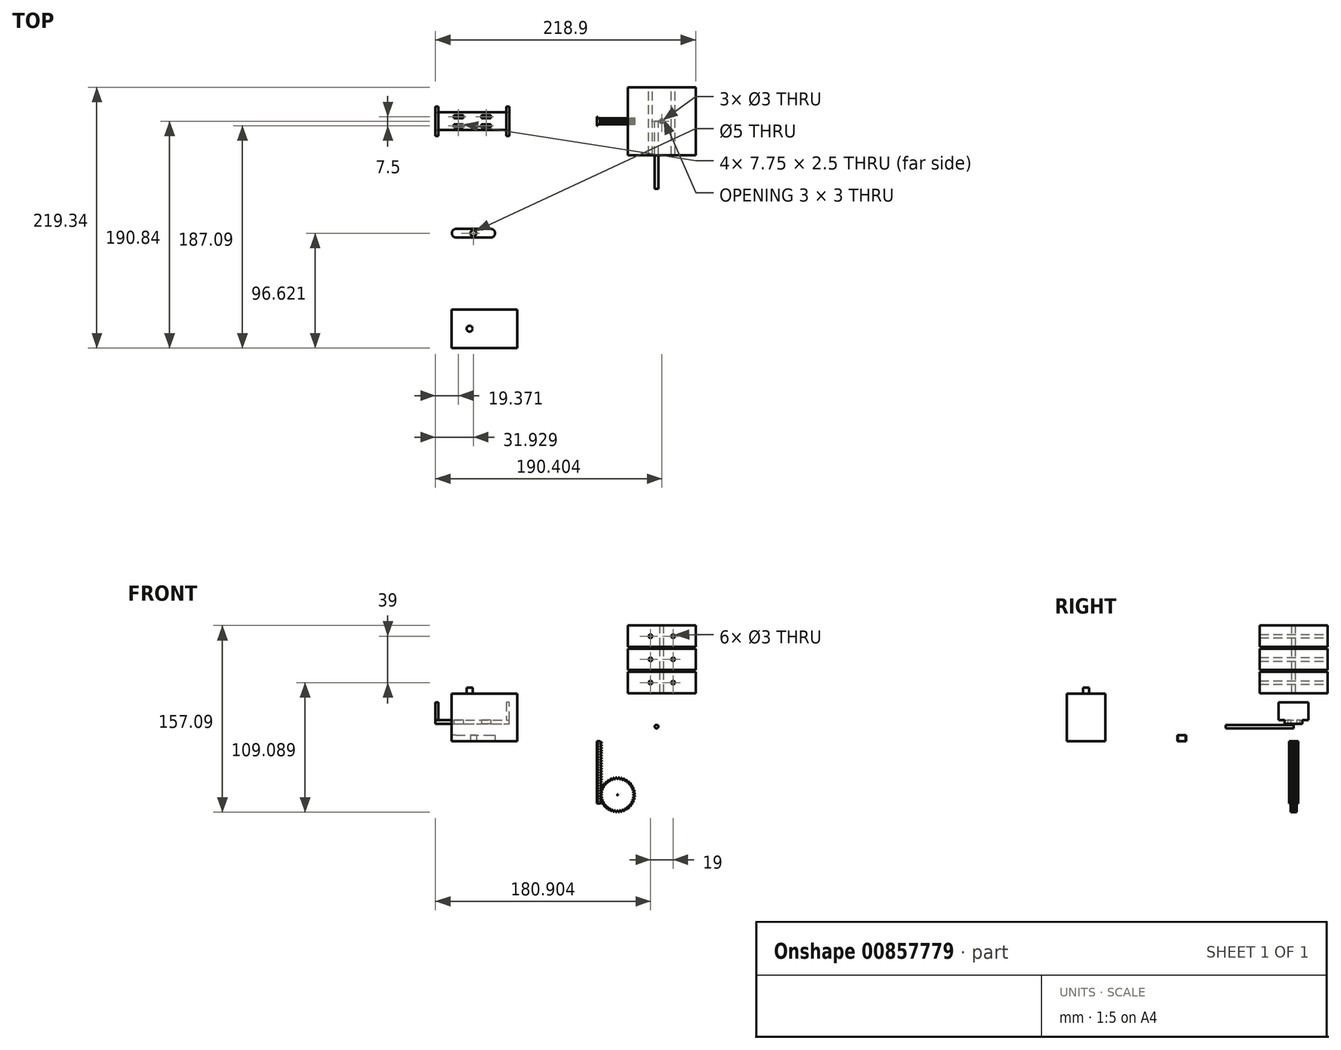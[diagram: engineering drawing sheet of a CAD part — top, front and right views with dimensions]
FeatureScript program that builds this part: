
annotation { "Feature Type Name" : "Feature", "Feature Type Description" : "" }
export const myFeature = defineFeature(function(context is Context, id is Id, definition is map)
    precondition{}
    {
        {
            var Q0;
            Q0=qCreatedBy(makeId("Front.planeOp"),FACE);
            var sketch = newSketch(context, id + "F0", { "sketchPlane" : qUnion([Q0])});
            skLineSegment(sketch, "E0", {"start": v(-13.26, -89.9) * mm, "end": v(-11.85, -89.4) * mm, "construction": true});
            skLineSegment(sketch, "E1", {"start": v(-11.85, -89.4) * mm, "end": v(-11.85, -88.8) * mm, "construction": true});
            skLineSegment(sketch, "E2", {"start": v(-11.85, -88.8) * mm, "end": v(-13.26, -88.31) * mm, "construction": true});
            skLineSegment(sketch, "E3", {"start": v(-13.26, -88.31) * mm, "end": v(-13.26, -87.7) * mm, "construction": true});
            skLineSegment(sketch, "E4", {"start": v(-13.26, -87.7) * mm, "end": v(-11.85, -87.21) * mm, "construction": true});
            skLineSegment(sketch, "E5", {"start": v(-11.85, -87.21) * mm, "end": v(-11.85, -86.6) * mm, "construction": true});
            skLineSegment(sketch, "E6", {"start": v(-11.85, -86.6) * mm, "end": v(-13.26, -86.12) * mm, "construction": true});
            skLineSegment(sketch, "E7", {"start": v(-13.26, -86.12) * mm, "end": v(-13.26, -85.5) * mm, "construction": true});
            skLineSegment(sketch, "E8", {"start": v(-13.26, -85.5) * mm, "end": v(-11.85, -85.02) * mm, "construction": true});
            skLineSegment(sketch, "E9", {"start": v(-11.85, -85.02) * mm, "end": v(-11.85, -84.4) * mm, "construction": true});
            skLineSegment(sketch, "E10", {"start": v(-11.85, -84.4) * mm, "end": v(-13.26, -83.92) * mm, "construction": true});
            skLineSegment(sketch, "E11", {"start": v(-13.26, -83.92) * mm, "end": v(-13.26, -83.3) * mm, "construction": true});
            skLineSegment(sketch, "E12", {"start": v(-13.26, -83.3) * mm, "end": v(-11.85, -82.82) * mm, "construction": true});
            skLineSegment(sketch, "E13", {"start": v(-11.85, -82.82) * mm, "end": v(-11.85, -82.2) * mm, "construction": true});
            skLineSegment(sketch, "E14", {"start": v(-11.85, -82.2) * mm, "end": v(-13.26, -81.73) * mm, "construction": true});
            skLineSegment(sketch, "E15", {"start": v(-13.26, -81.73) * mm, "end": v(-13.26, -81.11) * mm, "construction": true});
            skLineSegment(sketch, "E16", {"start": v(-13.26, -81.11) * mm, "end": v(-11.85, -80.63) * mm, "construction": true});
            skLineSegment(sketch, "E17", {"start": v(-11.85, -80.63) * mm, "end": v(-11.85, -80.01) * mm, "construction": true});
            skLineSegment(sketch, "E18", {"start": v(-11.85, -80.01) * mm, "end": v(-13.26, -79.53) * mm, "construction": true});
            skLineSegment(sketch, "E19", {"start": v(-13.26, -79.53) * mm, "end": v(-13.26, -78.92) * mm, "construction": true});
            skLineSegment(sketch, "E20", {"start": v(-13.26, -78.92) * mm, "end": v(-11.85, -78.43) * mm, "construction": true});
            skLineSegment(sketch, "E21", {"start": v(-11.85, -78.43) * mm, "end": v(-11.85, -77.82) * mm, "construction": true});
            skLineSegment(sketch, "E22", {"start": v(-11.85, -77.82) * mm, "end": v(-13.26, -77.34) * mm, "construction": true});
            skLineSegment(sketch, "E23", {"start": v(-13.26, -77.34) * mm, "end": v(-13.26, -76.72) * mm, "construction": true});
            skLineSegment(sketch, "E24", {"start": v(-13.26, -76.72) * mm, "end": v(-11.85, -76.24) * mm, "construction": true});
            skLineSegment(sketch, "E25", {"start": v(-11.85, -76.24) * mm, "end": v(-11.85, -75.62) * mm, "construction": true});
            skLineSegment(sketch, "E26", {"start": v(-11.85, -75.62) * mm, "end": v(-13.26, -75.14) * mm, "construction": true});
            skLineSegment(sketch, "E27", {"start": v(-13.26, -75.14) * mm, "end": v(-13.26, -74.53) * mm, "construction": true});
            skLineSegment(sketch, "E28", {"start": v(-13.26, -74.53) * mm, "end": v(-11.85, -74.04) * mm, "construction": true});
            skLineSegment(sketch, "E29", {"start": v(-11.85, -74.04) * mm, "end": v(-11.85, -73.43) * mm, "construction": true});
            skLineSegment(sketch, "E30", {"start": v(-11.85, -73.43) * mm, "end": v(-13.26, -72.95) * mm, "construction": true});
            skLineSegment(sketch, "E31", {"start": v(-13.26, -72.95) * mm, "end": v(-13.26, -72.33) * mm, "construction": true});
            skLineSegment(sketch, "E32", {"start": v(-13.26, -72.33) * mm, "end": v(-11.85, -71.85) * mm, "construction": true});
            skLineSegment(sketch, "E33", {"start": v(-11.85, -71.85) * mm, "end": v(-11.85, -71.23) * mm, "construction": true});
            skLineSegment(sketch, "E34", {"start": v(-11.85, -71.23) * mm, "end": v(-13.26, -70.75) * mm, "construction": true});
            skLineSegment(sketch, "E35", {"start": v(-13.26, -70.75) * mm, "end": v(-13.26, -70.13) * mm, "construction": true});
            skLineSegment(sketch, "E36", {"start": v(-13.26, -70.13) * mm, "end": v(-11.85, -69.65) * mm, "construction": true});
            skLineSegment(sketch, "E37", {"start": v(-11.85, -69.65) * mm, "end": v(-11.85, -69.04) * mm, "construction": true});
            skLineSegment(sketch, "E38", {"start": v(-11.85, -69.04) * mm, "end": v(-13.26, -68.56) * mm, "construction": true});
            skLineSegment(sketch, "E39", {"start": v(-13.26, -68.56) * mm, "end": v(-13.26, -67.94) * mm, "construction": true});
            skLineSegment(sketch, "E40", {"start": v(-13.26, -67.94) * mm, "end": v(-11.85, -67.46) * mm, "construction": true});
            skLineSegment(sketch, "E41", {"start": v(-11.85, -67.46) * mm, "end": v(-11.85, -66.84) * mm, "construction": true});
            skLineSegment(sketch, "E42", {"start": v(-11.85, -66.84) * mm, "end": v(-13.26, -66.36) * mm, "construction": true});
            skLineSegment(sketch, "E43", {"start": v(-13.26, -66.36) * mm, "end": v(-13.26, -65.74) * mm, "construction": true});
            skLineSegment(sketch, "E44", {"start": v(-13.26, -65.74) * mm, "end": v(-11.85, -65.26) * mm, "construction": true});
            skLineSegment(sketch, "E45", {"start": v(-11.85, -65.26) * mm, "end": v(-11.85, -64.65) * mm, "construction": true});
            skLineSegment(sketch, "E46", {"start": v(-11.85, -64.65) * mm, "end": v(-13.26, -64.17) * mm, "construction": true});
            skLineSegment(sketch, "E47", {"start": v(-13.26, -64.17) * mm, "end": v(-13.26, -63.55) * mm, "construction": true});
            skLineSegment(sketch, "E48", {"start": v(-13.26, -63.55) * mm, "end": v(-11.85, -63.07) * mm, "construction": true});
            skLineSegment(sketch, "E49", {"start": v(-11.85, -63.07) * mm, "end": v(-11.85, -62.45) * mm, "construction": true});
            skLineSegment(sketch, "E50", {"start": v(-11.85, -62.45) * mm, "end": v(-13.26, -61.97) * mm, "construction": true});
            skLineSegment(sketch, "E51", {"start": v(-13.26, -61.97) * mm, "end": v(-13.26, -61.35) * mm, "construction": true});
            skLineSegment(sketch, "E52", {"start": v(-13.26, -61.35) * mm, "end": v(-11.85, -60.87) * mm, "construction": true});
            skLineSegment(sketch, "E53", {"start": v(-11.85, -60.87) * mm, "end": v(-11.85, -60.26) * mm, "construction": true});
            skLineSegment(sketch, "E54", {"start": v(-11.85, -60.26) * mm, "end": v(-13.26, -59.78) * mm, "construction": true});
            skLineSegment(sketch, "E55", {"start": v(-13.26, -59.78) * mm, "end": v(-13.26, -59.16) * mm, "construction": true});
            skLineSegment(sketch, "E56", {"start": v(-13.26, -59.16) * mm, "end": v(-11.85, -58.68) * mm, "construction": true});
            skLineSegment(sketch, "E57", {"start": v(-11.85, -58.68) * mm, "end": v(-11.85, -58.06) * mm, "construction": true});
            skLineSegment(sketch, "E58", {"start": v(-11.85, -58.06) * mm, "end": v(-13.26, -57.58) * mm, "construction": true});
            skLineSegment(sketch, "E59", {"start": v(-13.26, -57.58) * mm, "end": v(-13.26, -56.96) * mm, "construction": true});
            skLineSegment(sketch, "E60", {"start": v(-13.26, -56.96) * mm, "end": v(-11.85, -56.48) * mm, "construction": true});
            skLineSegment(sketch, "E61", {"start": v(-11.85, -56.48) * mm, "end": v(-11.85, -55.87) * mm, "construction": true});
            skLineSegment(sketch, "E62", {"start": v(-11.85, -55.87) * mm, "end": v(-13.26, -55.39) * mm, "construction": true});
            skLineSegment(sketch, "E63", {"start": v(-13.26, -55.39) * mm, "end": v(-13.26, -54.77) * mm, "construction": true});
            skLineSegment(sketch, "E64", {"start": v(-13.26, -54.77) * mm, "end": v(-11.85, -54.29) * mm, "construction": true});
            skLineSegment(sketch, "E65", {"start": v(-11.85, -54.29) * mm, "end": v(-11.85, -53.67) * mm, "construction": true});
            skLineSegment(sketch, "E66", {"start": v(-11.85, -53.67) * mm, "end": v(-13.26, -53.2) * mm, "construction": true});
            skLineSegment(sketch, "E67", {"start": v(-13.26, -53.2) * mm, "end": v(-13.26, -52.57) * mm, "construction": true});
            skLineSegment(sketch, "E68", {"start": v(-13.26, -52.57) * mm, "end": v(-11.85, -52.1) * mm});
            skLineSegment(sketch, "E69", {"start": v(-11.85, -52.1) * mm, "end": v(-11.85, -51.48) * mm});
            skLineSegment(sketch, "E70", {"start": v(-11.85, -51.48) * mm, "end": v(-13.26, -51) * mm});
            skLineSegment(sketch, "E71", {"start": v(-13.26, -51) * mm, "end": v(-13.26, -50.38) * mm});
            skLineSegment(sketch, "E72", {"start": v(-13.26, -50.38) * mm, "end": v(-11.85, -49.9) * mm});
            skLineSegment(sketch, "E73", {"start": v(-11.85, -49.9) * mm, "end": v(-11.85, -49.28) * mm});
            skLineSegment(sketch, "E74", {"start": v(-11.85, -49.28) * mm, "end": v(-13.26, -48.8) * mm});
            skLineSegment(sketch, "E75", {"start": v(-13.26, -48.8) * mm, "end": v(-13.26, -48.18) * mm});
            skLineSegment(sketch, "E76", {"start": v(-13.26, -48.18) * mm, "end": v(-11.85, -47.7) * mm});
            skLineSegment(sketch, "E77", {"start": v(-11.85, -47.7) * mm, "end": v(-11.85, -47.09) * mm});
            skLineSegment(sketch, "E78", {"start": v(-11.85, -47.09) * mm, "end": v(-13.26, -46.6) * mm});
            skLineSegment(sketch, "E79", {"start": v(-13.26, -46.6) * mm, "end": v(-13.26, -45.99) * mm});
            skLineSegment(sketch, "E80", {"start": v(-13.26, -45.99) * mm, "end": v(-11.85, -45.5) * mm});
            skLineSegment(sketch, "E81", {"start": v(-11.85, -45.5) * mm, "end": v(-11.85, -44.9) * mm});
            skLineSegment(sketch, "E82", {"start": v(-11.85, -44.9) * mm, "end": v(-13.26, -44.41) * mm});
            skLineSegment(sketch, "E83", {"start": v(-13.26, -44.41) * mm, "end": v(-13.26, -43.8) * mm});
            skLineSegment(sketch, "E84", {"start": v(-13.26, -43.8) * mm, "end": v(-11.85, -43.31) * mm});
            skLineSegment(sketch, "E85", {"start": v(-11.85, -43.31) * mm, "end": v(-11.85, -42.7) * mm});
            skLineSegment(sketch, "E86", {"start": v(-11.85, -42.7) * mm, "end": v(-13.26, -42.22) * mm});
            skLineSegment(sketch, "E87", {"start": v(-13.26, -42.22) * mm, "end": v(-13.26, -41.6) * mm});
            skLineSegment(sketch, "E88", {"start": v(-13.26, -41.6) * mm, "end": v(-11.85, -41.12) * mm});
            skLineSegment(sketch, "E89", {"start": v(-11.85, -41.12) * mm, "end": v(-11.85, -40.5) * mm});
            skLineSegment(sketch, "E90", {"start": v(-11.85, -40.5) * mm, "end": v(-13.26, -40.02) * mm});
            skLineSegment(sketch, "E91", {"start": v(-13.26, -40.02) * mm, "end": v(-13.26, -39.4) * mm});
            skLineSegment(sketch, "E92", {"start": v(-13.26, -39.4) * mm, "end": v(-11.85, -38.92) * mm});
            skLineSegment(sketch, "E93", {"start": v(-11.85, -38.92) * mm, "end": v(-11.85, -38.3) * mm});
            skLineSegment(sketch, "E94", {"start": v(-11.85, -38.3) * mm, "end": v(-13.26, -37.83) * mm});
            skLineSegment(sketch, "E95", {"start": v(-13.26, -37.83) * mm, "end": v(-13.26, -37.2) * mm});
            skLineSegment(sketch, "E96", {"start": v(-13.26, -37.2) * mm, "end": v(-11.85, -36.73) * mm});
            skLineSegment(sketch, "E97", {"start": v(-11.85, -36.73) * mm, "end": v(-11.85, -36.11) * mm});
            skLineSegment(sketch, "E98", {"start": v(-11.85, -36.11) * mm, "end": v(-13.26, -35.63) * mm});
            skLineSegment(sketch, "E99", {"start": v(-13.26, -35.63) * mm, "end": v(-13.26, -35.01) * mm});
            skLineSegment(sketch, "E100", {"start": v(-13.26, -35.01) * mm, "end": v(-11.85, -34.53) * mm});
            skLineSegment(sketch, "E101", {"start": v(-11.85, -34.53) * mm, "end": v(-11.85, -33.92) * mm});
            skLineSegment(sketch, "E102", {"start": v(-11.85, -33.92) * mm, "end": v(-13.26, -33.44) * mm});
            skLineSegment(sketch, "E103", {"start": v(-13.26, -33.44) * mm, "end": v(-13.26, -32.82) * mm});
            skLineSegment(sketch, "E104", {"start": v(-13.26, -32.82) * mm, "end": v(-11.85, -32.34) * mm});
            skLineSegment(sketch, "E105", {"start": v(-11.85, -32.34) * mm, "end": v(-11.85, -31.72) * mm});
            skLineSegment(sketch, "E106", {"start": v(-11.85, -31.72) * mm, "end": v(-13.26, -31.24) * mm});
            skLineSegment(sketch, "E107", {"start": v(-13.26, -31.24) * mm, "end": v(-13.26, -30.62) * mm});
            skLineSegment(sketch, "E108", {"start": v(-13.26, -30.62) * mm, "end": v(-11.85, -30.14) * mm});
            skLineSegment(sketch, "E109", {"start": v(-11.85, -30.14) * mm, "end": v(-11.85, -29.53) * mm});
            skLineSegment(sketch, "E110", {"start": v(-11.85, -29.53) * mm, "end": v(-13.26, -29.05) * mm});
            skLineSegment(sketch, "E111", {"start": v(-13.26, -29.05) * mm, "end": v(-13.26, -28.43) * mm});
            skLineSegment(sketch, "E112", {"start": v(-13.26, -28.43) * mm, "end": v(-11.85, -27.95) * mm});
            skLineSegment(sketch, "E113", {"start": v(-11.85, -27.95) * mm, "end": v(-11.85, -27.33) * mm});
            skLineSegment(sketch, "E114", {"start": v(-11.85, -27.33) * mm, "end": v(-13.26, -26.85) * mm});
            skLineSegment(sketch, "E115", {"start": v(-13.26, -26.85) * mm, "end": v(-13.26, -26.23) * mm});
            skLineSegment(sketch, "E116", {"start": v(-13.26, -26.23) * mm, "end": v(-11.85, -25.75) * mm});
            skLineSegment(sketch, "E117", {"start": v(-11.85, -25.75) * mm, "end": v(-11.85, -25.14) * mm});
            skLineSegment(sketch, "E118", {"start": v(-11.85, -25.14) * mm, "end": v(-13.26, -24.66) * mm});
            skLineSegment(sketch, "E119", {"start": v(-13.26, -24.66) * mm, "end": v(-13.26, -24.04) * mm});
            skLineSegment(sketch, "E120", {"start": v(-13.26, -24.04) * mm, "end": v(-11.85, -23.56) * mm});
            skLineSegment(sketch, "E121", {"start": v(-11.85, -23.56) * mm, "end": v(-11.85, -22.94) * mm});
            skLineSegment(sketch, "E122", {"start": v(-11.85, -22.94) * mm, "end": v(-13.26, -22.46) * mm});
            skLineSegment(sketch, "E123", {"start": v(-13.26, -22.46) * mm, "end": v(-13.26, -21.84) * mm});
            skLineSegment(sketch, "E124", {"start": v(-13.26, -21.84) * mm, "end": v(-11.85, -21.36) * mm});
            skLineSegment(sketch, "E125", {"start": v(-11.85, -21.36) * mm, "end": v(-11.85, -20.75) * mm});
            skLineSegment(sketch, "E126", {"start": v(-11.85, -20.75) * mm, "end": v(-13.26, -20.27) * mm});
            skLineSegment(sketch, "E127", {"start": v(-13.26, -20.27) * mm, "end": v(-13.26, -19.65) * mm});
            skLineSegment(sketch, "E128", {"start": v(-13.26, -19.65) * mm, "end": v(-11.85, -19.17) * mm});
            skLineSegment(sketch, "E129", {"start": v(-11.85, -19.17) * mm, "end": v(-11.85, -18.55) * mm});
            skLineSegment(sketch, "E130", {"start": v(-11.85, -18.55) * mm, "end": v(-13.26, -18.07) * mm});
            skLineSegment(sketch, "E131", {"start": v(-13.26, -18.07) * mm, "end": v(-13.26, -17.45) * mm});
            skLineSegment(sketch, "E132", {"start": v(-13.26, -17.45) * mm, "end": v(-11.85, -16.97) * mm});
            skLineSegment(sketch, "E133", {"start": v(-11.85, -16.97) * mm, "end": v(-11.85, -16.36) * mm});
            skLineSegment(sketch, "E134", {"start": v(-11.85, -16.36) * mm, "end": v(-13.26, -15.87) * mm});
            skLineSegment(sketch, "E135", {"start": v(-13.26, -15.87) * mm, "end": v(-13.26, -15.26) * mm});
            skLineSegment(sketch, "E136", {"start": v(-13.26, -15.26) * mm, "end": v(-11.85, -14.78) * mm});
            skLineSegment(sketch, "E137", {"start": v(-11.85, -14.78) * mm, "end": v(-11.85, -14.16) * mm});
            skLineSegment(sketch, "E138", {"start": v(-11.85, -14.16) * mm, "end": v(-13.26, -13.68) * mm});
            skLineSegment(sketch, "E139", {"start": v(-13.26, -13.68) * mm, "end": v(-13.26, -13.06) * mm});
            skLineSegment(sketch, "E140", {"start": v(-13.26, -13.06) * mm, "end": v(-11.85, -12.58) * mm});
            skLineSegment(sketch, "E141", {"start": v(-11.85, -12.58) * mm, "end": v(-11.85, -11.97) * mm});
            skLineSegment(sketch, "E142", {"start": v(-11.85, -11.97) * mm, "end": v(-13.26, -11.48) * mm});
            skLineSegment(sketch, "E143", {"start": v(-13.26, -11.48) * mm, "end": v(-13.26, -10.87) * mm});
            skLineSegment(sketch, "E144", {"start": v(-13.26, -10.87) * mm, "end": v(-11.85, -10.39) * mm});
            skLineSegment(sketch, "E145", {"start": v(-11.85, -10.39) * mm, "end": v(-11.85, -9.77) * mm});
            skLineSegment(sketch, "E146", {"start": v(-11.85, -9.77) * mm, "end": v(-13.26, -9.29) * mm});
            skLineSegment(sketch, "E147", {"start": v(-13.26, -9.29) * mm, "end": v(-13.26, -8.67) * mm});
            skLineSegment(sketch, "E148", {"start": v(-13.26, -8.67) * mm, "end": v(-11.85, -8.2) * mm});
            skLineSegment(sketch, "E149", {"start": v(-11.85, -8.2) * mm, "end": v(-11.85, -7.58) * mm});
            skLineSegment(sketch, "E150", {"start": v(-11.85, -7.58) * mm, "end": v(-13.26, -7.1) * mm});
            skLineSegment(sketch, "E151", {"start": v(-13.26, -7.1) * mm, "end": v(-13.26, -6.48) * mm});
            skLineSegment(sketch, "E152", {"start": v(-13.26, -6.48) * mm, "end": v(-11.85, -6) * mm});
            skLineSegment(sketch, "E153", {"start": v(-11.85, -6) * mm, "end": v(-11.85, -5.38) * mm});
            skLineSegment(sketch, "E154", {"start": v(-11.85, -5.38) * mm, "end": v(-13.26, -4.9) * mm});
            skLineSegment(sketch, "E155", {"start": v(-13.26, -4.9) * mm, "end": v(-13.26, -4.28) * mm});
            skLineSegment(sketch, "E156", {"start": v(-13.26, -4.28) * mm, "end": v(-11.85, -3.8) * mm});
            skLineSegment(sketch, "E157", {"start": v(-11.85, -3.8) * mm, "end": v(-11.85, -3.19) * mm});
            skLineSegment(sketch, "E158", {"start": v(-11.85, -3.19) * mm, "end": v(-13.26, -2.7) * mm});
            skLineSegment(sketch, "E159", {"start": v(-13.26, -2.7) * mm, "end": v(-13.26, -2.09) * mm});
            skLineSegment(sketch, "E160", {"start": v(-13.26, -2.09) * mm, "end": v(-11.85, -1.6) * mm});
            skLineSegment(sketch, "E161", {"start": v(-11.85, -1.6) * mm, "end": v(-11.85, -1) * mm});
            skLineSegment(sketch, "E162", {"start": v(-11.85, -1) * mm, "end": v(-13.26, -0.5) * mm});
            skLineSegment(sketch, "E163", {"start": v(-13.26, -0.5) * mm, "end": v(-13.26, -0.2) * mm});
            skLineSegment(sketch, "E164", {"start": v(-13.26, -0.2) * mm, "end": v(-16.05, -0.2) * mm});
            skLineSegment(sketch, "E165", {"start": v(-16.05, -0.2) * mm, "end": v(-16.05, -90.2) * mm, "construction": true});
            skLineSegment(sketch, "E166", {"start": v(-16.05, -90.2) * mm, "end": v(-13.26, -90.2) * mm, "construction": true});
            skLineSegment(sketch, "E167", {"start": v(-13.26, -90.2) * mm, "end": v(-13.26, -89.9) * mm, "construction": true});
            skLineSegment(sketch, "E168", {"start": v(-13.16, -43.77) * mm, "end": v(-13.2, -44.05) * mm});
            skLineSegment(sketch, "E169", {"start": v(-13.2, -44.05) * mm, "end": v(-13.2, -44.33) * mm});
            skLineSegment(sketch, "E170", {"start": v(-13.2, -44.33) * mm, "end": v(-13.15, -44.36) * mm});
            skLineSegment(sketch, "E171", {"start": v(-13.15, -44.36) * mm, "end": v(-13.06, -44.4) * mm});
            skLineSegment(sketch, "E172", {"start": v(-13.06, -44.4) * mm, "end": v(-12.98, -44.45) * mm});
            skLineSegment(sketch, "E173", {"start": v(-12.98, -44.45) * mm, "end": v(-12.9, -44.49) * mm});
            skLineSegment(sketch, "E174", {"start": v(-12.9, -44.49) * mm, "end": v(-12.82, -44.53) * mm});
            skLineSegment(sketch, "E175", {"start": v(-12.82, -44.53) * mm, "end": v(-12.75, -44.56) * mm});
            skLineSegment(sketch, "E176", {"start": v(-12.75, -44.56) * mm, "end": v(-12.68, -44.6) * mm});
            skLineSegment(sketch, "E177", {"start": v(-12.68, -44.6) * mm, "end": v(-12.6, -44.62) * mm});
            skLineSegment(sketch, "E178", {"start": v(-12.6, -44.62) * mm, "end": v(-12.54, -44.65) * mm});
            skLineSegment(sketch, "E179", {"start": v(-12.54, -44.65) * mm, "end": v(-12.47, -44.67) * mm});
            skLineSegment(sketch, "E180", {"start": v(-12.47, -44.67) * mm, "end": v(-12.41, -44.7) * mm});
            skLineSegment(sketch, "E181", {"start": v(-12.41, -44.7) * mm, "end": v(-12.35, -44.71) * mm});
            skLineSegment(sketch, "E182", {"start": v(-12.35, -44.71) * mm, "end": v(-12.3, -44.73) * mm});
            skLineSegment(sketch, "E183", {"start": v(-12.3, -44.73) * mm, "end": v(-12.24, -44.75) * mm});
            skLineSegment(sketch, "E184", {"start": v(-12.24, -44.75) * mm, "end": v(-12.19, -44.76) * mm});
            skLineSegment(sketch, "E185", {"start": v(-12.19, -44.76) * mm, "end": v(-12.14, -44.78) * mm});
            skLineSegment(sketch, "E186", {"start": v(-12.14, -44.78) * mm, "end": v(-12.1, -44.79) * mm});
            skLineSegment(sketch, "E187", {"start": v(-12.1, -44.79) * mm, "end": v(-12.05, -44.8) * mm});
            skLineSegment(sketch, "E188", {"start": v(-12.05, -44.8) * mm, "end": v(-12.02, -44.8) * mm});
            skLineSegment(sketch, "E189", {"start": v(-12.02, -44.8) * mm, "end": v(-12, -44.81) * mm});
            skLineSegment(sketch, "E190", {"start": v(-12, -44.81) * mm, "end": v(-11.96, -44.82) * mm});
            skLineSegment(sketch, "E191", {"start": v(-11.96, -44.82) * mm, "end": v(-11.94, -44.83) * mm});
            skLineSegment(sketch, "E192", {"start": v(-11.94, -44.83) * mm, "end": v(-11.91, -44.84) * mm});
            skLineSegment(sketch, "E193", {"start": v(-11.91, -44.84) * mm, "end": v(-11.9, -44.85) * mm});
            skLineSegment(sketch, "E194", {"start": v(-11.9, -44.85) * mm, "end": v(-11.87, -44.86) * mm});
            skLineSegment(sketch, "E195", {"start": v(-11.87, -44.86) * mm, "end": v(-11.86, -44.87) * mm});
            skLineSegment(sketch, "E196", {"start": v(-11.86, -44.87) * mm, "end": v(-11.85, -44.88) * mm});
            skLineSegment(sketch, "E197", {"start": v(-11.85, -44.88) * mm, "end": v(-11.84, -44.89) * mm});
            skLineSegment(sketch, "E198", {"start": v(-11.84, -44.89) * mm, "end": v(-11.84, -44.9) * mm});
            skLineSegment(sketch, "E199", {"start": v(-11.84, -44.9) * mm, "end": v(-11.84, -45.1) * mm});
            skLineSegment(sketch, "E200", {"start": v(-11.84, -45.1) * mm, "end": v(-11.84, -45.3) * mm});
            skLineSegment(sketch, "E201", {"start": v(-11.84, -45.3) * mm, "end": v(-11.84, -45.5) * mm});
            skLineSegment(sketch, "E202", {"start": v(-11.84, -45.5) * mm, "end": v(-11.84, -45.51) * mm});
            skLineSegment(sketch, "E203", {"start": v(-11.84, -45.51) * mm, "end": v(-11.85, -45.52) * mm});
            skLineSegment(sketch, "E204", {"start": v(-11.85, -45.52) * mm, "end": v(-11.86, -45.53) * mm});
            skLineSegment(sketch, "E205", {"start": v(-11.86, -45.53) * mm, "end": v(-11.87, -45.54) * mm});
            skLineSegment(sketch, "E206", {"start": v(-11.87, -45.54) * mm, "end": v(-11.9, -45.55) * mm});
            skLineSegment(sketch, "E207", {"start": v(-11.9, -45.55) * mm, "end": v(-11.91, -45.56) * mm});
            skLineSegment(sketch, "E208", {"start": v(-11.91, -45.56) * mm, "end": v(-11.94, -45.57) * mm});
            skLineSegment(sketch, "E209", {"start": v(-11.94, -45.57) * mm, "end": v(-11.96, -45.58) * mm});
            skLineSegment(sketch, "E210", {"start": v(-11.96, -45.58) * mm, "end": v(-12, -45.59) * mm});
            skLineSegment(sketch, "E211", {"start": v(-12, -45.59) * mm, "end": v(-12.02, -45.6) * mm});
            skLineSegment(sketch, "E212", {"start": v(-12.02, -45.6) * mm, "end": v(-12.05, -45.6) * mm});
            skLineSegment(sketch, "E213", {"start": v(-12.05, -45.6) * mm, "end": v(-12.1, -45.61) * mm});
            skLineSegment(sketch, "E214", {"start": v(-12.1, -45.61) * mm, "end": v(-12.14, -45.62) * mm});
            skLineSegment(sketch, "E215", {"start": v(-12.14, -45.62) * mm, "end": v(-12.19, -45.64) * mm});
            skLineSegment(sketch, "E216", {"start": v(-12.19, -45.64) * mm, "end": v(-12.24, -45.65) * mm});
            skLineSegment(sketch, "E217", {"start": v(-12.24, -45.65) * mm, "end": v(-12.3, -45.67) * mm});
            skLineSegment(sketch, "E218", {"start": v(-12.3, -45.67) * mm, "end": v(-12.35, -45.69) * mm});
            skLineSegment(sketch, "E219", {"start": v(-12.35, -45.69) * mm, "end": v(-12.41, -45.7) * mm});
            skLineSegment(sketch, "E220", {"start": v(-12.41, -45.7) * mm, "end": v(-12.47, -45.73) * mm});
            skLineSegment(sketch, "E221", {"start": v(-12.47, -45.73) * mm, "end": v(-12.54, -45.75) * mm});
            skLineSegment(sketch, "E222", {"start": v(-12.54, -45.75) * mm, "end": v(-12.6, -45.78) * mm});
            skLineSegment(sketch, "E223", {"start": v(-12.6, -45.78) * mm, "end": v(-12.68, -45.8) * mm});
            skLineSegment(sketch, "E224", {"start": v(-12.68, -45.8) * mm, "end": v(-12.75, -45.84) * mm});
            skLineSegment(sketch, "E225", {"start": v(-12.75, -45.84) * mm, "end": v(-12.82, -45.87) * mm});
            skLineSegment(sketch, "E226", {"start": v(-12.82, -45.87) * mm, "end": v(-12.9, -45.91) * mm});
            skLineSegment(sketch, "E227", {"start": v(-12.9, -45.91) * mm, "end": v(-12.98, -45.95) * mm});
            skLineSegment(sketch, "E228", {"start": v(-12.98, -45.95) * mm, "end": v(-13.06, -46) * mm});
            skLineSegment(sketch, "E229", {"start": v(-13.06, -46) * mm, "end": v(-13.15, -46.04) * mm});
            skLineSegment(sketch, "E230", {"start": v(-13.15, -46.04) * mm, "end": v(-13.2, -46.07) * mm});
            skLineSegment(sketch, "E231", {"start": v(-13.2, -46.07) * mm, "end": v(-13.2, -46.35) * mm});
            skLineSegment(sketch, "E232", {"start": v(-13.2, -46.35) * mm, "end": v(-13.16, -46.63) * mm});
            skLineSegment(sketch, "E233", {"start": v(-13.16, -46.63) * mm, "end": v(-13.1, -46.65) * mm});
            skLineSegment(sketch, "E234", {"start": v(-13.1, -46.65) * mm, "end": v(-13, -46.68) * mm});
            skLineSegment(sketch, "E235", {"start": v(-13, -46.68) * mm, "end": v(-12.92, -46.71) * mm});
            skLineSegment(sketch, "E236", {"start": v(-12.92, -46.71) * mm, "end": v(-12.84, -46.74) * mm});
            skLineSegment(sketch, "E237", {"start": v(-12.84, -46.74) * mm, "end": v(-12.75, -46.76) * mm});
            skLineSegment(sketch, "E238", {"start": v(-12.75, -46.76) * mm, "end": v(-12.67, -46.79) * mm});
            skLineSegment(sketch, "E239", {"start": v(-12.67, -46.79) * mm, "end": v(-12.6, -46.8) * mm});
            skLineSegment(sketch, "E240", {"start": v(-12.6, -46.8) * mm, "end": v(-12.52, -46.82) * mm});
            skLineSegment(sketch, "E241", {"start": v(-12.52, -46.82) * mm, "end": v(-12.45, -46.84) * mm});
            skLineSegment(sketch, "E242", {"start": v(-12.45, -46.84) * mm, "end": v(-12.38, -46.85) * mm});
            skLineSegment(sketch, "E243", {"start": v(-12.38, -46.85) * mm, "end": v(-12.32, -46.86) * mm});
            skLineSegment(sketch, "E244", {"start": v(-12.32, -46.86) * mm, "end": v(-12.26, -46.88) * mm});
            skLineSegment(sketch, "E245", {"start": v(-12.26, -46.88) * mm, "end": v(-12.2, -46.88) * mm});
            skLineSegment(sketch, "E246", {"start": v(-12.2, -46.88) * mm, "end": v(-12.14, -46.9) * mm});
            skLineSegment(sketch, "E247", {"start": v(-12.14, -46.9) * mm, "end": v(-12.1, -46.9) * mm});
            skLineSegment(sketch, "E248", {"start": v(-12.1, -46.9) * mm, "end": v(-12.04, -46.9) * mm});
            skLineSegment(sketch, "E249", {"start": v(-12.04, -46.9) * mm, "end": v(-12, -46.9) * mm});
            skLineSegment(sketch, "E250", {"start": v(-12, -46.9) * mm, "end": v(-11.95, -46.91) * mm});
            skLineSegment(sketch, "E251", {"start": v(-11.95, -46.91) * mm, "end": v(-11.91, -46.91) * mm});
            skLineSegment(sketch, "E252", {"start": v(-11.91, -46.91) * mm, "end": v(-11.9, -46.92) * mm});
            skLineSegment(sketch, "E253", {"start": v(-11.9, -46.92) * mm, "end": v(-11.86, -46.92) * mm});
            skLineSegment(sketch, "E254", {"start": v(-11.86, -46.92) * mm, "end": v(-11.83, -46.92) * mm});
            skLineSegment(sketch, "E255", {"start": v(-11.83, -46.92) * mm, "end": v(-11.8, -46.93) * mm});
            skLineSegment(sketch, "E256", {"start": v(-11.8, -46.93) * mm, "end": v(-11.78, -46.93) * mm});
            skLineSegment(sketch, "E257", {"start": v(-11.78, -46.93) * mm, "end": v(-11.76, -46.94) * mm});
            skLineSegment(sketch, "E258", {"start": v(-11.76, -46.94) * mm, "end": v(-11.75, -46.95) * mm});
            skLineSegment(sketch, "E259", {"start": v(-11.75, -46.95) * mm, "end": v(-11.74, -46.96) * mm});
            skLineSegment(sketch, "E260", {"start": v(-11.74, -46.96) * mm, "end": v(-11.73, -46.97) * mm});
            skLineSegment(sketch, "E261", {"start": v(-11.73, -46.97) * mm, "end": v(-11.72, -46.98) * mm});
            skLineSegment(sketch, "E262", {"start": v(-11.72, -46.98) * mm, "end": v(-11.7, -47.17) * mm});
            skLineSegment(sketch, "E263", {"start": v(-11.7, -47.17) * mm, "end": v(-11.66, -47.38) * mm});
            skLineSegment(sketch, "E264", {"start": v(-11.66, -47.38) * mm, "end": v(-11.63, -47.57) * mm});
            skLineSegment(sketch, "E265", {"start": v(-11.63, -47.57) * mm, "end": v(-11.63, -47.58) * mm});
            skLineSegment(sketch, "E266", {"start": v(-11.63, -47.58) * mm, "end": v(-11.63, -47.6) * mm});
            skLineSegment(sketch, "E267", {"start": v(-11.63, -47.6) * mm, "end": v(-11.64, -47.6) * mm});
            skLineSegment(sketch, "E268", {"start": v(-11.64, -47.6) * mm, "end": v(-11.66, -47.62) * mm});
            skLineSegment(sketch, "E269", {"start": v(-11.66, -47.62) * mm, "end": v(-11.67, -47.63) * mm});
            skLineSegment(sketch, "E270", {"start": v(-11.67, -47.63) * mm, "end": v(-11.7, -47.65) * mm});
            skLineSegment(sketch, "E271", {"start": v(-11.7, -47.65) * mm, "end": v(-11.71, -47.66) * mm});
            skLineSegment(sketch, "E272", {"start": v(-11.71, -47.66) * mm, "end": v(-11.74, -47.67) * mm});
            skLineSegment(sketch, "E273", {"start": v(-11.74, -47.67) * mm, "end": v(-11.77, -47.68) * mm});
            skLineSegment(sketch, "E274", {"start": v(-11.77, -47.68) * mm, "end": v(-11.79, -47.7) * mm});
            skLineSegment(sketch, "E275", {"start": v(-11.79, -47.7) * mm, "end": v(-11.83, -47.7) * mm});
            skLineSegment(sketch, "E276", {"start": v(-11.83, -47.7) * mm, "end": v(-11.87, -47.72) * mm});
            skLineSegment(sketch, "E277", {"start": v(-11.87, -47.72) * mm, "end": v(-11.9, -47.74) * mm});
            skLineSegment(sketch, "E278", {"start": v(-11.9, -47.74) * mm, "end": v(-11.95, -47.76) * mm});
            skLineSegment(sketch, "E279", {"start": v(-11.95, -47.76) * mm, "end": v(-12, -47.78) * mm});
            skLineSegment(sketch, "E280", {"start": v(-12, -47.78) * mm, "end": v(-12.05, -47.8) * mm});
            skLineSegment(sketch, "E281", {"start": v(-12.05, -47.8) * mm, "end": v(-12.1, -47.83) * mm});
            skLineSegment(sketch, "E282", {"start": v(-12.1, -47.83) * mm, "end": v(-12.16, -47.86) * mm});
            skLineSegment(sketch, "E283", {"start": v(-12.16, -47.86) * mm, "end": v(-12.22, -47.9) * mm});
            skLineSegment(sketch, "E284", {"start": v(-12.22, -47.9) * mm, "end": v(-12.28, -47.93) * mm});
            skLineSegment(sketch, "E285", {"start": v(-12.28, -47.93) * mm, "end": v(-12.34, -47.97) * mm});
            skLineSegment(sketch, "E286", {"start": v(-12.34, -47.97) * mm, "end": v(-12.4, -48) * mm});
            skLineSegment(sketch, "E287", {"start": v(-12.4, -48) * mm, "end": v(-12.47, -48.05) * mm});
            skLineSegment(sketch, "E288", {"start": v(-12.47, -48.05) * mm, "end": v(-12.54, -48.1) * mm});
            skLineSegment(sketch, "E289", {"start": v(-12.54, -48.1) * mm, "end": v(-12.61, -48.14) * mm});
            skLineSegment(sketch, "E290", {"start": v(-12.61, -48.14) * mm, "end": v(-12.69, -48.2) * mm});
            skLineSegment(sketch, "E291", {"start": v(-12.69, -48.2) * mm, "end": v(-12.76, -48.25) * mm});
            skLineSegment(sketch, "E292", {"start": v(-12.76, -48.25) * mm, "end": v(-12.84, -48.3) * mm});
            skLineSegment(sketch, "E293", {"start": v(-12.84, -48.3) * mm, "end": v(-12.89, -48.34) * mm});
            skLineSegment(sketch, "E294", {"start": v(-12.89, -48.34) * mm, "end": v(-12.84, -48.63) * mm});
            skLineSegment(sketch, "E295", {"start": v(-12.84, -48.63) * mm, "end": v(-12.76, -48.9) * mm});
            skLineSegment(sketch, "E296", {"start": v(-12.76, -48.9) * mm, "end": v(-12.7, -48.9) * mm});
            skLineSegment(sketch, "E297", {"start": v(-12.7, -48.9) * mm, "end": v(-12.6, -48.92) * mm});
            skLineSegment(sketch, "E298", {"start": v(-12.6, -48.92) * mm, "end": v(-12.5, -48.94) * mm});
            skLineSegment(sketch, "E299", {"start": v(-12.5, -48.94) * mm, "end": v(-12.42, -48.95) * mm});
            skLineSegment(sketch, "E300", {"start": v(-12.42, -48.95) * mm, "end": v(-12.33, -48.96) * mm});
            skLineSegment(sketch, "E301", {"start": v(-12.33, -48.96) * mm, "end": v(-12.25, -48.97) * mm});
            skLineSegment(sketch, "E302", {"start": v(-12.25, -48.97) * mm, "end": v(-12.17, -48.98) * mm});
            skLineSegment(sketch, "E303", {"start": v(-12.17, -48.98) * mm, "end": v(-12.1, -48.98) * mm});
            skLineSegment(sketch, "E304", {"start": v(-12.1, -48.98) * mm, "end": v(-12.03, -48.99) * mm});
            skLineSegment(sketch, "E305", {"start": v(-12.03, -48.99) * mm, "end": v(-11.96, -49) * mm});
            skLineSegment(sketch, "E306", {"start": v(-11.96, -49) * mm, "end": v(-11.89, -49) * mm});
            skLineSegment(sketch, "E307", {"start": v(-11.89, -49) * mm, "end": v(-11.83, -49) * mm});
            skLineSegment(sketch, "E308", {"start": v(-11.83, -49) * mm, "end": v(-11.77, -49) * mm});
            skLineSegment(sketch, "E309", {"start": v(-11.77, -49) * mm, "end": v(-11.71, -49) * mm});
            skLineSegment(sketch, "E310", {"start": v(-11.71, -49) * mm, "end": v(-11.66, -49) * mm});
            skLineSegment(sketch, "E311", {"start": v(-11.66, -49) * mm, "end": v(-11.6, -49) * mm});
            skLineSegment(sketch, "E312", {"start": v(-11.6, -49) * mm, "end": v(-11.56, -48.99) * mm});
            skLineSegment(sketch, "E313", {"start": v(-11.56, -48.99) * mm, "end": v(-11.52, -48.98) * mm});
            skLineSegment(sketch, "E314", {"start": v(-11.52, -48.98) * mm, "end": v(-11.48, -48.98) * mm});
            skLineSegment(sketch, "E315", {"start": v(-11.48, -48.98) * mm, "end": v(-11.46, -48.98) * mm});
            skLineSegment(sketch, "E316", {"start": v(-11.46, -48.98) * mm, "end": v(-11.43, -48.98) * mm});
            skLineSegment(sketch, "E317", {"start": v(-11.43, -48.98) * mm, "end": v(-11.4, -48.97) * mm});
            skLineSegment(sketch, "E318", {"start": v(-11.4, -48.97) * mm, "end": v(-11.37, -48.98) * mm});
            skLineSegment(sketch, "E319", {"start": v(-11.37, -48.98) * mm, "end": v(-11.35, -48.98) * mm});
            skLineSegment(sketch, "E320", {"start": v(-11.35, -48.98) * mm, "end": v(-11.33, -48.98) * mm});
            skLineSegment(sketch, "E321", {"start": v(-11.33, -48.98) * mm, "end": v(-11.31, -48.99) * mm});
            skLineSegment(sketch, "E322", {"start": v(-11.31, -48.99) * mm, "end": v(-11.3, -49) * mm});
            skLineSegment(sketch, "E323", {"start": v(-11.3, -49) * mm, "end": v(-11.29, -49) * mm});
            skLineSegment(sketch, "E324", {"start": v(-11.29, -49) * mm, "end": v(-11.28, -49.01) * mm});
            skLineSegment(sketch, "E325", {"start": v(-11.28, -49.01) * mm, "end": v(-11.22, -49.2) * mm});
            skLineSegment(sketch, "E326", {"start": v(-11.22, -49.2) * mm, "end": v(-11.16, -49.4) * mm});
            skLineSegment(sketch, "E327", {"start": v(-11.16, -49.4) * mm, "end": v(-11.1, -49.58) * mm});
            skLineSegment(sketch, "E328", {"start": v(-11.1, -49.58) * mm, "end": v(-11.1, -49.6) * mm});
            skLineSegment(sketch, "E329", {"start": v(-11.1, -49.6) * mm, "end": v(-11.1, -49.6) * mm});
            skLineSegment(sketch, "E330", {"start": v(-11.1, -49.6) * mm, "end": v(-11.1, -49.62) * mm});
            skLineSegment(sketch, "E331", {"start": v(-11.1, -49.62) * mm, "end": v(-11.12, -49.64) * mm});
            skLineSegment(sketch, "E332", {"start": v(-11.12, -49.64) * mm, "end": v(-11.13, -49.65) * mm});
            skLineSegment(sketch, "E333", {"start": v(-11.13, -49.65) * mm, "end": v(-11.15, -49.67) * mm});
            skLineSegment(sketch, "E334", {"start": v(-11.15, -49.67) * mm, "end": v(-11.17, -49.68) * mm});
            skLineSegment(sketch, "E335", {"start": v(-11.17, -49.68) * mm, "end": v(-11.2, -49.7) * mm});
            skLineSegment(sketch, "E336", {"start": v(-11.2, -49.7) * mm, "end": v(-11.22, -49.72) * mm});
            skLineSegment(sketch, "E337", {"start": v(-11.22, -49.72) * mm, "end": v(-11.24, -49.73) * mm});
            skLineSegment(sketch, "E338", {"start": v(-11.24, -49.73) * mm, "end": v(-11.27, -49.75) * mm});
            skLineSegment(sketch, "E339", {"start": v(-11.27, -49.75) * mm, "end": v(-11.3, -49.77) * mm});
            skLineSegment(sketch, "E340", {"start": v(-11.3, -49.77) * mm, "end": v(-11.35, -49.8) * mm});
            skLineSegment(sketch, "E341", {"start": v(-11.35, -49.8) * mm, "end": v(-11.39, -49.82) * mm});
            skLineSegment(sketch, "E342", {"start": v(-11.39, -49.82) * mm, "end": v(-11.43, -49.85) * mm});
            skLineSegment(sketch, "E343", {"start": v(-11.43, -49.85) * mm, "end": v(-11.48, -49.88) * mm});
            skLineSegment(sketch, "E344", {"start": v(-11.48, -49.88) * mm, "end": v(-11.53, -49.92) * mm});
            skLineSegment(sketch, "E345", {"start": v(-11.53, -49.92) * mm, "end": v(-11.58, -49.96) * mm});
            skLineSegment(sketch, "E346", {"start": v(-11.58, -49.96) * mm, "end": v(-11.63, -50) * mm});
            skLineSegment(sketch, "E347", {"start": v(-11.63, -50) * mm, "end": v(-11.68, -50.04) * mm});
            skLineSegment(sketch, "E348", {"start": v(-11.68, -50.04) * mm, "end": v(-11.74, -50.09) * mm});
            skLineSegment(sketch, "E349", {"start": v(-11.74, -50.09) * mm, "end": v(-11.8, -50.14) * mm});
            skLineSegment(sketch, "E350", {"start": v(-11.8, -50.14) * mm, "end": v(-11.86, -50.19) * mm});
            skLineSegment(sketch, "E351", {"start": v(-11.86, -50.19) * mm, "end": v(-11.92, -50.24) * mm});
            skLineSegment(sketch, "E352", {"start": v(-11.92, -50.24) * mm, "end": v(-11.98, -50.3) * mm});
            skLineSegment(sketch, "E353", {"start": v(-11.98, -50.3) * mm, "end": v(-12.04, -50.36) * mm});
            skLineSegment(sketch, "E354", {"start": v(-12.04, -50.36) * mm, "end": v(-12.1, -50.43) * mm});
            skLineSegment(sketch, "E355", {"start": v(-12.1, -50.43) * mm, "end": v(-12.18, -50.5) * mm});
            skLineSegment(sketch, "E356", {"start": v(-12.18, -50.5) * mm, "end": v(-12.22, -50.54) * mm});
            skLineSegment(sketch, "E357", {"start": v(-12.22, -50.54) * mm, "end": v(-12.13, -50.82) * mm});
            skLineSegment(sketch, "E358", {"start": v(-12.13, -50.82) * mm, "end": v(-12, -51.07) * mm});
            skLineSegment(sketch, "E359", {"start": v(-12, -51.07) * mm, "end": v(-11.94, -51.07) * mm});
            skLineSegment(sketch, "E360", {"start": v(-11.94, -51.07) * mm, "end": v(-11.84, -51.07) * mm});
            skLineSegment(sketch, "E361", {"start": v(-11.84, -51.07) * mm, "end": v(-11.75, -51.07) * mm});
            skLineSegment(sketch, "E362", {"start": v(-11.75, -51.07) * mm, "end": v(-11.66, -51.07) * mm});
            skLineSegment(sketch, "E363", {"start": v(-11.66, -51.07) * mm, "end": v(-11.58, -51.07) * mm});
            skLineSegment(sketch, "E364", {"start": v(-11.58, -51.07) * mm, "end": v(-11.5, -51.06) * mm});
            skLineSegment(sketch, "E365", {"start": v(-11.5, -51.06) * mm, "end": v(-11.41, -51.06) * mm});
            skLineSegment(sketch, "E366", {"start": v(-11.41, -51.06) * mm, "end": v(-11.34, -51.05) * mm});
            skLineSegment(sketch, "E367", {"start": v(-11.34, -51.05) * mm, "end": v(-11.27, -51.05) * mm});
            skLineSegment(sketch, "E368", {"start": v(-11.27, -51.05) * mm, "end": v(-11.2, -51.04) * mm});
            skLineSegment(sketch, "E369", {"start": v(-11.2, -51.04) * mm, "end": v(-11.13, -51.03) * mm});
            skLineSegment(sketch, "E370", {"start": v(-11.13, -51.03) * mm, "end": v(-11.07, -51.02) * mm});
            skLineSegment(sketch, "E371", {"start": v(-11.07, -51.02) * mm, "end": v(-11.01, -51.01) * mm});
            skLineSegment(sketch, "E372", {"start": v(-11.01, -51.01) * mm, "end": v(-10.96, -51) * mm});
            skLineSegment(sketch, "E373", {"start": v(-10.96, -51) * mm, "end": v(-10.9, -51) * mm});
            skLineSegment(sketch, "E374", {"start": v(-10.9, -51) * mm, "end": v(-10.86, -50.98) * mm});
            skLineSegment(sketch, "E375", {"start": v(-10.86, -50.98) * mm, "end": v(-10.8, -50.97) * mm});
            skLineSegment(sketch, "E376", {"start": v(-10.8, -50.97) * mm, "end": v(-10.77, -50.96) * mm});
            skLineSegment(sketch, "E377", {"start": v(-10.77, -50.96) * mm, "end": v(-10.73, -50.95) * mm});
            skLineSegment(sketch, "E378", {"start": v(-10.73, -50.95) * mm, "end": v(-10.71, -50.95) * mm});
            skLineSegment(sketch, "E379", {"start": v(-10.71, -50.95) * mm, "end": v(-10.68, -50.94) * mm});
            skLineSegment(sketch, "E380", {"start": v(-10.68, -50.94) * mm, "end": v(-10.65, -50.93) * mm});
            skLineSegment(sketch, "E381", {"start": v(-10.65, -50.93) * mm, "end": v(-10.62, -50.93) * mm});
            skLineSegment(sketch, "E382", {"start": v(-10.62, -50.93) * mm, "end": v(-10.6, -50.93) * mm});
            skLineSegment(sketch, "E383", {"start": v(-10.6, -50.93) * mm, "end": v(-10.58, -50.93) * mm});
            skLineSegment(sketch, "E384", {"start": v(-10.58, -50.93) * mm, "end": v(-10.56, -50.93) * mm});
            skLineSegment(sketch, "E385", {"start": v(-10.56, -50.93) * mm, "end": v(-10.55, -50.94) * mm});
            skLineSegment(sketch, "E386", {"start": v(-10.55, -50.94) * mm, "end": v(-10.54, -50.95) * mm});
            skLineSegment(sketch, "E387", {"start": v(-10.54, -50.95) * mm, "end": v(-10.53, -50.95) * mm});
            skLineSegment(sketch, "E388", {"start": v(-10.53, -50.95) * mm, "end": v(-10.44, -51.13) * mm});
            skLineSegment(sketch, "E389", {"start": v(-10.44, -51.13) * mm, "end": v(-10.35, -51.32) * mm});
            skLineSegment(sketch, "E390", {"start": v(-10.35, -51.32) * mm, "end": v(-10.26, -51.49) * mm});
            skLineSegment(sketch, "E391", {"start": v(-10.26, -51.49) * mm, "end": v(-10.25, -51.5) * mm});
            skLineSegment(sketch, "E392", {"start": v(-10.25, -51.5) * mm, "end": v(-10.26, -51.51) * mm});
            skLineSegment(sketch, "E393", {"start": v(-10.26, -51.51) * mm, "end": v(-10.26, -51.53) * mm});
            skLineSegment(sketch, "E394", {"start": v(-10.26, -51.53) * mm, "end": v(-10.27, -51.54) * mm});
            skLineSegment(sketch, "E395", {"start": v(-10.27, -51.54) * mm, "end": v(-10.28, -51.56) * mm});
            skLineSegment(sketch, "E396", {"start": v(-10.28, -51.56) * mm, "end": v(-10.3, -51.58) * mm});
            skLineSegment(sketch, "E397", {"start": v(-10.3, -51.58) * mm, "end": v(-10.31, -51.6) * mm});
            skLineSegment(sketch, "E398", {"start": v(-10.31, -51.6) * mm, "end": v(-10.33, -51.62) * mm});
            skLineSegment(sketch, "E399", {"start": v(-10.33, -51.62) * mm, "end": v(-10.36, -51.64) * mm});
            skLineSegment(sketch, "E400", {"start": v(-10.36, -51.64) * mm, "end": v(-10.37, -51.65) * mm});
            skLineSegment(sketch, "E401", {"start": v(-10.37, -51.65) * mm, "end": v(-10.4, -51.68) * mm});
            skLineSegment(sketch, "E402", {"start": v(-10.4, -51.68) * mm, "end": v(-10.44, -51.7) * mm});
            skLineSegment(sketch, "E403", {"start": v(-10.44, -51.7) * mm, "end": v(-10.47, -51.74) * mm});
            skLineSegment(sketch, "E404", {"start": v(-10.47, -51.74) * mm, "end": v(-10.5, -51.77) * mm});
            skLineSegment(sketch, "E405", {"start": v(-10.5, -51.77) * mm, "end": v(-10.55, -51.8) * mm});
            skLineSegment(sketch, "E406", {"start": v(-10.55, -51.8) * mm, "end": v(-10.59, -51.84) * mm});
            skLineSegment(sketch, "E407", {"start": v(-10.59, -51.84) * mm, "end": v(-10.63, -51.89) * mm});
            skLineSegment(sketch, "E408", {"start": v(-10.63, -51.89) * mm, "end": v(-10.67, -51.93) * mm});
            skLineSegment(sketch, "E409", {"start": v(-10.67, -51.93) * mm, "end": v(-10.72, -51.98) * mm});
            skLineSegment(sketch, "E410", {"start": v(-10.72, -51.98) * mm, "end": v(-10.76, -52.03) * mm});
            skLineSegment(sketch, "E411", {"start": v(-10.76, -52.03) * mm, "end": v(-10.81, -52.09) * mm});
            skLineSegment(sketch, "E412", {"start": v(-10.81, -52.09) * mm, "end": v(-10.86, -52.14) * mm});
            skLineSegment(sketch, "E413", {"start": v(-10.86, -52.14) * mm, "end": v(-10.91, -52.2) * mm});
            skLineSegment(sketch, "E414", {"start": v(-10.91, -52.2) * mm, "end": v(-10.96, -52.27) * mm});
            skLineSegment(sketch, "E415", {"start": v(-10.96, -52.27) * mm, "end": v(-11.02, -52.34) * mm});
            skLineSegment(sketch, "E416", {"start": v(-11.02, -52.34) * mm, "end": v(-11.07, -52.4) * mm});
            skLineSegment(sketch, "E417", {"start": v(-11.07, -52.4) * mm, "end": v(-11.12, -52.48) * mm});
            skLineSegment(sketch, "E418", {"start": v(-11.12, -52.48) * mm, "end": v(-11.18, -52.56) * mm});
            skLineSegment(sketch, "E419", {"start": v(-11.18, -52.56) * mm, "end": v(-11.22, -52.61) * mm});
            skLineSegment(sketch, "E420", {"start": v(-11.22, -52.61) * mm, "end": v(-11.09, -52.87) * mm});
            skLineSegment(sketch, "E421", {"start": v(-11.09, -52.87) * mm, "end": v(-10.92, -53.1) * mm});
            skLineSegment(sketch, "E422", {"start": v(-10.92, -53.1) * mm, "end": v(-10.86, -53.09) * mm});
            skLineSegment(sketch, "E423", {"start": v(-10.86, -53.09) * mm, "end": v(-10.76, -53.08) * mm});
            skLineSegment(sketch, "E424", {"start": v(-10.76, -53.08) * mm, "end": v(-10.67, -53.06) * mm});
            skLineSegment(sketch, "E425", {"start": v(-10.67, -53.06) * mm, "end": v(-10.58, -53.05) * mm});
            skLineSegment(sketch, "E426", {"start": v(-10.58, -53.05) * mm, "end": v(-10.5, -53.03) * mm});
            skLineSegment(sketch, "E427", {"start": v(-10.5, -53.03) * mm, "end": v(-10.42, -53.01) * mm});
            skLineSegment(sketch, "E428", {"start": v(-10.42, -53.01) * mm, "end": v(-10.34, -53) * mm});
            skLineSegment(sketch, "E429", {"start": v(-10.34, -53) * mm, "end": v(-10.27, -52.98) * mm});
            skLineSegment(sketch, "E430", {"start": v(-10.27, -52.98) * mm, "end": v(-10.2, -52.96) * mm});
            skLineSegment(sketch, "E431", {"start": v(-10.2, -52.96) * mm, "end": v(-10.13, -52.94) * mm});
            skLineSegment(sketch, "E432", {"start": v(-10.13, -52.94) * mm, "end": v(-10.07, -52.92) * mm});
            skLineSegment(sketch, "E433", {"start": v(-10.07, -52.92) * mm, "end": v(-10, -52.9) * mm});
            skLineSegment(sketch, "E434", {"start": v(-10, -52.9) * mm, "end": v(-9.95, -52.89) * mm});
            skLineSegment(sketch, "E435", {"start": v(-9.95, -52.89) * mm, "end": v(-9.9, -52.87) * mm});
            skLineSegment(sketch, "E436", {"start": v(-9.9, -52.87) * mm, "end": v(-9.85, -52.85) * mm});
            skLineSegment(sketch, "E437", {"start": v(-9.85, -52.85) * mm, "end": v(-9.8, -52.83) * mm});
            skLineSegment(sketch, "E438", {"start": v(-9.8, -52.83) * mm, "end": v(-9.76, -52.81) * mm});
            skLineSegment(sketch, "E439", {"start": v(-9.76, -52.81) * mm, "end": v(-9.72, -52.8) * mm});
            skLineSegment(sketch, "E440", {"start": v(-9.72, -52.8) * mm, "end": v(-9.68, -52.78) * mm});
            skLineSegment(sketch, "E441", {"start": v(-9.68, -52.78) * mm, "end": v(-9.66, -52.77) * mm});
            skLineSegment(sketch, "E442", {"start": v(-9.66, -52.77) * mm, "end": v(-9.63, -52.76) * mm});
            skLineSegment(sketch, "E443", {"start": v(-9.63, -52.76) * mm, "end": v(-9.6, -52.75) * mm});
            skLineSegment(sketch, "E444", {"start": v(-9.6, -52.75) * mm, "end": v(-9.58, -52.74) * mm});
            skLineSegment(sketch, "E445", {"start": v(-9.58, -52.74) * mm, "end": v(-9.56, -52.74) * mm});
            skLineSegment(sketch, "E446", {"start": v(-9.56, -52.74) * mm, "end": v(-9.54, -52.74) * mm});
            skLineSegment(sketch, "E447", {"start": v(-9.54, -52.74) * mm, "end": v(-9.52, -52.74) * mm});
            skLineSegment(sketch, "E448", {"start": v(-9.52, -52.74) * mm, "end": v(-9.5, -52.74) * mm});
            skLineSegment(sketch, "E449", {"start": v(-9.5, -52.74) * mm, "end": v(-9.5, -52.75) * mm});
            skLineSegment(sketch, "E450", {"start": v(-9.5, -52.75) * mm, "end": v(-9.48, -52.75) * mm});
            skLineSegment(sketch, "E451", {"start": v(-9.48, -52.75) * mm, "end": v(-9.37, -52.91) * mm});
            skLineSegment(sketch, "E452", {"start": v(-9.37, -52.91) * mm, "end": v(-9.25, -53.08) * mm});
            skLineSegment(sketch, "E453", {"start": v(-9.25, -53.08) * mm, "end": v(-9.13, -53.24) * mm});
            skLineSegment(sketch, "E454", {"start": v(-9.13, -53.24) * mm, "end": v(-9.13, -53.25) * mm});
            skLineSegment(sketch, "E455", {"start": v(-9.13, -53.25) * mm, "end": v(-9.12, -53.26) * mm});
            skLineSegment(sketch, "E456", {"start": v(-9.12, -53.26) * mm, "end": v(-9.13, -53.28) * mm});
            skLineSegment(sketch, "E457", {"start": v(-9.13, -53.28) * mm, "end": v(-9.13, -53.3) * mm});
            skLineSegment(sketch, "E458", {"start": v(-9.13, -53.3) * mm, "end": v(-9.14, -53.31) * mm});
            skLineSegment(sketch, "E459", {"start": v(-9.14, -53.31) * mm, "end": v(-9.15, -53.33) * mm});
            skLineSegment(sketch, "E460", {"start": v(-9.15, -53.33) * mm, "end": v(-9.17, -53.36) * mm});
            skLineSegment(sketch, "E461", {"start": v(-9.17, -53.36) * mm, "end": v(-9.18, -53.38) * mm});
            skLineSegment(sketch, "E462", {"start": v(-9.18, -53.38) * mm, "end": v(-9.2, -53.4) * mm});
            skLineSegment(sketch, "E463", {"start": v(-9.2, -53.4) * mm, "end": v(-9.22, -53.42) * mm});
            skLineSegment(sketch, "E464", {"start": v(-9.22, -53.42) * mm, "end": v(-9.24, -53.45) * mm});
            skLineSegment(sketch, "E465", {"start": v(-9.24, -53.45) * mm, "end": v(-9.27, -53.48) * mm});
            skLineSegment(sketch, "E466", {"start": v(-9.27, -53.48) * mm, "end": v(-9.3, -53.52) * mm});
            skLineSegment(sketch, "E467", {"start": v(-9.3, -53.52) * mm, "end": v(-9.33, -53.56) * mm});
            skLineSegment(sketch, "E468", {"start": v(-9.33, -53.56) * mm, "end": v(-9.37, -53.6) * mm});
            skLineSegment(sketch, "E469", {"start": v(-9.37, -53.6) * mm, "end": v(-9.4, -53.64) * mm});
            skLineSegment(sketch, "E470", {"start": v(-9.4, -53.64) * mm, "end": v(-9.43, -53.7) * mm});
            skLineSegment(sketch, "E471", {"start": v(-9.43, -53.7) * mm, "end": v(-9.47, -53.74) * mm});
            skLineSegment(sketch, "E472", {"start": v(-9.47, -53.74) * mm, "end": v(-9.5, -53.8) * mm});
            skLineSegment(sketch, "E473", {"start": v(-9.5, -53.8) * mm, "end": v(-9.55, -53.85) * mm});
            skLineSegment(sketch, "E474", {"start": v(-9.55, -53.85) * mm, "end": v(-9.59, -53.92) * mm});
            skLineSegment(sketch, "E475", {"start": v(-9.59, -53.92) * mm, "end": v(-9.62, -53.98) * mm});
            skLineSegment(sketch, "E476", {"start": v(-9.62, -53.98) * mm, "end": v(-9.67, -54.05) * mm});
            skLineSegment(sketch, "E477", {"start": v(-9.67, -54.05) * mm, "end": v(-9.7, -54.12) * mm});
            skLineSegment(sketch, "E478", {"start": v(-9.7, -54.12) * mm, "end": v(-9.75, -54.2) * mm});
            skLineSegment(sketch, "E479", {"start": v(-9.75, -54.2) * mm, "end": v(-9.79, -54.27) * mm});
            skLineSegment(sketch, "E480", {"start": v(-9.79, -54.27) * mm, "end": v(-9.83, -54.36) * mm});
            skLineSegment(sketch, "E481", {"start": v(-9.83, -54.36) * mm, "end": v(-9.87, -54.44) * mm});
            skLineSegment(sketch, "E482", {"start": v(-9.87, -54.44) * mm, "end": v(-9.9, -54.5) * mm});
            skLineSegment(sketch, "E483", {"start": v(-9.9, -54.5) * mm, "end": v(-9.73, -54.73) * mm});
            skLineSegment(sketch, "E484", {"start": v(-9.73, -54.73) * mm, "end": v(-9.53, -54.93) * mm});
            skLineSegment(sketch, "E485", {"start": v(-9.53, -54.93) * mm, "end": v(-9.47, -54.91) * mm});
            skLineSegment(sketch, "E486", {"start": v(-9.47, -54.91) * mm, "end": v(-9.38, -54.88) * mm});
            skLineSegment(sketch, "E487", {"start": v(-9.38, -54.88) * mm, "end": v(-9.3, -54.86) * mm});
            skLineSegment(sketch, "E488", {"start": v(-9.3, -54.86) * mm, "end": v(-9.2, -54.83) * mm});
            skLineSegment(sketch, "E489", {"start": v(-9.2, -54.83) * mm, "end": v(-9.13, -54.8) * mm});
            skLineSegment(sketch, "E490", {"start": v(-9.13, -54.8) * mm, "end": v(-9.05, -54.77) * mm});
            skLineSegment(sketch, "E491", {"start": v(-9.05, -54.77) * mm, "end": v(-8.98, -54.74) * mm});
            skLineSegment(sketch, "E492", {"start": v(-8.98, -54.74) * mm, "end": v(-8.9, -54.71) * mm});
            skLineSegment(sketch, "E493", {"start": v(-8.9, -54.71) * mm, "end": v(-8.84, -54.68) * mm});
            skLineSegment(sketch, "E494", {"start": v(-8.84, -54.68) * mm, "end": v(-8.78, -54.65) * mm});
            skLineSegment(sketch, "E495", {"start": v(-8.78, -54.65) * mm, "end": v(-8.72, -54.63) * mm});
            skLineSegment(sketch, "E496", {"start": v(-8.72, -54.63) * mm, "end": v(-8.66, -54.6) * mm});
            skLineSegment(sketch, "E497", {"start": v(-8.66, -54.6) * mm, "end": v(-8.6, -54.57) * mm});
            skLineSegment(sketch, "E498", {"start": v(-8.6, -54.57) * mm, "end": v(-8.56, -54.54) * mm});
            skLineSegment(sketch, "E499", {"start": v(-8.56, -54.54) * mm, "end": v(-8.51, -54.52) * mm});
            skLineSegment(sketch, "E500", {"start": v(-8.51, -54.52) * mm, "end": v(-8.47, -54.5) * mm});
            skLineSegment(sketch, "E501", {"start": v(-8.47, -54.5) * mm, "end": v(-8.43, -54.47) * mm});
            skLineSegment(sketch, "E502", {"start": v(-8.43, -54.47) * mm, "end": v(-8.4, -54.45) * mm});
            skLineSegment(sketch, "E503", {"start": v(-8.4, -54.45) * mm, "end": v(-8.36, -54.43) * mm});
            skLineSegment(sketch, "E504", {"start": v(-8.36, -54.43) * mm, "end": v(-8.34, -54.42) * mm});
            skLineSegment(sketch, "E505", {"start": v(-8.34, -54.42) * mm, "end": v(-8.31, -54.4) * mm});
            skLineSegment(sketch, "E506", {"start": v(-8.31, -54.4) * mm, "end": v(-8.29, -54.38) * mm});
            skLineSegment(sketch, "E507", {"start": v(-8.29, -54.38) * mm, "end": v(-8.26, -54.37) * mm});
            skLineSegment(sketch, "E508", {"start": v(-8.26, -54.37) * mm, "end": v(-8.24, -54.36) * mm});
            skLineSegment(sketch, "E509", {"start": v(-8.24, -54.36) * mm, "end": v(-8.22, -54.36) * mm});
            skLineSegment(sketch, "E510", {"start": v(-8.22, -54.36) * mm, "end": v(-8.2, -54.36) * mm});
            skLineSegment(sketch, "E511", {"start": v(-8.2, -54.36) * mm, "end": v(-8.19, -54.36) * mm});
            skLineSegment(sketch, "E512", {"start": v(-8.19, -54.36) * mm, "end": v(-8.18, -54.36) * mm});
            skLineSegment(sketch, "E513", {"start": v(-8.18, -54.36) * mm, "end": v(-8.17, -54.37) * mm});
            skLineSegment(sketch, "E514", {"start": v(-8.17, -54.37) * mm, "end": v(-8.03, -54.5) * mm});
            skLineSegment(sketch, "E515", {"start": v(-8.03, -54.5) * mm, "end": v(-7.88, -54.65) * mm});
            skLineSegment(sketch, "E516", {"start": v(-7.88, -54.65) * mm, "end": v(-7.74, -54.8) * mm});
            skLineSegment(sketch, "E517", {"start": v(-7.74, -54.8) * mm, "end": v(-7.74, -54.8) * mm});
            skLineSegment(sketch, "E518", {"start": v(-7.74, -54.8) * mm, "end": v(-7.73, -54.81) * mm});
            skLineSegment(sketch, "E519", {"start": v(-7.73, -54.81) * mm, "end": v(-7.73, -54.83) * mm});
            skLineSegment(sketch, "E520", {"start": v(-7.73, -54.83) * mm, "end": v(-7.73, -54.85) * mm});
            skLineSegment(sketch, "E521", {"start": v(-7.73, -54.85) * mm, "end": v(-7.74, -54.87) * mm});
            skLineSegment(sketch, "E522", {"start": v(-7.74, -54.87) * mm, "end": v(-7.75, -54.89) * mm});
            skLineSegment(sketch, "E523", {"start": v(-7.75, -54.89) * mm, "end": v(-7.76, -54.91) * mm});
            skLineSegment(sketch, "E524", {"start": v(-7.76, -54.91) * mm, "end": v(-7.77, -54.94) * mm});
            skLineSegment(sketch, "E525", {"start": v(-7.77, -54.94) * mm, "end": v(-7.8, -54.97) * mm});
            skLineSegment(sketch, "E526", {"start": v(-7.8, -54.97) * mm, "end": v(-7.8, -54.98) * mm});
            skLineSegment(sketch, "E527", {"start": v(-7.8, -54.98) * mm, "end": v(-7.82, -55.02) * mm});
            skLineSegment(sketch, "E528", {"start": v(-7.82, -55.02) * mm, "end": v(-7.85, -55.05) * mm});
            skLineSegment(sketch, "E529", {"start": v(-7.85, -55.05) * mm, "end": v(-7.87, -55.1) * mm});
            skLineSegment(sketch, "E530", {"start": v(-7.87, -55.1) * mm, "end": v(-7.9, -55.14) * mm});
            skLineSegment(sketch, "E531", {"start": v(-7.9, -55.14) * mm, "end": v(-7.92, -55.18) * mm});
            skLineSegment(sketch, "E532", {"start": v(-7.92, -55.18) * mm, "end": v(-7.95, -55.23) * mm});
            skLineSegment(sketch, "E533", {"start": v(-7.95, -55.23) * mm, "end": v(-7.97, -55.28) * mm});
            skLineSegment(sketch, "E534", {"start": v(-7.97, -55.28) * mm, "end": v(-8, -55.34) * mm});
            skLineSegment(sketch, "E535", {"start": v(-8, -55.34) * mm, "end": v(-8.03, -55.4) * mm});
            skLineSegment(sketch, "E536", {"start": v(-8.03, -55.4) * mm, "end": v(-8.06, -55.46) * mm});
            skLineSegment(sketch, "E537", {"start": v(-8.06, -55.46) * mm, "end": v(-8.09, -55.53) * mm});
            skLineSegment(sketch, "E538", {"start": v(-8.09, -55.53) * mm, "end": v(-8.12, -55.6) * mm});
            skLineSegment(sketch, "E539", {"start": v(-8.12, -55.6) * mm, "end": v(-8.14, -55.67) * mm});
            skLineSegment(sketch, "E540", {"start": v(-8.14, -55.67) * mm, "end": v(-8.17, -55.75) * mm});
            skLineSegment(sketch, "E541", {"start": v(-8.17, -55.75) * mm, "end": v(-8.2, -55.83) * mm});
            skLineSegment(sketch, "E542", {"start": v(-8.2, -55.83) * mm, "end": v(-8.23, -55.92) * mm});
            skLineSegment(sketch, "E543", {"start": v(-8.23, -55.92) * mm, "end": v(-8.26, -56) * mm});
            skLineSegment(sketch, "E544", {"start": v(-8.26, -56) * mm, "end": v(-8.29, -56.1) * mm});
            skLineSegment(sketch, "E545", {"start": v(-8.29, -56.1) * mm, "end": v(-8.3, -56.16) * mm});
            skLineSegment(sketch, "E546", {"start": v(-8.3, -56.16) * mm, "end": v(-8.1, -56.36) * mm});
            skLineSegment(sketch, "E547", {"start": v(-8.1, -56.36) * mm, "end": v(-7.87, -56.52) * mm});
            skLineSegment(sketch, "E548", {"start": v(-7.87, -56.52) * mm, "end": v(-7.82, -56.5) * mm});
            skLineSegment(sketch, "E549", {"start": v(-7.82, -56.5) * mm, "end": v(-7.73, -56.46) * mm});
            skLineSegment(sketch, "E550", {"start": v(-7.73, -56.46) * mm, "end": v(-7.65, -56.41) * mm});
            skLineSegment(sketch, "E551", {"start": v(-7.65, -56.41) * mm, "end": v(-7.57, -56.37) * mm});
            skLineSegment(sketch, "E552", {"start": v(-7.57, -56.37) * mm, "end": v(-7.5, -56.33) * mm});
            skLineSegment(sketch, "E553", {"start": v(-7.5, -56.33) * mm, "end": v(-7.42, -56.29) * mm});
            skLineSegment(sketch, "E554", {"start": v(-7.42, -56.29) * mm, "end": v(-7.36, -56.25) * mm});
            skLineSegment(sketch, "E555", {"start": v(-7.36, -56.25) * mm, "end": v(-7.3, -56.2) * mm});
            skLineSegment(sketch, "E556", {"start": v(-7.3, -56.2) * mm, "end": v(-7.23, -56.17) * mm});
            skLineSegment(sketch, "E557", {"start": v(-7.23, -56.17) * mm, "end": v(-7.17, -56.13) * mm});
            skLineSegment(sketch, "E558", {"start": v(-7.17, -56.13) * mm, "end": v(-7.12, -56.1) * mm});
            skLineSegment(sketch, "E559", {"start": v(-7.12, -56.1) * mm, "end": v(-7.07, -56.06) * mm});
            skLineSegment(sketch, "E560", {"start": v(-7.07, -56.06) * mm, "end": v(-7.02, -56.02) * mm});
            skLineSegment(sketch, "E561", {"start": v(-7.02, -56.02) * mm, "end": v(-6.97, -56) * mm});
            skLineSegment(sketch, "E562", {"start": v(-6.97, -56) * mm, "end": v(-6.93, -55.96) * mm});
            skLineSegment(sketch, "E563", {"start": v(-6.93, -55.96) * mm, "end": v(-6.9, -55.93) * mm});
            skLineSegment(sketch, "E564", {"start": v(-6.9, -55.93) * mm, "end": v(-6.86, -55.9) * mm});
            skLineSegment(sketch, "E565", {"start": v(-6.86, -55.9) * mm, "end": v(-6.82, -55.87) * mm});
            skLineSegment(sketch, "E566", {"start": v(-6.82, -55.87) * mm, "end": v(-6.8, -55.84) * mm});
            skLineSegment(sketch, "E567", {"start": v(-6.8, -55.84) * mm, "end": v(-6.78, -55.83) * mm});
            skLineSegment(sketch, "E568", {"start": v(-6.78, -55.83) * mm, "end": v(-6.75, -55.8) * mm});
            skLineSegment(sketch, "E569", {"start": v(-6.75, -55.8) * mm, "end": v(-6.73, -55.8) * mm});
            skLineSegment(sketch, "E570", {"start": v(-6.73, -55.8) * mm, "end": v(-6.7, -55.78) * mm});
            skLineSegment(sketch, "E571", {"start": v(-6.7, -55.78) * mm, "end": v(-6.69, -55.76) * mm});
            skLineSegment(sketch, "E572", {"start": v(-6.69, -55.76) * mm, "end": v(-6.67, -55.76) * mm});
            skLineSegment(sketch, "E573", {"start": v(-6.67, -55.76) * mm, "end": v(-6.65, -55.75) * mm});
            skLineSegment(sketch, "E574", {"start": v(-6.65, -55.75) * mm, "end": v(-6.64, -55.75) * mm});
            skLineSegment(sketch, "E575", {"start": v(-6.64, -55.75) * mm, "end": v(-6.63, -55.75) * mm});
            skLineSegment(sketch, "E576", {"start": v(-6.63, -55.75) * mm, "end": v(-6.61, -55.75) * mm});
            skLineSegment(sketch, "E577", {"start": v(-6.61, -55.75) * mm, "end": v(-6.46, -55.87) * mm});
            skLineSegment(sketch, "E578", {"start": v(-6.46, -55.87) * mm, "end": v(-6.29, -56) * mm});
            skLineSegment(sketch, "E579", {"start": v(-6.29, -56) * mm, "end": v(-6.13, -56.1) * mm});
            skLineSegment(sketch, "E580", {"start": v(-6.13, -56.1) * mm, "end": v(-6.12, -56.12) * mm});
            skLineSegment(sketch, "E581", {"start": v(-6.12, -56.12) * mm, "end": v(-6.12, -56.13) * mm});
            skLineSegment(sketch, "E582", {"start": v(-6.12, -56.13) * mm, "end": v(-6.11, -56.14) * mm});
            skLineSegment(sketch, "E583", {"start": v(-6.11, -56.14) * mm, "end": v(-6.11, -56.16) * mm});
            skLineSegment(sketch, "E584", {"start": v(-6.11, -56.16) * mm, "end": v(-6.12, -56.18) * mm});
            skLineSegment(sketch, "E585", {"start": v(-6.12, -56.18) * mm, "end": v(-6.12, -56.2) * mm});
            skLineSegment(sketch, "E586", {"start": v(-6.12, -56.2) * mm, "end": v(-6.13, -56.23) * mm});
            skLineSegment(sketch, "E587", {"start": v(-6.13, -56.23) * mm, "end": v(-6.14, -56.26) * mm});
            skLineSegment(sketch, "E588", {"start": v(-6.14, -56.26) * mm, "end": v(-6.15, -56.29) * mm});
            skLineSegment(sketch, "E589", {"start": v(-6.15, -56.29) * mm, "end": v(-6.16, -56.3) * mm});
            skLineSegment(sketch, "E590", {"start": v(-6.16, -56.3) * mm, "end": v(-6.17, -56.34) * mm});
            skLineSegment(sketch, "E591", {"start": v(-6.17, -56.34) * mm, "end": v(-6.2, -56.38) * mm});
            skLineSegment(sketch, "E592", {"start": v(-6.2, -56.38) * mm, "end": v(-6.2, -56.42) * mm});
            skLineSegment(sketch, "E593", {"start": v(-6.2, -56.42) * mm, "end": v(-6.23, -56.47) * mm});
            skLineSegment(sketch, "E594", {"start": v(-6.23, -56.47) * mm, "end": v(-6.24, -56.52) * mm});
            skLineSegment(sketch, "E595", {"start": v(-6.24, -56.52) * mm, "end": v(-6.26, -56.57) * mm});
            skLineSegment(sketch, "E596", {"start": v(-6.26, -56.57) * mm, "end": v(-6.28, -56.63) * mm});
            skLineSegment(sketch, "E597", {"start": v(-6.28, -56.63) * mm, "end": v(-6.3, -56.7) * mm});
            skLineSegment(sketch, "E598", {"start": v(-6.3, -56.7) * mm, "end": v(-6.32, -56.75) * mm});
            skLineSegment(sketch, "E599", {"start": v(-6.32, -56.75) * mm, "end": v(-6.33, -56.82) * mm});
            skLineSegment(sketch, "E600", {"start": v(-6.33, -56.82) * mm, "end": v(-6.35, -56.9) * mm});
            skLineSegment(sketch, "E601", {"start": v(-6.35, -56.9) * mm, "end": v(-6.37, -56.96) * mm});
            skLineSegment(sketch, "E602", {"start": v(-6.37, -56.96) * mm, "end": v(-6.39, -57.04) * mm});
            skLineSegment(sketch, "E603", {"start": v(-6.39, -57.04) * mm, "end": v(-6.4, -57.12) * mm});
            skLineSegment(sketch, "E604", {"start": v(-6.4, -57.12) * mm, "end": v(-6.42, -57.2) * mm});
            skLineSegment(sketch, "E605", {"start": v(-6.42, -57.2) * mm, "end": v(-6.44, -57.3) * mm});
            skLineSegment(sketch, "E606", {"start": v(-6.44, -57.3) * mm, "end": v(-6.45, -57.39) * mm});
            skLineSegment(sketch, "E607", {"start": v(-6.45, -57.39) * mm, "end": v(-6.46, -57.48) * mm});
            skLineSegment(sketch, "E608", {"start": v(-6.46, -57.48) * mm, "end": v(-6.47, -57.54) * mm});
            skLineSegment(sketch, "E609", {"start": v(-6.47, -57.54) * mm, "end": v(-6.24, -57.71) * mm});
            skLineSegment(sketch, "E610", {"start": v(-6.24, -57.71) * mm, "end": v(-5.99, -57.84) * mm});
            skLineSegment(sketch, "E611", {"start": v(-5.99, -57.84) * mm, "end": v(-5.94, -57.8) * mm});
            skLineSegment(sketch, "E612", {"start": v(-5.94, -57.8) * mm, "end": v(-5.86, -57.75) * mm});
            skLineSegment(sketch, "E613", {"start": v(-5.86, -57.75) * mm, "end": v(-5.78, -57.7) * mm});
            skLineSegment(sketch, "E614", {"start": v(-5.78, -57.7) * mm, "end": v(-5.71, -57.64) * mm});
            skLineSegment(sketch, "E615", {"start": v(-5.71, -57.64) * mm, "end": v(-5.64, -57.59) * mm});
            skLineSegment(sketch, "E616", {"start": v(-5.64, -57.59) * mm, "end": v(-5.58, -57.54) * mm});
            skLineSegment(sketch, "E617", {"start": v(-5.58, -57.54) * mm, "end": v(-5.52, -57.49) * mm});
            skLineSegment(sketch, "E618", {"start": v(-5.52, -57.49) * mm, "end": v(-5.46, -57.44) * mm});
            skLineSegment(sketch, "E619", {"start": v(-5.46, -57.44) * mm, "end": v(-5.4, -57.39) * mm});
            skLineSegment(sketch, "E620", {"start": v(-5.4, -57.39) * mm, "end": v(-5.36, -57.34) * mm});
            skLineSegment(sketch, "E621", {"start": v(-5.36, -57.34) * mm, "end": v(-5.3, -57.3) * mm});
            skLineSegment(sketch, "E622", {"start": v(-5.3, -57.3) * mm, "end": v(-5.26, -57.25) * mm});
            skLineSegment(sketch, "E623", {"start": v(-5.26, -57.25) * mm, "end": v(-5.22, -57.21) * mm});
            skLineSegment(sketch, "E624", {"start": v(-5.22, -57.21) * mm, "end": v(-5.18, -57.17) * mm});
            skLineSegment(sketch, "E625", {"start": v(-5.18, -57.17) * mm, "end": v(-5.14, -57.13) * mm});
            skLineSegment(sketch, "E626", {"start": v(-5.14, -57.13) * mm, "end": v(-5.11, -57.1) * mm});
            skLineSegment(sketch, "E627", {"start": v(-5.11, -57.1) * mm, "end": v(-5.08, -57.06) * mm});
            skLineSegment(sketch, "E628", {"start": v(-5.08, -57.06) * mm, "end": v(-5.05, -57.03) * mm});
            skLineSegment(sketch, "E629", {"start": v(-5.05, -57.03) * mm, "end": v(-5.03, -57) * mm});
            skLineSegment(sketch, "E630", {"start": v(-5.03, -57) * mm, "end": v(-5.01, -56.98) * mm});
            skLineSegment(sketch, "E631", {"start": v(-5.01, -56.98) * mm, "end": v(-5, -56.96) * mm});
            skLineSegment(sketch, "E632", {"start": v(-5, -56.96) * mm, "end": v(-4.97, -56.94) * mm});
            skLineSegment(sketch, "E633", {"start": v(-4.97, -56.94) * mm, "end": v(-4.95, -56.92) * mm});
            skLineSegment(sketch, "E634", {"start": v(-4.95, -56.92) * mm, "end": v(-4.94, -56.9) * mm});
            skLineSegment(sketch, "E635", {"start": v(-4.94, -56.9) * mm, "end": v(-4.92, -56.9) * mm});
            skLineSegment(sketch, "E636", {"start": v(-4.92, -56.9) * mm, "end": v(-4.9, -56.88) * mm});
            skLineSegment(sketch, "E637", {"start": v(-4.9, -56.88) * mm, "end": v(-4.89, -56.88) * mm});
            skLineSegment(sketch, "E638", {"start": v(-4.89, -56.88) * mm, "end": v(-4.88, -56.88) * mm});
            skLineSegment(sketch, "E639", {"start": v(-4.88, -56.88) * mm, "end": v(-4.86, -56.88) * mm});
            skLineSegment(sketch, "E640", {"start": v(-4.86, -56.88) * mm, "end": v(-4.7, -56.97) * mm});
            skLineSegment(sketch, "E641", {"start": v(-4.7, -56.97) * mm, "end": v(-4.5, -57.07) * mm});
            skLineSegment(sketch, "E642", {"start": v(-4.5, -57.07) * mm, "end": v(-4.33, -57.15) * mm});
            skLineSegment(sketch, "E643", {"start": v(-4.33, -57.15) * mm, "end": v(-4.32, -57.16) * mm});
            skLineSegment(sketch, "E644", {"start": v(-4.32, -57.16) * mm, "end": v(-4.31, -57.17) * mm});
            skLineSegment(sketch, "E645", {"start": v(-4.31, -57.17) * mm, "end": v(-4.3, -57.19) * mm});
            skLineSegment(sketch, "E646", {"start": v(-4.3, -57.19) * mm, "end": v(-4.3, -57.2) * mm});
            skLineSegment(sketch, "E647", {"start": v(-4.3, -57.2) * mm, "end": v(-4.3, -57.22) * mm});
            skLineSegment(sketch, "E648", {"start": v(-4.3, -57.22) * mm, "end": v(-4.3, -57.25) * mm});
            skLineSegment(sketch, "E649", {"start": v(-4.3, -57.25) * mm, "end": v(-4.3, -57.27) * mm});
            skLineSegment(sketch, "E650", {"start": v(-4.3, -57.27) * mm, "end": v(-4.31, -57.3) * mm});
            skLineSegment(sketch, "E651", {"start": v(-4.31, -57.3) * mm, "end": v(-4.32, -57.33) * mm});
            skLineSegment(sketch, "E652", {"start": v(-4.32, -57.33) * mm, "end": v(-4.33, -57.35) * mm});
            skLineSegment(sketch, "E653", {"start": v(-4.33, -57.35) * mm, "end": v(-4.34, -57.4) * mm});
            skLineSegment(sketch, "E654", {"start": v(-4.34, -57.4) * mm, "end": v(-4.35, -57.43) * mm});
            skLineSegment(sketch, "E655", {"start": v(-4.35, -57.43) * mm, "end": v(-4.36, -57.48) * mm});
            skLineSegment(sketch, "E656", {"start": v(-4.36, -57.48) * mm, "end": v(-4.37, -57.53) * mm});
            skLineSegment(sketch, "E657", {"start": v(-4.37, -57.53) * mm, "end": v(-4.38, -57.58) * mm});
            skLineSegment(sketch, "E658", {"start": v(-4.38, -57.58) * mm, "end": v(-4.39, -57.64) * mm});
            skLineSegment(sketch, "E659", {"start": v(-4.39, -57.64) * mm, "end": v(-4.4, -57.7) * mm});
            skLineSegment(sketch, "E660", {"start": v(-4.4, -57.7) * mm, "end": v(-4.4, -57.76) * mm});
            skLineSegment(sketch, "E661", {"start": v(-4.4, -57.76) * mm, "end": v(-4.41, -57.82) * mm});
            skLineSegment(sketch, "E662", {"start": v(-4.41, -57.82) * mm, "end": v(-4.42, -57.9) * mm});
            skLineSegment(sketch, "E663", {"start": v(-4.42, -57.9) * mm, "end": v(-4.43, -57.96) * mm});
            skLineSegment(sketch, "E664", {"start": v(-4.43, -57.96) * mm, "end": v(-4.43, -58.04) * mm});
            skLineSegment(sketch, "E665", {"start": v(-4.43, -58.04) * mm, "end": v(-4.44, -58.12) * mm});
            skLineSegment(sketch, "E666", {"start": v(-4.44, -58.12) * mm, "end": v(-4.44, -58.2) * mm});
            skLineSegment(sketch, "E667", {"start": v(-4.44, -58.2) * mm, "end": v(-4.45, -58.29) * mm});
            skLineSegment(sketch, "E668", {"start": v(-4.45, -58.29) * mm, "end": v(-4.45, -58.38) * mm});
            skLineSegment(sketch, "E669", {"start": v(-4.45, -58.38) * mm, "end": v(-4.45, -58.47) * mm});
            skLineSegment(sketch, "E670", {"start": v(-4.45, -58.47) * mm, "end": v(-4.45, -58.56) * mm});
            skLineSegment(sketch, "E671", {"start": v(-4.45, -58.56) * mm, "end": v(-4.44, -58.63) * mm});
            skLineSegment(sketch, "E672", {"start": v(-4.44, -58.63) * mm, "end": v(-4.2, -58.76) * mm});
            skLineSegment(sketch, "E673", {"start": v(-4.2, -58.76) * mm, "end": v(-3.92, -58.84) * mm});
            skLineSegment(sketch, "E674", {"start": v(-3.92, -58.84) * mm, "end": v(-3.87, -58.8) * mm});
            skLineSegment(sketch, "E675", {"start": v(-3.87, -58.8) * mm, "end": v(-3.8, -58.73) * mm});
            skLineSegment(sketch, "E676", {"start": v(-3.8, -58.73) * mm, "end": v(-3.74, -58.67) * mm});
            skLineSegment(sketch, "E677", {"start": v(-3.74, -58.67) * mm, "end": v(-3.68, -58.6) * mm});
            skLineSegment(sketch, "E678", {"start": v(-3.68, -58.6) * mm, "end": v(-3.62, -58.54) * mm});
            skLineSegment(sketch, "E679", {"start": v(-3.62, -58.54) * mm, "end": v(-3.56, -58.48) * mm});
            skLineSegment(sketch, "E680", {"start": v(-3.56, -58.48) * mm, "end": v(-3.51, -58.42) * mm});
            skLineSegment(sketch, "E681", {"start": v(-3.51, -58.42) * mm, "end": v(-3.46, -58.36) * mm});
            skLineSegment(sketch, "E682", {"start": v(-3.46, -58.36) * mm, "end": v(-3.42, -58.3) * mm});
            skLineSegment(sketch, "E683", {"start": v(-3.42, -58.3) * mm, "end": v(-3.37, -58.25) * mm});
            skLineSegment(sketch, "E684", {"start": v(-3.37, -58.25) * mm, "end": v(-3.33, -58.2) * mm});
            skLineSegment(sketch, "E685", {"start": v(-3.33, -58.2) * mm, "end": v(-3.3, -58.15) * mm});
            skLineSegment(sketch, "E686", {"start": v(-3.3, -58.15) * mm, "end": v(-3.26, -58.1) * mm});
            skLineSegment(sketch, "E687", {"start": v(-3.26, -58.1) * mm, "end": v(-3.23, -58.06) * mm});
            skLineSegment(sketch, "E688", {"start": v(-3.23, -58.06) * mm, "end": v(-3.2, -58.01) * mm});
            skLineSegment(sketch, "E689", {"start": v(-3.2, -58.01) * mm, "end": v(-3.17, -57.97) * mm});
            skLineSegment(sketch, "E690", {"start": v(-3.17, -57.97) * mm, "end": v(-3.14, -57.93) * mm});
            skLineSegment(sketch, "E691", {"start": v(-3.14, -57.93) * mm, "end": v(-3.12, -57.9) * mm});
            skLineSegment(sketch, "E692", {"start": v(-3.12, -57.9) * mm, "end": v(-3.1, -57.86) * mm});
            skLineSegment(sketch, "E693", {"start": v(-3.1, -57.86) * mm, "end": v(-3.1, -57.84) * mm});
            skLineSegment(sketch, "E694", {"start": v(-3.1, -57.84) * mm, "end": v(-3.08, -57.82) * mm});
            skLineSegment(sketch, "E695", {"start": v(-3.08, -57.82) * mm, "end": v(-3.06, -57.8) * mm});
            skLineSegment(sketch, "E696", {"start": v(-3.06, -57.8) * mm, "end": v(-3.04, -57.77) * mm});
            skLineSegment(sketch, "E697", {"start": v(-3.04, -57.77) * mm, "end": v(-3.03, -57.75) * mm});
            skLineSegment(sketch, "E698", {"start": v(-3.03, -57.75) * mm, "end": v(-3.01, -57.74) * mm});
            skLineSegment(sketch, "E699", {"start": v(-3.01, -57.74) * mm, "end": v(-3, -57.73) * mm});
            skLineSegment(sketch, "E700", {"start": v(-3, -57.73) * mm, "end": v(-2.98, -57.72) * mm});
            skLineSegment(sketch, "E701", {"start": v(-2.98, -57.72) * mm, "end": v(-2.97, -57.72) * mm});
            skLineSegment(sketch, "E702", {"start": v(-2.97, -57.72) * mm, "end": v(-2.96, -57.72) * mm});
            skLineSegment(sketch, "E703", {"start": v(-2.96, -57.72) * mm, "end": v(-2.77, -57.79) * mm});
            skLineSegment(sketch, "E704", {"start": v(-2.77, -57.79) * mm, "end": v(-2.58, -57.85) * mm});
            skLineSegment(sketch, "E705", {"start": v(-2.58, -57.85) * mm, "end": v(-2.39, -57.9) * mm});
            skLineSegment(sketch, "E706", {"start": v(-2.39, -57.9) * mm, "end": v(-2.38, -57.91) * mm});
            skLineSegment(sketch, "E707", {"start": v(-2.38, -57.91) * mm, "end": v(-2.37, -57.92) * mm});
            skLineSegment(sketch, "E708", {"start": v(-2.37, -57.92) * mm, "end": v(-2.36, -57.94) * mm});
            skLineSegment(sketch, "E709", {"start": v(-2.36, -57.94) * mm, "end": v(-2.36, -57.95) * mm});
            skLineSegment(sketch, "E710", {"start": v(-2.36, -57.95) * mm, "end": v(-2.35, -57.97) * mm});
            skLineSegment(sketch, "E711", {"start": v(-2.35, -57.97) * mm, "end": v(-2.35, -58) * mm});
            skLineSegment(sketch, "E712", {"start": v(-2.35, -58) * mm, "end": v(-2.35, -58.02) * mm});
            skLineSegment(sketch, "E713", {"start": v(-2.35, -58.02) * mm, "end": v(-2.35, -58.05) * mm});
            skLineSegment(sketch, "E714", {"start": v(-2.35, -58.05) * mm, "end": v(-2.35, -58.08) * mm});
            skLineSegment(sketch, "E715", {"start": v(-2.35, -58.08) * mm, "end": v(-2.36, -58.1) * mm});
            skLineSegment(sketch, "E716", {"start": v(-2.36, -58.1) * mm, "end": v(-2.36, -58.14) * mm});
            skLineSegment(sketch, "E717", {"start": v(-2.36, -58.14) * mm, "end": v(-2.36, -58.19) * mm});
            skLineSegment(sketch, "E718", {"start": v(-2.36, -58.19) * mm, "end": v(-2.37, -58.23) * mm});
            skLineSegment(sketch, "E719", {"start": v(-2.37, -58.23) * mm, "end": v(-2.37, -58.28) * mm});
            skLineSegment(sketch, "E720", {"start": v(-2.37, -58.28) * mm, "end": v(-2.37, -58.34) * mm});
            skLineSegment(sketch, "E721", {"start": v(-2.37, -58.34) * mm, "end": v(-2.37, -58.4) * mm});
            skLineSegment(sketch, "E722", {"start": v(-2.37, -58.4) * mm, "end": v(-2.37, -58.45) * mm});
            skLineSegment(sketch, "E723", {"start": v(-2.37, -58.45) * mm, "end": v(-2.37, -58.51) * mm});
            skLineSegment(sketch, "E724", {"start": v(-2.37, -58.51) * mm, "end": v(-2.37, -58.58) * mm});
            skLineSegment(sketch, "E725", {"start": v(-2.37, -58.58) * mm, "end": v(-2.36, -58.65) * mm});
            skLineSegment(sketch, "E726", {"start": v(-2.36, -58.65) * mm, "end": v(-2.36, -58.72) * mm});
            skLineSegment(sketch, "E727", {"start": v(-2.36, -58.72) * mm, "end": v(-2.35, -58.8) * mm});
            skLineSegment(sketch, "E728", {"start": v(-2.35, -58.8) * mm, "end": v(-2.35, -58.88) * mm});
            skLineSegment(sketch, "E729", {"start": v(-2.35, -58.88) * mm, "end": v(-2.34, -58.96) * mm});
            skLineSegment(sketch, "E730", {"start": v(-2.34, -58.96) * mm, "end": v(-2.33, -59.04) * mm});
            skLineSegment(sketch, "E731", {"start": v(-2.33, -59.04) * mm, "end": v(-2.31, -59.13) * mm});
            skLineSegment(sketch, "E732", {"start": v(-2.31, -59.13) * mm, "end": v(-2.3, -59.22) * mm});
            skLineSegment(sketch, "E733", {"start": v(-2.3, -59.22) * mm, "end": v(-2.28, -59.32) * mm});
            skLineSegment(sketch, "E734", {"start": v(-2.28, -59.32) * mm, "end": v(-2.27, -59.38) * mm});
            skLineSegment(sketch, "E735", {"start": v(-2.27, -59.38) * mm, "end": v(-2, -59.47) * mm});
            skLineSegment(sketch, "E736", {"start": v(-2, -59.47) * mm, "end": v(-1.72, -59.51) * mm});
            skLineSegment(sketch, "E737", {"start": v(-1.72, -59.51) * mm, "end": v(-1.68, -59.46) * mm});
            skLineSegment(sketch, "E738", {"start": v(-1.68, -59.46) * mm, "end": v(-1.62, -59.39) * mm});
            skLineSegment(sketch, "E739", {"start": v(-1.62, -59.39) * mm, "end": v(-1.57, -59.31) * mm});
            skLineSegment(sketch, "E740", {"start": v(-1.57, -59.31) * mm, "end": v(-1.52, -59.24) * mm});
            skLineSegment(sketch, "E741", {"start": v(-1.52, -59.24) * mm, "end": v(-1.47, -59.17) * mm});
            skLineSegment(sketch, "E742", {"start": v(-1.47, -59.17) * mm, "end": v(-1.42, -59.1) * mm});
            skLineSegment(sketch, "E743", {"start": v(-1.42, -59.1) * mm, "end": v(-1.38, -59.03) * mm});
            skLineSegment(sketch, "E744", {"start": v(-1.38, -59.03) * mm, "end": v(-1.34, -58.97) * mm});
            skLineSegment(sketch, "E745", {"start": v(-1.34, -58.97) * mm, "end": v(-1.3, -58.9) * mm});
            skLineSegment(sketch, "E746", {"start": v(-1.3, -58.9) * mm, "end": v(-1.27, -58.84) * mm});
            skLineSegment(sketch, "E747", {"start": v(-1.27, -58.84) * mm, "end": v(-1.24, -58.79) * mm});
            skLineSegment(sketch, "E748", {"start": v(-1.24, -58.79) * mm, "end": v(-1.21, -58.73) * mm});
            skLineSegment(sketch, "E749", {"start": v(-1.21, -58.73) * mm, "end": v(-1.18, -58.68) * mm});
            skLineSegment(sketch, "E750", {"start": v(-1.18, -58.68) * mm, "end": v(-1.16, -58.63) * mm});
            skLineSegment(sketch, "E751", {"start": v(-1.16, -58.63) * mm, "end": v(-1.14, -58.58) * mm});
            skLineSegment(sketch, "E752", {"start": v(-1.14, -58.58) * mm, "end": v(-1.12, -58.53) * mm});
            skLineSegment(sketch, "E753", {"start": v(-1.12, -58.53) * mm, "end": v(-1.1, -58.5) * mm});
            skLineSegment(sketch, "E754", {"start": v(-1.1, -58.5) * mm, "end": v(-1.08, -58.45) * mm});
            skLineSegment(sketch, "E755", {"start": v(-1.08, -58.45) * mm, "end": v(-1.07, -58.41) * mm});
            skLineSegment(sketch, "E756", {"start": v(-1.07, -58.41) * mm, "end": v(-1.06, -58.4) * mm});
            skLineSegment(sketch, "E757", {"start": v(-1.06, -58.4) * mm, "end": v(-1.05, -58.36) * mm});
            skLineSegment(sketch, "E758", {"start": v(-1.05, -58.36) * mm, "end": v(-1.03, -58.34) * mm});
            skLineSegment(sketch, "E759", {"start": v(-1.03, -58.34) * mm, "end": v(-1.02, -58.32) * mm});
            skLineSegment(sketch, "E760", {"start": v(-1.02, -58.32) * mm, "end": v(-1, -58.3) * mm});
            skLineSegment(sketch, "E761", {"start": v(-1, -58.3) * mm, "end": v(-1, -58.28) * mm});
            skLineSegment(sketch, "E762", {"start": v(-1, -58.28) * mm, "end": v(-0.98, -58.27) * mm});
            skLineSegment(sketch, "E763", {"start": v(-0.98, -58.27) * mm, "end": v(-0.97, -58.26) * mm});
            skLineSegment(sketch, "E764", {"start": v(-0.97, -58.26) * mm, "end": v(-0.96, -58.25) * mm});
            skLineSegment(sketch, "E765", {"start": v(-0.96, -58.25) * mm, "end": v(-0.95, -58.25) * mm});
            skLineSegment(sketch, "E766", {"start": v(-0.95, -58.25) * mm, "end": v(-0.75, -58.29) * mm});
            skLineSegment(sketch, "E767", {"start": v(-0.75, -58.29) * mm, "end": v(-0.55, -58.32) * mm});
            skLineSegment(sketch, "E768", {"start": v(-0.55, -58.32) * mm, "end": v(-0.35, -58.35) * mm});
            skLineSegment(sketch, "E769", {"start": v(-0.35, -58.35) * mm, "end": v(-0.34, -58.35) * mm});
            skLineSegment(sketch, "E770", {"start": v(-0.34, -58.35) * mm, "end": v(-0.33, -58.36) * mm});
            skLineSegment(sketch, "E771", {"start": v(-0.33, -58.36) * mm, "end": v(-0.32, -58.37) * mm});
            skLineSegment(sketch, "E772", {"start": v(-0.32, -58.37) * mm, "end": v(-0.32, -58.39) * mm});
            skLineSegment(sketch, "E773", {"start": v(-0.32, -58.39) * mm, "end": v(-0.3, -58.4) * mm});
            skLineSegment(sketch, "E774", {"start": v(-0.3, -58.4) * mm, "end": v(-0.3, -58.43) * mm});
            skLineSegment(sketch, "E775", {"start": v(-0.3, -58.43) * mm, "end": v(-0.3, -58.45) * mm});
            skLineSegment(sketch, "E776", {"start": v(-0.3, -58.45) * mm, "end": v(-0.3, -58.48) * mm});
            skLineSegment(sketch, "E777", {"start": v(-0.3, -58.48) * mm, "end": v(-0.3, -58.52) * mm});
            skLineSegment(sketch, "E778", {"start": v(-0.3, -58.52) * mm, "end": v(-0.3, -58.54) * mm});
            skLineSegment(sketch, "E779", {"start": v(-0.3, -58.54) * mm, "end": v(-0.29, -58.58) * mm});
            skLineSegment(sketch, "E780", {"start": v(-0.29, -58.58) * mm, "end": v(-0.28, -58.62) * mm});
            skLineSegment(sketch, "E781", {"start": v(-0.28, -58.62) * mm, "end": v(-0.28, -58.67) * mm});
            skLineSegment(sketch, "E782", {"start": v(-0.28, -58.67) * mm, "end": v(-0.27, -58.72) * mm});
            skLineSegment(sketch, "E783", {"start": v(-0.27, -58.72) * mm, "end": v(-0.27, -58.77) * mm});
            skLineSegment(sketch, "E784", {"start": v(-0.27, -58.77) * mm, "end": v(-0.26, -58.82) * mm});
            skLineSegment(sketch, "E785", {"start": v(-0.26, -58.82) * mm, "end": v(-0.25, -58.88) * mm});
            skLineSegment(sketch, "E786", {"start": v(-0.25, -58.88) * mm, "end": v(-0.24, -58.94) * mm});
            skLineSegment(sketch, "E787", {"start": v(-0.24, -58.94) * mm, "end": v(-0.23, -59) * mm});
            skLineSegment(sketch, "E788", {"start": v(-0.23, -59) * mm, "end": v(-0.21, -59.08) * mm});
            skLineSegment(sketch, "E789", {"start": v(-0.21, -59.08) * mm, "end": v(-0.2, -59.15) * mm});
            skLineSegment(sketch, "E790", {"start": v(-0.2, -59.15) * mm, "end": v(-0.18, -59.22) * mm});
            skLineSegment(sketch, "E791", {"start": v(-0.18, -59.22) * mm, "end": v(-0.16, -59.3) * mm});
            skLineSegment(sketch, "E792", {"start": v(-0.16, -59.3) * mm, "end": v(-0.14, -59.38) * mm});
            skLineSegment(sketch, "E793", {"start": v(-0.14, -59.38) * mm, "end": v(-0.11, -59.46) * mm});
            skLineSegment(sketch, "E794", {"start": v(-0.11, -59.46) * mm, "end": v(-0.09, -59.54) * mm});
            skLineSegment(sketch, "E795", {"start": v(-0.09, -59.54) * mm, "end": v(-0.06, -59.63) * mm});
            skLineSegment(sketch, "E796", {"start": v(-0.06, -59.63) * mm, "end": v(-0.03, -59.72) * mm});
            skLineSegment(sketch, "E797", {"start": v(-0.03, -59.72) * mm, "end": v(0, -59.78) * mm});
            skLineSegment(sketch, "E798", {"start": v(0, -59.78) * mm, "end": v(0.27, -59.83) * mm});
            skLineSegment(sketch, "E799", {"start": v(0.27, -59.83) * mm, "end": v(0.56, -59.83) * mm});
            skLineSegment(sketch, "E800", {"start": v(0.56, -59.83) * mm, "end": v(0.59, -59.77) * mm});
            skLineSegment(sketch, "E801", {"start": v(0.59, -59.77) * mm, "end": v(0.63, -59.69) * mm});
            skLineSegment(sketch, "E802", {"start": v(0.63, -59.69) * mm, "end": v(0.68, -59.6) * mm});
            skLineSegment(sketch, "E803", {"start": v(0.68, -59.6) * mm, "end": v(0.71, -59.53) * mm});
            skLineSegment(sketch, "E804", {"start": v(0.71, -59.53) * mm, "end": v(0.75, -59.45) * mm});
            skLineSegment(sketch, "E805", {"start": v(0.75, -59.45) * mm, "end": v(0.78, -59.37) * mm});
            skLineSegment(sketch, "E806", {"start": v(0.78, -59.37) * mm, "end": v(0.82, -59.3) * mm});
            skLineSegment(sketch, "E807", {"start": v(0.82, -59.3) * mm, "end": v(0.85, -59.23) * mm});
            skLineSegment(sketch, "E808", {"start": v(0.85, -59.23) * mm, "end": v(0.87, -59.16) * mm});
            skLineSegment(sketch, "E809", {"start": v(0.87, -59.16) * mm, "end": v(0.9, -59.1) * mm});
            skLineSegment(sketch, "E810", {"start": v(0.9, -59.1) * mm, "end": v(0.92, -59.04) * mm});
            skLineSegment(sketch, "E811", {"start": v(0.92, -59.04) * mm, "end": v(0.94, -58.98) * mm});
            skLineSegment(sketch, "E812", {"start": v(0.94, -58.98) * mm, "end": v(0.96, -58.92) * mm});
            skLineSegment(sketch, "E813", {"start": v(0.96, -58.92) * mm, "end": v(0.97, -58.87) * mm});
            skLineSegment(sketch, "E814", {"start": v(0.97, -58.87) * mm, "end": v(0.99, -58.81) * mm});
            skLineSegment(sketch, "E815", {"start": v(0.99, -58.81) * mm, "end": v(1, -58.77) * mm});
            skLineSegment(sketch, "E816", {"start": v(1, -58.77) * mm, "end": v(1.01, -58.72) * mm});
            skLineSegment(sketch, "E817", {"start": v(1.01, -58.72) * mm, "end": v(1.02, -58.68) * mm});
            skLineSegment(sketch, "E818", {"start": v(1.02, -58.68) * mm, "end": v(1.03, -58.64) * mm});
            skLineSegment(sketch, "E819", {"start": v(1.03, -58.64) * mm, "end": v(1.04, -58.62) * mm});
            skLineSegment(sketch, "E820", {"start": v(1.04, -58.62) * mm, "end": v(1.04, -58.59) * mm});
            skLineSegment(sketch, "E821", {"start": v(1.04, -58.59) * mm, "end": v(1.05, -58.56) * mm});
            skLineSegment(sketch, "E822", {"start": v(1.05, -58.56) * mm, "end": v(1.06, -58.54) * mm});
            skLineSegment(sketch, "E823", {"start": v(1.06, -58.54) * mm, "end": v(1.07, -58.52) * mm});
            skLineSegment(sketch, "E824", {"start": v(1.07, -58.52) * mm, "end": v(1.08, -58.5) * mm});
            skLineSegment(sketch, "E825", {"start": v(1.08, -58.5) * mm, "end": v(1.1, -58.48) * mm});
            skLineSegment(sketch, "E826", {"start": v(1.1, -58.48) * mm, "end": v(1.1, -58.47) * mm});
            skLineSegment(sketch, "E827", {"start": v(1.1, -58.47) * mm, "end": v(1.11, -58.47) * mm});
            skLineSegment(sketch, "E828", {"start": v(1.11, -58.47) * mm, "end": v(1.12, -58.46) * mm});
            skLineSegment(sketch, "E829", {"start": v(1.12, -58.46) * mm, "end": v(1.32, -58.47) * mm});
            skLineSegment(sketch, "E830", {"start": v(1.32, -58.47) * mm, "end": v(1.53, -58.47) * mm});
            skLineSegment(sketch, "E831", {"start": v(1.53, -58.47) * mm, "end": v(1.73, -58.46) * mm});
            skLineSegment(sketch, "E832", {"start": v(1.73, -58.46) * mm, "end": v(1.74, -58.47) * mm});
            skLineSegment(sketch, "E833", {"start": v(1.74, -58.47) * mm, "end": v(1.75, -58.47) * mm});
            skLineSegment(sketch, "E834", {"start": v(1.75, -58.47) * mm, "end": v(1.76, -58.48) * mm});
            skLineSegment(sketch, "E835", {"start": v(1.76, -58.48) * mm, "end": v(1.77, -58.5) * mm});
            skLineSegment(sketch, "E836", {"start": v(1.77, -58.5) * mm, "end": v(1.78, -58.52) * mm});
            skLineSegment(sketch, "E837", {"start": v(1.78, -58.52) * mm, "end": v(1.79, -58.54) * mm});
            skLineSegment(sketch, "E838", {"start": v(1.79, -58.54) * mm, "end": v(1.8, -58.56) * mm});
            skLineSegment(sketch, "E839", {"start": v(1.8, -58.56) * mm, "end": v(1.8, -58.59) * mm});
            skLineSegment(sketch, "E840", {"start": v(1.8, -58.59) * mm, "end": v(1.81, -58.62) * mm});
            skLineSegment(sketch, "E841", {"start": v(1.81, -58.62) * mm, "end": v(1.82, -58.64) * mm});
            skLineSegment(sketch, "E842", {"start": v(1.82, -58.64) * mm, "end": v(1.83, -58.68) * mm});
            skLineSegment(sketch, "E843", {"start": v(1.83, -58.68) * mm, "end": v(1.84, -58.72) * mm});
            skLineSegment(sketch, "E844", {"start": v(1.84, -58.72) * mm, "end": v(1.85, -58.77) * mm});
            skLineSegment(sketch, "E845", {"start": v(1.85, -58.77) * mm, "end": v(1.86, -58.81) * mm});
            skLineSegment(sketch, "E846", {"start": v(1.86, -58.81) * mm, "end": v(1.88, -58.87) * mm});
            skLineSegment(sketch, "E847", {"start": v(1.88, -58.87) * mm, "end": v(1.9, -58.92) * mm});
            skLineSegment(sketch, "E848", {"start": v(1.9, -58.92) * mm, "end": v(1.91, -58.98) * mm});
            skLineSegment(sketch, "E849", {"start": v(1.91, -58.98) * mm, "end": v(1.93, -59.04) * mm});
            skLineSegment(sketch, "E850", {"start": v(1.93, -59.04) * mm, "end": v(1.95, -59.1) * mm});
            skLineSegment(sketch, "E851", {"start": v(1.95, -59.1) * mm, "end": v(1.98, -59.16) * mm});
            skLineSegment(sketch, "E852", {"start": v(1.98, -59.16) * mm, "end": v(2, -59.23) * mm});
            skLineSegment(sketch, "E853", {"start": v(2, -59.23) * mm, "end": v(2.03, -59.3) * mm});
            skLineSegment(sketch, "E854", {"start": v(2.03, -59.3) * mm, "end": v(2.06, -59.37) * mm});
            skLineSegment(sketch, "E855", {"start": v(2.06, -59.37) * mm, "end": v(2.1, -59.45) * mm});
            skLineSegment(sketch, "E856", {"start": v(2.1, -59.45) * mm, "end": v(2.13, -59.53) * mm});
            skLineSegment(sketch, "E857", {"start": v(2.13, -59.53) * mm, "end": v(2.17, -59.6) * mm});
            skLineSegment(sketch, "E858", {"start": v(2.17, -59.6) * mm, "end": v(2.22, -59.69) * mm});
            skLineSegment(sketch, "E859", {"start": v(2.22, -59.69) * mm, "end": v(2.26, -59.77) * mm});
            skLineSegment(sketch, "E860", {"start": v(2.26, -59.77) * mm, "end": v(2.3, -59.83) * mm});
            skLineSegment(sketch, "E861", {"start": v(2.3, -59.83) * mm, "end": v(2.58, -59.83) * mm});
            skLineSegment(sketch, "E862", {"start": v(2.58, -59.83) * mm, "end": v(2.86, -59.78) * mm});
            skLineSegment(sketch, "E863", {"start": v(2.86, -59.78) * mm, "end": v(2.88, -59.72) * mm});
            skLineSegment(sketch, "E864", {"start": v(2.88, -59.72) * mm, "end": v(2.9, -59.63) * mm});
            skLineSegment(sketch, "E865", {"start": v(2.9, -59.63) * mm, "end": v(2.94, -59.54) * mm});
            skLineSegment(sketch, "E866", {"start": v(2.94, -59.54) * mm, "end": v(2.96, -59.46) * mm});
            skLineSegment(sketch, "E867", {"start": v(2.96, -59.46) * mm, "end": v(2.99, -59.38) * mm});
            skLineSegment(sketch, "E868", {"start": v(2.99, -59.38) * mm, "end": v(3, -59.3) * mm});
            skLineSegment(sketch, "E869", {"start": v(3, -59.3) * mm, "end": v(3.03, -59.22) * mm});
            skLineSegment(sketch, "E870", {"start": v(3.03, -59.22) * mm, "end": v(3.05, -59.15) * mm});
            skLineSegment(sketch, "E871", {"start": v(3.05, -59.15) * mm, "end": v(3.06, -59.08) * mm});
            skLineSegment(sketch, "E872", {"start": v(3.06, -59.08) * mm, "end": v(3.08, -59) * mm});
            skLineSegment(sketch, "E873", {"start": v(3.08, -59) * mm, "end": v(3.09, -58.94) * mm});
            skLineSegment(sketch, "E874", {"start": v(3.09, -58.94) * mm, "end": v(3.1, -58.88) * mm});
            skLineSegment(sketch, "E875", {"start": v(3.1, -58.88) * mm, "end": v(3.1, -58.82) * mm});
            skLineSegment(sketch, "E876", {"start": v(3.1, -58.82) * mm, "end": v(3.12, -58.77) * mm});
            skLineSegment(sketch, "E877", {"start": v(3.12, -58.77) * mm, "end": v(3.12, -58.72) * mm});
            skLineSegment(sketch, "E878", {"start": v(3.12, -58.72) * mm, "end": v(3.13, -58.67) * mm});
            skLineSegment(sketch, "E879", {"start": v(3.13, -58.67) * mm, "end": v(3.13, -58.62) * mm});
            skLineSegment(sketch, "E880", {"start": v(3.13, -58.62) * mm, "end": v(3.14, -58.58) * mm});
            skLineSegment(sketch, "E881", {"start": v(3.14, -58.58) * mm, "end": v(3.14, -58.54) * mm});
            skLineSegment(sketch, "E882", {"start": v(3.14, -58.54) * mm, "end": v(3.14, -58.52) * mm});
            skLineSegment(sketch, "E883", {"start": v(3.14, -58.52) * mm, "end": v(3.14, -58.48) * mm});
            skLineSegment(sketch, "E884", {"start": v(3.14, -58.48) * mm, "end": v(3.15, -58.45) * mm});
            skLineSegment(sketch, "E885", {"start": v(3.15, -58.45) * mm, "end": v(3.15, -58.43) * mm});
            skLineSegment(sketch, "E886", {"start": v(3.15, -58.43) * mm, "end": v(3.16, -58.4) * mm});
            skLineSegment(sketch, "E887", {"start": v(3.16, -58.4) * mm, "end": v(3.17, -58.39) * mm});
            skLineSegment(sketch, "E888", {"start": v(3.17, -58.39) * mm, "end": v(3.17, -58.37) * mm});
            skLineSegment(sketch, "E889", {"start": v(3.17, -58.37) * mm, "end": v(3.18, -58.36) * mm});
            skLineSegment(sketch, "E890", {"start": v(3.18, -58.36) * mm, "end": v(3.2, -58.35) * mm});
            skLineSegment(sketch, "E891", {"start": v(3.2, -58.35) * mm, "end": v(3.2, -58.35) * mm});
            skLineSegment(sketch, "E892", {"start": v(3.2, -58.35) * mm, "end": v(3.4, -58.32) * mm});
            skLineSegment(sketch, "E893", {"start": v(3.4, -58.32) * mm, "end": v(3.6, -58.29) * mm});
            skLineSegment(sketch, "E894", {"start": v(3.6, -58.29) * mm, "end": v(3.8, -58.25) * mm});
            skLineSegment(sketch, "E895", {"start": v(3.8, -58.25) * mm, "end": v(3.8, -58.25) * mm});
            skLineSegment(sketch, "E896", {"start": v(3.8, -58.25) * mm, "end": v(3.82, -58.26) * mm});
            skLineSegment(sketch, "E897", {"start": v(3.82, -58.26) * mm, "end": v(3.83, -58.27) * mm});
            skLineSegment(sketch, "E898", {"start": v(3.83, -58.27) * mm, "end": v(3.84, -58.28) * mm});
            skLineSegment(sketch, "E899", {"start": v(3.84, -58.28) * mm, "end": v(3.86, -58.3) * mm});
            skLineSegment(sketch, "E900", {"start": v(3.86, -58.3) * mm, "end": v(3.87, -58.32) * mm});
            skLineSegment(sketch, "E901", {"start": v(3.87, -58.32) * mm, "end": v(3.88, -58.34) * mm});
            skLineSegment(sketch, "E902", {"start": v(3.88, -58.34) * mm, "end": v(3.9, -58.36) * mm});
            skLineSegment(sketch, "E903", {"start": v(3.9, -58.36) * mm, "end": v(3.9, -58.4) * mm});
            skLineSegment(sketch, "E904", {"start": v(3.9, -58.4) * mm, "end": v(3.91, -58.41) * mm});
            skLineSegment(sketch, "E905", {"start": v(3.91, -58.41) * mm, "end": v(3.93, -58.45) * mm});
            skLineSegment(sketch, "E906", {"start": v(3.93, -58.45) * mm, "end": v(3.95, -58.5) * mm});
            skLineSegment(sketch, "E907", {"start": v(3.95, -58.5) * mm, "end": v(3.96, -58.53) * mm});
            skLineSegment(sketch, "E908", {"start": v(3.96, -58.53) * mm, "end": v(3.99, -58.58) * mm});
            skLineSegment(sketch, "E909", {"start": v(3.99, -58.58) * mm, "end": v(4, -58.63) * mm});
            skLineSegment(sketch, "E910", {"start": v(4, -58.63) * mm, "end": v(4.03, -58.68) * mm});
            skLineSegment(sketch, "E911", {"start": v(4.03, -58.68) * mm, "end": v(4.06, -58.73) * mm});
            skLineSegment(sketch, "E912", {"start": v(4.06, -58.73) * mm, "end": v(4.09, -58.79) * mm});
            skLineSegment(sketch, "E913", {"start": v(4.09, -58.79) * mm, "end": v(4.12, -58.84) * mm});
            skLineSegment(sketch, "E914", {"start": v(4.12, -58.84) * mm, "end": v(4.15, -58.9) * mm});
            skLineSegment(sketch, "E915", {"start": v(4.15, -58.9) * mm, "end": v(4.2, -58.97) * mm});
            skLineSegment(sketch, "E916", {"start": v(4.2, -58.97) * mm, "end": v(4.23, -59.03) * mm});
            skLineSegment(sketch, "E917", {"start": v(4.23, -59.03) * mm, "end": v(4.27, -59.1) * mm});
            skLineSegment(sketch, "E918", {"start": v(4.27, -59.1) * mm, "end": v(4.32, -59.17) * mm});
            skLineSegment(sketch, "E919", {"start": v(4.32, -59.17) * mm, "end": v(4.37, -59.24) * mm});
            skLineSegment(sketch, "E920", {"start": v(4.37, -59.24) * mm, "end": v(4.42, -59.31) * mm});
            skLineSegment(sketch, "E921", {"start": v(4.42, -59.31) * mm, "end": v(4.47, -59.39) * mm});
            skLineSegment(sketch, "E922", {"start": v(4.47, -59.39) * mm, "end": v(4.53, -59.46) * mm});
            skLineSegment(sketch, "E923", {"start": v(4.53, -59.46) * mm, "end": v(4.57, -59.51) * mm});
            skLineSegment(sketch, "E924", {"start": v(4.57, -59.51) * mm, "end": v(4.85, -59.47) * mm});
            skLineSegment(sketch, "E925", {"start": v(4.85, -59.47) * mm, "end": v(5.12, -59.38) * mm});
            skLineSegment(sketch, "E926", {"start": v(5.12, -59.38) * mm, "end": v(5.13, -59.32) * mm});
            skLineSegment(sketch, "E927", {"start": v(5.13, -59.32) * mm, "end": v(5.15, -59.22) * mm});
            skLineSegment(sketch, "E928", {"start": v(5.15, -59.22) * mm, "end": v(5.16, -59.13) * mm});
            skLineSegment(sketch, "E929", {"start": v(5.16, -59.13) * mm, "end": v(5.18, -59.04) * mm});
            skLineSegment(sketch, "E930", {"start": v(5.18, -59.04) * mm, "end": v(5.19, -58.96) * mm});
            skLineSegment(sketch, "E931", {"start": v(5.19, -58.96) * mm, "end": v(5.2, -58.88) * mm});
            skLineSegment(sketch, "E932", {"start": v(5.2, -58.88) * mm, "end": v(5.2, -58.8) * mm});
            skLineSegment(sketch, "E933", {"start": v(5.2, -58.8) * mm, "end": v(5.2, -58.72) * mm});
            skLineSegment(sketch, "E934", {"start": v(5.2, -58.72) * mm, "end": v(5.21, -58.65) * mm});
            skLineSegment(sketch, "E935", {"start": v(5.21, -58.65) * mm, "end": v(5.22, -58.58) * mm});
            skLineSegment(sketch, "E936", {"start": v(5.22, -58.58) * mm, "end": v(5.22, -58.51) * mm});
            skLineSegment(sketch, "E937", {"start": v(5.22, -58.51) * mm, "end": v(5.22, -58.45) * mm});
            skLineSegment(sketch, "E938", {"start": v(5.22, -58.45) * mm, "end": v(5.22, -58.4) * mm});
            skLineSegment(sketch, "E939", {"start": v(5.22, -58.4) * mm, "end": v(5.22, -58.34) * mm});
            skLineSegment(sketch, "E940", {"start": v(5.22, -58.34) * mm, "end": v(5.22, -58.28) * mm});
            skLineSegment(sketch, "E941", {"start": v(5.22, -58.28) * mm, "end": v(5.21, -58.23) * mm});
            skLineSegment(sketch, "E942", {"start": v(5.21, -58.23) * mm, "end": v(5.21, -58.19) * mm});
            skLineSegment(sketch, "E943", {"start": v(5.21, -58.19) * mm, "end": v(5.2, -58.14) * mm});
            skLineSegment(sketch, "E944", {"start": v(5.2, -58.14) * mm, "end": v(5.2, -58.1) * mm});
            skLineSegment(sketch, "E945", {"start": v(5.2, -58.1) * mm, "end": v(5.2, -58.08) * mm});
            skLineSegment(sketch, "E946", {"start": v(5.2, -58.08) * mm, "end": v(5.2, -58.05) * mm});
            skLineSegment(sketch, "E947", {"start": v(5.2, -58.05) * mm, "end": v(5.2, -58.02) * mm});
            skLineSegment(sketch, "E948", {"start": v(5.2, -58.02) * mm, "end": v(5.2, -58) * mm});
            skLineSegment(sketch, "E949", {"start": v(5.2, -58) * mm, "end": v(5.2, -57.97) * mm});
            skLineSegment(sketch, "E950", {"start": v(5.2, -57.97) * mm, "end": v(5.2, -57.95) * mm});
            skLineSegment(sketch, "E951", {"start": v(5.2, -57.95) * mm, "end": v(5.21, -57.94) * mm});
            skLineSegment(sketch, "E952", {"start": v(5.21, -57.94) * mm, "end": v(5.22, -57.92) * mm});
            skLineSegment(sketch, "E953", {"start": v(5.22, -57.92) * mm, "end": v(5.23, -57.91) * mm});
            skLineSegment(sketch, "E954", {"start": v(5.23, -57.91) * mm, "end": v(5.24, -57.9) * mm});
            skLineSegment(sketch, "E955", {"start": v(5.24, -57.9) * mm, "end": v(5.43, -57.85) * mm});
            skLineSegment(sketch, "E956", {"start": v(5.43, -57.85) * mm, "end": v(5.62, -57.79) * mm});
            skLineSegment(sketch, "E957", {"start": v(5.62, -57.79) * mm, "end": v(5.8, -57.72) * mm});
            skLineSegment(sketch, "E958", {"start": v(5.8, -57.72) * mm, "end": v(5.82, -57.72) * mm});
            skLineSegment(sketch, "E959", {"start": v(5.82, -57.72) * mm, "end": v(5.83, -57.72) * mm});
            skLineSegment(sketch, "E960", {"start": v(5.83, -57.72) * mm, "end": v(5.85, -57.73) * mm});
            skLineSegment(sketch, "E961", {"start": v(5.85, -57.73) * mm, "end": v(5.86, -57.74) * mm});
            skLineSegment(sketch, "E962", {"start": v(5.86, -57.74) * mm, "end": v(5.88, -57.75) * mm});
            skLineSegment(sketch, "E963", {"start": v(5.88, -57.75) * mm, "end": v(5.9, -57.77) * mm});
            skLineSegment(sketch, "E964", {"start": v(5.9, -57.77) * mm, "end": v(5.9, -57.8) * mm});
            skLineSegment(sketch, "E965", {"start": v(5.9, -57.8) * mm, "end": v(5.92, -57.82) * mm});
            skLineSegment(sketch, "E966", {"start": v(5.92, -57.82) * mm, "end": v(5.94, -57.84) * mm});
            skLineSegment(sketch, "E967", {"start": v(5.94, -57.84) * mm, "end": v(5.95, -57.86) * mm});
            skLineSegment(sketch, "E968", {"start": v(5.95, -57.86) * mm, "end": v(5.97, -57.9) * mm});
            skLineSegment(sketch, "E969", {"start": v(5.97, -57.9) * mm, "end": v(6, -57.93) * mm});
            skLineSegment(sketch, "E970", {"start": v(6, -57.93) * mm, "end": v(6.02, -57.97) * mm});
            skLineSegment(sketch, "E971", {"start": v(6.02, -57.97) * mm, "end": v(6.05, -58.01) * mm});
            skLineSegment(sketch, "E972", {"start": v(6.05, -58.01) * mm, "end": v(6.08, -58.06) * mm});
            skLineSegment(sketch, "E973", {"start": v(6.08, -58.06) * mm, "end": v(6.1, -58.1) * mm});
            skLineSegment(sketch, "E974", {"start": v(6.1, -58.1) * mm, "end": v(6.14, -58.15) * mm});
            skLineSegment(sketch, "E975", {"start": v(6.14, -58.15) * mm, "end": v(6.18, -58.2) * mm});
            skLineSegment(sketch, "E976", {"start": v(6.18, -58.2) * mm, "end": v(6.22, -58.25) * mm});
            skLineSegment(sketch, "E977", {"start": v(6.22, -58.25) * mm, "end": v(6.27, -58.3) * mm});
            skLineSegment(sketch, "E978", {"start": v(6.27, -58.3) * mm, "end": v(6.31, -58.36) * mm});
            skLineSegment(sketch, "E979", {"start": v(6.31, -58.36) * mm, "end": v(6.36, -58.42) * mm});
            skLineSegment(sketch, "E980", {"start": v(6.36, -58.42) * mm, "end": v(6.41, -58.48) * mm});
            skLineSegment(sketch, "E981", {"start": v(6.41, -58.48) * mm, "end": v(6.47, -58.54) * mm});
            skLineSegment(sketch, "E982", {"start": v(6.47, -58.54) * mm, "end": v(6.53, -58.6) * mm});
            skLineSegment(sketch, "E983", {"start": v(6.53, -58.6) * mm, "end": v(6.59, -58.67) * mm});
            skLineSegment(sketch, "E984", {"start": v(6.59, -58.67) * mm, "end": v(6.65, -58.73) * mm});
            skLineSegment(sketch, "E985", {"start": v(6.65, -58.73) * mm, "end": v(6.72, -58.8) * mm});
            skLineSegment(sketch, "E986", {"start": v(6.72, -58.8) * mm, "end": v(6.77, -58.84) * mm});
            skLineSegment(sketch, "E987", {"start": v(6.77, -58.84) * mm, "end": v(7.04, -58.76) * mm});
            skLineSegment(sketch, "E988", {"start": v(7.04, -58.76) * mm, "end": v(7.3, -58.63) * mm});
            skLineSegment(sketch, "E989", {"start": v(7.3, -58.63) * mm, "end": v(7.3, -58.56) * mm});
            skLineSegment(sketch, "E990", {"start": v(7.3, -58.56) * mm, "end": v(7.3, -58.47) * mm});
            skLineSegment(sketch, "E991", {"start": v(7.3, -58.47) * mm, "end": v(7.3, -58.38) * mm});
            skLineSegment(sketch, "E992", {"start": v(7.3, -58.38) * mm, "end": v(7.3, -58.29) * mm});
            skLineSegment(sketch, "E993", {"start": v(7.3, -58.29) * mm, "end": v(7.3, -58.2) * mm});
            skLineSegment(sketch, "E994", {"start": v(7.3, -58.2) * mm, "end": v(7.29, -58.12) * mm});
            skLineSegment(sketch, "E995", {"start": v(7.29, -58.12) * mm, "end": v(7.28, -58.04) * mm});
            skLineSegment(sketch, "E996", {"start": v(7.28, -58.04) * mm, "end": v(7.28, -57.96) * mm});
            skLineSegment(sketch, "E997", {"start": v(7.28, -57.96) * mm, "end": v(7.27, -57.9) * mm});
            skLineSegment(sketch, "E998", {"start": v(7.27, -57.9) * mm, "end": v(7.26, -57.82) * mm});
            skLineSegment(sketch, "E999", {"start": v(7.26, -57.82) * mm, "end": v(7.25, -57.76) * mm});
            skLineSegment(sketch, "E1000", {"start": v(7.25, -57.76) * mm, "end": v(7.25, -57.7) * mm});
            skLineSegment(sketch, "E1001", {"start": v(7.25, -57.7) * mm, "end": v(7.24, -57.64) * mm});
            skLineSegment(sketch, "E1002", {"start": v(7.24, -57.64) * mm, "end": v(7.23, -57.58) * mm});
            skLineSegment(sketch, "E1003", {"start": v(7.23, -57.58) * mm, "end": v(7.22, -57.53) * mm});
            skLineSegment(sketch, "E1004", {"start": v(7.22, -57.53) * mm, "end": v(7.2, -57.48) * mm});
            skLineSegment(sketch, "E1005", {"start": v(7.2, -57.48) * mm, "end": v(7.2, -57.43) * mm});
            skLineSegment(sketch, "E1006", {"start": v(7.2, -57.43) * mm, "end": v(7.19, -57.4) * mm});
            skLineSegment(sketch, "E1007", {"start": v(7.19, -57.4) * mm, "end": v(7.18, -57.35) * mm});
            skLineSegment(sketch, "E1008", {"start": v(7.18, -57.35) * mm, "end": v(7.17, -57.33) * mm});
            skLineSegment(sketch, "E1009", {"start": v(7.17, -57.33) * mm, "end": v(7.16, -57.3) * mm});
            skLineSegment(sketch, "E1010", {"start": v(7.16, -57.3) * mm, "end": v(7.16, -57.27) * mm});
            skLineSegment(sketch, "E1011", {"start": v(7.16, -57.27) * mm, "end": v(7.16, -57.25) * mm});
            skLineSegment(sketch, "E1012", {"start": v(7.16, -57.25) * mm, "end": v(7.15, -57.22) * mm});
            skLineSegment(sketch, "E1013", {"start": v(7.15, -57.22) * mm, "end": v(7.16, -57.2) * mm});
            skLineSegment(sketch, "E1014", {"start": v(7.16, -57.2) * mm, "end": v(7.16, -57.19) * mm});
            skLineSegment(sketch, "E1015", {"start": v(7.16, -57.19) * mm, "end": v(7.16, -57.17) * mm});
            skLineSegment(sketch, "E1016", {"start": v(7.16, -57.17) * mm, "end": v(7.17, -57.16) * mm});
            skLineSegment(sketch, "E1017", {"start": v(7.17, -57.16) * mm, "end": v(7.18, -57.15) * mm});
            skLineSegment(sketch, "E1018", {"start": v(7.18, -57.15) * mm, "end": v(7.35, -57.07) * mm});
            skLineSegment(sketch, "E1019", {"start": v(7.35, -57.07) * mm, "end": v(7.54, -56.97) * mm});
            skLineSegment(sketch, "E1020", {"start": v(7.54, -56.97) * mm, "end": v(7.71, -56.88) * mm});
            skLineSegment(sketch, "E1021", {"start": v(7.71, -56.88) * mm, "end": v(7.73, -56.88) * mm});
            skLineSegment(sketch, "E1022", {"start": v(7.73, -56.88) * mm, "end": v(7.74, -56.88) * mm});
            skLineSegment(sketch, "E1023", {"start": v(7.74, -56.88) * mm, "end": v(7.75, -56.88) * mm});
            skLineSegment(sketch, "E1024", {"start": v(7.75, -56.88) * mm, "end": v(7.77, -56.9) * mm});
            skLineSegment(sketch, "E1025", {"start": v(7.77, -56.9) * mm, "end": v(7.79, -56.9) * mm});
            skLineSegment(sketch, "E1026", {"start": v(7.79, -56.9) * mm, "end": v(7.8, -56.92) * mm});
            skLineSegment(sketch, "E1027", {"start": v(7.8, -56.92) * mm, "end": v(7.82, -56.94) * mm});
            skLineSegment(sketch, "E1028", {"start": v(7.82, -56.94) * mm, "end": v(7.84, -56.96) * mm});
            skLineSegment(sketch, "E1029", {"start": v(7.84, -56.96) * mm, "end": v(7.86, -56.98) * mm});
            skLineSegment(sketch, "E1030", {"start": v(7.86, -56.98) * mm, "end": v(7.88, -57) * mm});
            skLineSegment(sketch, "E1031", {"start": v(7.88, -57) * mm, "end": v(7.9, -57.03) * mm});
            skLineSegment(sketch, "E1032", {"start": v(7.9, -57.03) * mm, "end": v(7.93, -57.06) * mm});
            skLineSegment(sketch, "E1033", {"start": v(7.93, -57.06) * mm, "end": v(7.96, -57.1) * mm});
            skLineSegment(sketch, "E1034", {"start": v(7.96, -57.1) * mm, "end": v(8, -57.13) * mm});
            skLineSegment(sketch, "E1035", {"start": v(8, -57.13) * mm, "end": v(8.03, -57.17) * mm});
            skLineSegment(sketch, "E1036", {"start": v(8.03, -57.17) * mm, "end": v(8.07, -57.21) * mm});
            skLineSegment(sketch, "E1037", {"start": v(8.07, -57.21) * mm, "end": v(8.11, -57.25) * mm});
            skLineSegment(sketch, "E1038", {"start": v(8.11, -57.25) * mm, "end": v(8.16, -57.3) * mm});
            skLineSegment(sketch, "E1039", {"start": v(8.16, -57.3) * mm, "end": v(8.2, -57.34) * mm});
            skLineSegment(sketch, "E1040", {"start": v(8.2, -57.34) * mm, "end": v(8.26, -57.39) * mm});
            skLineSegment(sketch, "E1041", {"start": v(8.26, -57.39) * mm, "end": v(8.31, -57.44) * mm});
            skLineSegment(sketch, "E1042", {"start": v(8.31, -57.44) * mm, "end": v(8.37, -57.49) * mm});
            skLineSegment(sketch, "E1043", {"start": v(8.37, -57.49) * mm, "end": v(8.43, -57.54) * mm});
            skLineSegment(sketch, "E1044", {"start": v(8.43, -57.54) * mm, "end": v(8.5, -57.59) * mm});
            skLineSegment(sketch, "E1045", {"start": v(8.5, -57.59) * mm, "end": v(8.56, -57.64) * mm});
            skLineSegment(sketch, "E1046", {"start": v(8.56, -57.64) * mm, "end": v(8.63, -57.7) * mm});
            skLineSegment(sketch, "E1047", {"start": v(8.63, -57.7) * mm, "end": v(8.7, -57.75) * mm});
            skLineSegment(sketch, "E1048", {"start": v(8.7, -57.75) * mm, "end": v(8.78, -57.8) * mm});
            skLineSegment(sketch, "E1049", {"start": v(8.78, -57.8) * mm, "end": v(8.84, -57.84) * mm});
            skLineSegment(sketch, "E1050", {"start": v(8.84, -57.84) * mm, "end": v(9.1, -57.71) * mm});
            skLineSegment(sketch, "E1051", {"start": v(9.1, -57.71) * mm, "end": v(9.32, -57.54) * mm});
            skLineSegment(sketch, "E1052", {"start": v(9.32, -57.54) * mm, "end": v(9.31, -57.48) * mm});
            skLineSegment(sketch, "E1053", {"start": v(9.31, -57.48) * mm, "end": v(9.3, -57.39) * mm});
            skLineSegment(sketch, "E1054", {"start": v(9.3, -57.39) * mm, "end": v(9.29, -57.3) * mm});
            skLineSegment(sketch, "E1055", {"start": v(9.29, -57.3) * mm, "end": v(9.27, -57.2) * mm});
            skLineSegment(sketch, "E1056", {"start": v(9.27, -57.2) * mm, "end": v(9.25, -57.12) * mm});
            skLineSegment(sketch, "E1057", {"start": v(9.25, -57.12) * mm, "end": v(9.24, -57.04) * mm});
            skLineSegment(sketch, "E1058", {"start": v(9.24, -57.04) * mm, "end": v(9.22, -56.96) * mm});
            skLineSegment(sketch, "E1059", {"start": v(9.22, -56.96) * mm, "end": v(9.2, -56.9) * mm});
            skLineSegment(sketch, "E1060", {"start": v(9.2, -56.9) * mm, "end": v(9.18, -56.82) * mm});
            skLineSegment(sketch, "E1061", {"start": v(9.18, -56.82) * mm, "end": v(9.17, -56.75) * mm});
            skLineSegment(sketch, "E1062", {"start": v(9.17, -56.75) * mm, "end": v(9.15, -56.7) * mm});
            skLineSegment(sketch, "E1063", {"start": v(9.15, -56.7) * mm, "end": v(9.13, -56.63) * mm});
            skLineSegment(sketch, "E1064", {"start": v(9.13, -56.63) * mm, "end": v(9.11, -56.57) * mm});
            skLineSegment(sketch, "E1065", {"start": v(9.11, -56.57) * mm, "end": v(9.1, -56.52) * mm});
            skLineSegment(sketch, "E1066", {"start": v(9.1, -56.52) * mm, "end": v(9.07, -56.47) * mm});
            skLineSegment(sketch, "E1067", {"start": v(9.07, -56.47) * mm, "end": v(9.06, -56.42) * mm});
            skLineSegment(sketch, "E1068", {"start": v(9.06, -56.42) * mm, "end": v(9.04, -56.38) * mm});
            skLineSegment(sketch, "E1069", {"start": v(9.04, -56.38) * mm, "end": v(9.02, -56.34) * mm});
            skLineSegment(sketch, "E1070", {"start": v(9.02, -56.34) * mm, "end": v(9, -56.3) * mm});
            skLineSegment(sketch, "E1071", {"start": v(9, -56.3) * mm, "end": v(9, -56.29) * mm});
            skLineSegment(sketch, "E1072", {"start": v(9, -56.29) * mm, "end": v(8.99, -56.26) * mm});
            skLineSegment(sketch, "E1073", {"start": v(8.99, -56.26) * mm, "end": v(8.98, -56.23) * mm});
            skLineSegment(sketch, "E1074", {"start": v(8.98, -56.23) * mm, "end": v(8.97, -56.2) * mm});
            skLineSegment(sketch, "E1075", {"start": v(8.97, -56.2) * mm, "end": v(8.96, -56.18) * mm});
            skLineSegment(sketch, "E1076", {"start": v(8.96, -56.18) * mm, "end": v(8.96, -56.16) * mm});
            skLineSegment(sketch, "E1077", {"start": v(8.96, -56.16) * mm, "end": v(8.96, -56.14) * mm});
            skLineSegment(sketch, "E1078", {"start": v(8.96, -56.14) * mm, "end": v(8.97, -56.13) * mm});
            skLineSegment(sketch, "E1079", {"start": v(8.97, -56.13) * mm, "end": v(8.97, -56.12) * mm});
            skLineSegment(sketch, "E1080", {"start": v(8.97, -56.12) * mm, "end": v(8.98, -56.1) * mm});
            skLineSegment(sketch, "E1081", {"start": v(8.98, -56.1) * mm, "end": v(9.14, -56) * mm});
            skLineSegment(sketch, "E1082", {"start": v(9.14, -56) * mm, "end": v(9.3, -55.87) * mm});
            skLineSegment(sketch, "E1083", {"start": v(9.3, -55.87) * mm, "end": v(9.46, -55.75) * mm});
            skLineSegment(sketch, "E1084", {"start": v(9.46, -55.75) * mm, "end": v(9.47, -55.75) * mm});
            skLineSegment(sketch, "E1085", {"start": v(9.47, -55.75) * mm, "end": v(9.49, -55.75) * mm});
            skLineSegment(sketch, "E1086", {"start": v(9.49, -55.75) * mm, "end": v(9.5, -55.75) * mm});
            skLineSegment(sketch, "E1087", {"start": v(9.5, -55.75) * mm, "end": v(9.52, -55.76) * mm});
            skLineSegment(sketch, "E1088", {"start": v(9.52, -55.76) * mm, "end": v(9.54, -55.76) * mm});
            skLineSegment(sketch, "E1089", {"start": v(9.54, -55.76) * mm, "end": v(9.56, -55.78) * mm});
            skLineSegment(sketch, "E1090", {"start": v(9.56, -55.78) * mm, "end": v(9.58, -55.8) * mm});
            skLineSegment(sketch, "E1091", {"start": v(9.58, -55.8) * mm, "end": v(9.6, -55.8) * mm});
            skLineSegment(sketch, "E1092", {"start": v(9.6, -55.8) * mm, "end": v(9.63, -55.83) * mm});
            skLineSegment(sketch, "E1093", {"start": v(9.63, -55.83) * mm, "end": v(9.64, -55.84) * mm});
            skLineSegment(sketch, "E1094", {"start": v(9.64, -55.84) * mm, "end": v(9.67, -55.87) * mm});
            skLineSegment(sketch, "E1095", {"start": v(9.67, -55.87) * mm, "end": v(9.7, -55.9) * mm});
            skLineSegment(sketch, "E1096", {"start": v(9.7, -55.9) * mm, "end": v(9.74, -55.93) * mm});
            skLineSegment(sketch, "E1097", {"start": v(9.74, -55.93) * mm, "end": v(9.78, -55.96) * mm});
            skLineSegment(sketch, "E1098", {"start": v(9.78, -55.96) * mm, "end": v(9.82, -56) * mm});
            skLineSegment(sketch, "E1099", {"start": v(9.82, -56) * mm, "end": v(9.87, -56.02) * mm});
            skLineSegment(sketch, "E1100", {"start": v(9.87, -56.02) * mm, "end": v(9.91, -56.06) * mm});
            skLineSegment(sketch, "E1101", {"start": v(9.91, -56.06) * mm, "end": v(9.97, -56.1) * mm});
            skLineSegment(sketch, "E1102", {"start": v(9.97, -56.1) * mm, "end": v(10.02, -56.13) * mm});
            skLineSegment(sketch, "E1103", {"start": v(10.02, -56.13) * mm, "end": v(10.08, -56.17) * mm});
            skLineSegment(sketch, "E1104", {"start": v(10.08, -56.17) * mm, "end": v(10.14, -56.2) * mm});
            skLineSegment(sketch, "E1105", {"start": v(10.14, -56.2) * mm, "end": v(10.2, -56.25) * mm});
            skLineSegment(sketch, "E1106", {"start": v(10.2, -56.25) * mm, "end": v(10.27, -56.29) * mm});
            skLineSegment(sketch, "E1107", {"start": v(10.27, -56.29) * mm, "end": v(10.34, -56.33) * mm});
            skLineSegment(sketch, "E1108", {"start": v(10.34, -56.33) * mm, "end": v(10.42, -56.37) * mm});
            skLineSegment(sketch, "E1109", {"start": v(10.42, -56.37) * mm, "end": v(10.5, -56.41) * mm});
            skLineSegment(sketch, "E1110", {"start": v(10.5, -56.41) * mm, "end": v(10.58, -56.46) * mm});
            skLineSegment(sketch, "E1111", {"start": v(10.58, -56.46) * mm, "end": v(10.67, -56.5) * mm});
            skLineSegment(sketch, "E1112", {"start": v(10.67, -56.5) * mm, "end": v(10.72, -56.52) * mm});
            skLineSegment(sketch, "E1113", {"start": v(10.72, -56.52) * mm, "end": v(10.95, -56.36) * mm});
            skLineSegment(sketch, "E1114", {"start": v(10.95, -56.36) * mm, "end": v(11.16, -56.16) * mm});
            skLineSegment(sketch, "E1115", {"start": v(11.16, -56.16) * mm, "end": v(11.14, -56.1) * mm});
            skLineSegment(sketch, "E1116", {"start": v(11.14, -56.1) * mm, "end": v(11.1, -56) * mm});
            skLineSegment(sketch, "E1117", {"start": v(11.1, -56) * mm, "end": v(11.08, -55.92) * mm});
            skLineSegment(sketch, "E1118", {"start": v(11.08, -55.92) * mm, "end": v(11.05, -55.83) * mm});
            skLineSegment(sketch, "E1119", {"start": v(11.05, -55.83) * mm, "end": v(11.02, -55.75) * mm});
            skLineSegment(sketch, "E1120", {"start": v(11.02, -55.75) * mm, "end": v(11, -55.67) * mm});
            skLineSegment(sketch, "E1121", {"start": v(11, -55.67) * mm, "end": v(10.96, -55.6) * mm});
            skLineSegment(sketch, "E1122", {"start": v(10.96, -55.6) * mm, "end": v(10.94, -55.53) * mm});
            skLineSegment(sketch, "E1123", {"start": v(10.94, -55.53) * mm, "end": v(10.9, -55.46) * mm});
            skLineSegment(sketch, "E1124", {"start": v(10.9, -55.46) * mm, "end": v(10.88, -55.4) * mm});
            skLineSegment(sketch, "E1125", {"start": v(10.88, -55.4) * mm, "end": v(10.85, -55.34) * mm});
            skLineSegment(sketch, "E1126", {"start": v(10.85, -55.34) * mm, "end": v(10.82, -55.28) * mm});
            skLineSegment(sketch, "E1127", {"start": v(10.82, -55.28) * mm, "end": v(10.8, -55.23) * mm});
            skLineSegment(sketch, "E1128", {"start": v(10.8, -55.23) * mm, "end": v(10.77, -55.18) * mm});
            skLineSegment(sketch, "E1129", {"start": v(10.77, -55.18) * mm, "end": v(10.74, -55.14) * mm});
            skLineSegment(sketch, "E1130", {"start": v(10.74, -55.14) * mm, "end": v(10.72, -55.1) * mm});
            skLineSegment(sketch, "E1131", {"start": v(10.72, -55.1) * mm, "end": v(10.7, -55.05) * mm});
            skLineSegment(sketch, "E1132", {"start": v(10.7, -55.05) * mm, "end": v(10.67, -55.02) * mm});
            skLineSegment(sketch, "E1133", {"start": v(10.67, -55.02) * mm, "end": v(10.65, -54.98) * mm});
            skLineSegment(sketch, "E1134", {"start": v(10.65, -54.98) * mm, "end": v(10.64, -54.97) * mm});
            skLineSegment(sketch, "E1135", {"start": v(10.64, -54.97) * mm, "end": v(10.62, -54.94) * mm});
            skLineSegment(sketch, "E1136", {"start": v(10.62, -54.94) * mm, "end": v(10.6, -54.91) * mm});
            skLineSegment(sketch, "E1137", {"start": v(10.6, -54.91) * mm, "end": v(10.6, -54.89) * mm});
            skLineSegment(sketch, "E1138", {"start": v(10.6, -54.89) * mm, "end": v(10.59, -54.87) * mm});
            skLineSegment(sketch, "E1139", {"start": v(10.59, -54.87) * mm, "end": v(10.58, -54.85) * mm});
            skLineSegment(sketch, "E1140", {"start": v(10.58, -54.85) * mm, "end": v(10.58, -54.83) * mm});
            skLineSegment(sketch, "E1141", {"start": v(10.58, -54.83) * mm, "end": v(10.58, -54.81) * mm});
            skLineSegment(sketch, "E1142", {"start": v(10.58, -54.81) * mm, "end": v(10.59, -54.8) * mm});
            skLineSegment(sketch, "E1143", {"start": v(10.59, -54.8) * mm, "end": v(10.6, -54.8) * mm});
            skLineSegment(sketch, "E1144", {"start": v(10.6, -54.8) * mm, "end": v(10.73, -54.65) * mm});
            skLineSegment(sketch, "E1145", {"start": v(10.73, -54.65) * mm, "end": v(10.88, -54.5) * mm});
            skLineSegment(sketch, "E1146", {"start": v(10.88, -54.5) * mm, "end": v(11.02, -54.37) * mm});
            skLineSegment(sketch, "E1147", {"start": v(11.02, -54.37) * mm, "end": v(11.03, -54.36) * mm});
            skLineSegment(sketch, "E1148", {"start": v(11.03, -54.36) * mm, "end": v(11.04, -54.36) * mm});
            skLineSegment(sketch, "E1149", {"start": v(11.04, -54.36) * mm, "end": v(11.05, -54.36) * mm});
            skLineSegment(sketch, "E1150", {"start": v(11.05, -54.36) * mm, "end": v(11.07, -54.36) * mm});
            skLineSegment(sketch, "E1151", {"start": v(11.07, -54.36) * mm, "end": v(11.1, -54.36) * mm});
            skLineSegment(sketch, "E1152", {"start": v(11.1, -54.36) * mm, "end": v(11.11, -54.37) * mm});
            skLineSegment(sketch, "E1153", {"start": v(11.11, -54.37) * mm, "end": v(11.14, -54.38) * mm});
            skLineSegment(sketch, "E1154", {"start": v(11.14, -54.38) * mm, "end": v(11.16, -54.4) * mm});
            skLineSegment(sketch, "E1155", {"start": v(11.16, -54.4) * mm, "end": v(11.19, -54.42) * mm});
            skLineSegment(sketch, "E1156", {"start": v(11.19, -54.42) * mm, "end": v(11.2, -54.43) * mm});
            skLineSegment(sketch, "E1157", {"start": v(11.2, -54.43) * mm, "end": v(11.24, -54.45) * mm});
            skLineSegment(sketch, "E1158", {"start": v(11.24, -54.45) * mm, "end": v(11.28, -54.47) * mm});
            skLineSegment(sketch, "E1159", {"start": v(11.28, -54.47) * mm, "end": v(11.32, -54.5) * mm});
            skLineSegment(sketch, "E1160", {"start": v(11.32, -54.5) * mm, "end": v(11.36, -54.52) * mm});
            skLineSegment(sketch, "E1161", {"start": v(11.36, -54.52) * mm, "end": v(11.4, -54.54) * mm});
            skLineSegment(sketch, "E1162", {"start": v(11.4, -54.54) * mm, "end": v(11.46, -54.57) * mm});
            skLineSegment(sketch, "E1163", {"start": v(11.46, -54.57) * mm, "end": v(11.5, -54.6) * mm});
            skLineSegment(sketch, "E1164", {"start": v(11.5, -54.6) * mm, "end": v(11.57, -54.63) * mm});
            skLineSegment(sketch, "E1165", {"start": v(11.57, -54.63) * mm, "end": v(11.63, -54.65) * mm});
            skLineSegment(sketch, "E1166", {"start": v(11.63, -54.65) * mm, "end": v(11.69, -54.68) * mm});
            skLineSegment(sketch, "E1167", {"start": v(11.69, -54.68) * mm, "end": v(11.76, -54.71) * mm});
            skLineSegment(sketch, "E1168", {"start": v(11.76, -54.71) * mm, "end": v(11.83, -54.74) * mm});
            skLineSegment(sketch, "E1169", {"start": v(11.83, -54.74) * mm, "end": v(11.9, -54.77) * mm});
            skLineSegment(sketch, "E1170", {"start": v(11.9, -54.77) * mm, "end": v(11.98, -54.8) * mm});
            skLineSegment(sketch, "E1171", {"start": v(11.98, -54.8) * mm, "end": v(12.06, -54.83) * mm});
            skLineSegment(sketch, "E1172", {"start": v(12.06, -54.83) * mm, "end": v(12.14, -54.86) * mm});
            skLineSegment(sketch, "E1173", {"start": v(12.14, -54.86) * mm, "end": v(12.23, -54.88) * mm});
            skLineSegment(sketch, "E1174", {"start": v(12.23, -54.88) * mm, "end": v(12.32, -54.91) * mm});
            skLineSegment(sketch, "E1175", {"start": v(12.32, -54.91) * mm, "end": v(12.38, -54.93) * mm});
            skLineSegment(sketch, "E1176", {"start": v(12.38, -54.93) * mm, "end": v(12.58, -54.73) * mm});
            skLineSegment(sketch, "E1177", {"start": v(12.58, -54.73) * mm, "end": v(12.75, -54.5) * mm});
            skLineSegment(sketch, "E1178", {"start": v(12.75, -54.5) * mm, "end": v(12.72, -54.44) * mm});
            skLineSegment(sketch, "E1179", {"start": v(12.72, -54.44) * mm, "end": v(12.68, -54.36) * mm});
            skLineSegment(sketch, "E1180", {"start": v(12.68, -54.36) * mm, "end": v(12.64, -54.27) * mm});
            skLineSegment(sketch, "E1181", {"start": v(12.64, -54.27) * mm, "end": v(12.6, -54.2) * mm});
            skLineSegment(sketch, "E1182", {"start": v(12.6, -54.2) * mm, "end": v(12.56, -54.12) * mm});
            skLineSegment(sketch, "E1183", {"start": v(12.56, -54.12) * mm, "end": v(12.51, -54.05) * mm});
            skLineSegment(sketch, "E1184", {"start": v(12.51, -54.05) * mm, "end": v(12.47, -53.98) * mm});
            skLineSegment(sketch, "E1185", {"start": v(12.47, -53.98) * mm, "end": v(12.43, -53.92) * mm});
            skLineSegment(sketch, "E1186", {"start": v(12.43, -53.92) * mm, "end": v(12.4, -53.85) * mm});
            skLineSegment(sketch, "E1187", {"start": v(12.4, -53.85) * mm, "end": v(12.36, -53.8) * mm});
            skLineSegment(sketch, "E1188", {"start": v(12.36, -53.8) * mm, "end": v(12.32, -53.74) * mm});
            skLineSegment(sketch, "E1189", {"start": v(12.32, -53.74) * mm, "end": v(12.28, -53.7) * mm});
            skLineSegment(sketch, "E1190", {"start": v(12.28, -53.7) * mm, "end": v(12.25, -53.64) * mm});
            skLineSegment(sketch, "E1191", {"start": v(12.25, -53.64) * mm, "end": v(12.22, -53.6) * mm});
            skLineSegment(sketch, "E1192", {"start": v(12.22, -53.6) * mm, "end": v(12.18, -53.56) * mm});
            skLineSegment(sketch, "E1193", {"start": v(12.18, -53.56) * mm, "end": v(12.15, -53.52) * mm});
            skLineSegment(sketch, "E1194", {"start": v(12.15, -53.52) * mm, "end": v(12.12, -53.48) * mm});
            skLineSegment(sketch, "E1195", {"start": v(12.12, -53.48) * mm, "end": v(12.1, -53.45) * mm});
            skLineSegment(sketch, "E1196", {"start": v(12.1, -53.45) * mm, "end": v(12.07, -53.42) * mm});
            skLineSegment(sketch, "E1197", {"start": v(12.07, -53.42) * mm, "end": v(12.05, -53.4) * mm});
            skLineSegment(sketch, "E1198", {"start": v(12.05, -53.4) * mm, "end": v(12.03, -53.38) * mm});
            skLineSegment(sketch, "E1199", {"start": v(12.03, -53.38) * mm, "end": v(12.01, -53.36) * mm});
            skLineSegment(sketch, "E1200", {"start": v(12.01, -53.36) * mm, "end": v(12, -53.33) * mm});
            skLineSegment(sketch, "E1201", {"start": v(12, -53.33) * mm, "end": v(11.99, -53.31) * mm});
            skLineSegment(sketch, "E1202", {"start": v(11.99, -53.31) * mm, "end": v(11.98, -53.3) * mm});
            skLineSegment(sketch, "E1203", {"start": v(11.98, -53.3) * mm, "end": v(11.98, -53.28) * mm});
            skLineSegment(sketch, "E1204", {"start": v(11.98, -53.28) * mm, "end": v(11.97, -53.26) * mm});
            skLineSegment(sketch, "E1205", {"start": v(11.97, -53.26) * mm, "end": v(11.97, -53.25) * mm});
            skLineSegment(sketch, "E1206", {"start": v(11.97, -53.25) * mm, "end": v(11.98, -53.24) * mm});
            skLineSegment(sketch, "E1207", {"start": v(11.98, -53.24) * mm, "end": v(12.1, -53.08) * mm});
            skLineSegment(sketch, "E1208", {"start": v(12.1, -53.08) * mm, "end": v(12.22, -52.91) * mm});
            skLineSegment(sketch, "E1209", {"start": v(12.22, -52.91) * mm, "end": v(12.33, -52.75) * mm});
            skLineSegment(sketch, "E1210", {"start": v(12.33, -52.75) * mm, "end": v(12.34, -52.75) * mm});
            skLineSegment(sketch, "E1211", {"start": v(12.34, -52.75) * mm, "end": v(12.35, -52.74) * mm});
            skLineSegment(sketch, "E1212", {"start": v(12.35, -52.74) * mm, "end": v(12.37, -52.74) * mm});
            skLineSegment(sketch, "E1213", {"start": v(12.37, -52.74) * mm, "end": v(12.38, -52.74) * mm});
            skLineSegment(sketch, "E1214", {"start": v(12.38, -52.74) * mm, "end": v(12.4, -52.74) * mm});
            skLineSegment(sketch, "E1215", {"start": v(12.4, -52.74) * mm, "end": v(12.43, -52.74) * mm});
            skLineSegment(sketch, "E1216", {"start": v(12.43, -52.74) * mm, "end": v(12.45, -52.75) * mm});
            skLineSegment(sketch, "E1217", {"start": v(12.45, -52.75) * mm, "end": v(12.48, -52.76) * mm});
            skLineSegment(sketch, "E1218", {"start": v(12.48, -52.76) * mm, "end": v(12.51, -52.77) * mm});
            skLineSegment(sketch, "E1219", {"start": v(12.51, -52.77) * mm, "end": v(12.53, -52.78) * mm});
            skLineSegment(sketch, "E1220", {"start": v(12.53, -52.78) * mm, "end": v(12.57, -52.8) * mm});
            skLineSegment(sketch, "E1221", {"start": v(12.57, -52.8) * mm, "end": v(12.6, -52.81) * mm});
            skLineSegment(sketch, "E1222", {"start": v(12.6, -52.81) * mm, "end": v(12.65, -52.83) * mm});
            skLineSegment(sketch, "E1223", {"start": v(12.65, -52.83) * mm, "end": v(12.7, -52.85) * mm});
            skLineSegment(sketch, "E1224", {"start": v(12.7, -52.85) * mm, "end": v(12.75, -52.87) * mm});
            skLineSegment(sketch, "E1225", {"start": v(12.75, -52.87) * mm, "end": v(12.8, -52.89) * mm});
            skLineSegment(sketch, "E1226", {"start": v(12.8, -52.89) * mm, "end": v(12.86, -52.9) * mm});
            skLineSegment(sketch, "E1227", {"start": v(12.86, -52.9) * mm, "end": v(12.92, -52.92) * mm});
            skLineSegment(sketch, "E1228", {"start": v(12.92, -52.92) * mm, "end": v(12.98, -52.94) * mm});
            skLineSegment(sketch, "E1229", {"start": v(12.98, -52.94) * mm, "end": v(13.05, -52.96) * mm});
            skLineSegment(sketch, "E1230", {"start": v(13.05, -52.96) * mm, "end": v(13.12, -52.98) * mm});
            skLineSegment(sketch, "E1231", {"start": v(13.12, -52.98) * mm, "end": v(13.19, -53) * mm});
            skLineSegment(sketch, "E1232", {"start": v(13.19, -53) * mm, "end": v(13.27, -53.01) * mm});
            skLineSegment(sketch, "E1233", {"start": v(13.27, -53.01) * mm, "end": v(13.35, -53.03) * mm});
            skLineSegment(sketch, "E1234", {"start": v(13.35, -53.03) * mm, "end": v(13.43, -53.05) * mm});
            skLineSegment(sketch, "E1235", {"start": v(13.43, -53.05) * mm, "end": v(13.52, -53.06) * mm});
            skLineSegment(sketch, "E1236", {"start": v(13.52, -53.06) * mm, "end": v(13.61, -53.08) * mm});
            skLineSegment(sketch, "E1237", {"start": v(13.61, -53.08) * mm, "end": v(13.7, -53.09) * mm});
            skLineSegment(sketch, "E1238", {"start": v(13.7, -53.09) * mm, "end": v(13.77, -53.1) * mm});
            skLineSegment(sketch, "E1239", {"start": v(13.77, -53.1) * mm, "end": v(13.94, -52.87) * mm});
            skLineSegment(sketch, "E1240", {"start": v(13.94, -52.87) * mm, "end": v(14.06, -52.61) * mm});
            skLineSegment(sketch, "E1241", {"start": v(14.06, -52.61) * mm, "end": v(14.03, -52.56) * mm});
            skLineSegment(sketch, "E1242", {"start": v(14.03, -52.56) * mm, "end": v(13.97, -52.48) * mm});
            skLineSegment(sketch, "E1243", {"start": v(13.97, -52.48) * mm, "end": v(13.92, -52.4) * mm});
            skLineSegment(sketch, "E1244", {"start": v(13.92, -52.4) * mm, "end": v(13.87, -52.34) * mm});
            skLineSegment(sketch, "E1245", {"start": v(13.87, -52.34) * mm, "end": v(13.81, -52.27) * mm});
            skLineSegment(sketch, "E1246", {"start": v(13.81, -52.27) * mm, "end": v(13.76, -52.2) * mm});
            skLineSegment(sketch, "E1247", {"start": v(13.76, -52.2) * mm, "end": v(13.71, -52.14) * mm});
            skLineSegment(sketch, "E1248", {"start": v(13.71, -52.14) * mm, "end": v(13.66, -52.09) * mm});
            skLineSegment(sketch, "E1249", {"start": v(13.66, -52.09) * mm, "end": v(13.61, -52.03) * mm});
            skLineSegment(sketch, "E1250", {"start": v(13.61, -52.03) * mm, "end": v(13.57, -51.98) * mm});
            skLineSegment(sketch, "E1251", {"start": v(13.57, -51.98) * mm, "end": v(13.52, -51.93) * mm});
            skLineSegment(sketch, "E1252", {"start": v(13.52, -51.93) * mm, "end": v(13.48, -51.89) * mm});
            skLineSegment(sketch, "E1253", {"start": v(13.48, -51.89) * mm, "end": v(13.44, -51.84) * mm});
            skLineSegment(sketch, "E1254", {"start": v(13.44, -51.84) * mm, "end": v(13.4, -51.8) * mm});
            skLineSegment(sketch, "E1255", {"start": v(13.4, -51.8) * mm, "end": v(13.36, -51.77) * mm});
            skLineSegment(sketch, "E1256", {"start": v(13.36, -51.77) * mm, "end": v(13.32, -51.74) * mm});
            skLineSegment(sketch, "E1257", {"start": v(13.32, -51.74) * mm, "end": v(13.29, -51.7) * mm});
            skLineSegment(sketch, "E1258", {"start": v(13.29, -51.7) * mm, "end": v(13.25, -51.68) * mm});
            skLineSegment(sketch, "E1259", {"start": v(13.25, -51.68) * mm, "end": v(13.22, -51.65) * mm});
            skLineSegment(sketch, "E1260", {"start": v(13.22, -51.65) * mm, "end": v(13.2, -51.64) * mm});
            skLineSegment(sketch, "E1261", {"start": v(13.2, -51.64) * mm, "end": v(13.18, -51.62) * mm});
            skLineSegment(sketch, "E1262", {"start": v(13.18, -51.62) * mm, "end": v(13.16, -51.6) * mm});
            skLineSegment(sketch, "E1263", {"start": v(13.16, -51.6) * mm, "end": v(13.14, -51.58) * mm});
            skLineSegment(sketch, "E1264", {"start": v(13.14, -51.58) * mm, "end": v(13.13, -51.56) * mm});
            skLineSegment(sketch, "E1265", {"start": v(13.13, -51.56) * mm, "end": v(13.12, -51.54) * mm});
            skLineSegment(sketch, "E1266", {"start": v(13.12, -51.54) * mm, "end": v(13.1, -51.53) * mm});
            skLineSegment(sketch, "E1267", {"start": v(13.1, -51.53) * mm, "end": v(13.1, -51.51) * mm});
            skLineSegment(sketch, "E1268", {"start": v(13.1, -51.51) * mm, "end": v(13.1, -51.5) * mm});
            skLineSegment(sketch, "E1269", {"start": v(13.1, -51.5) * mm, "end": v(13.1, -51.49) * mm});
            skLineSegment(sketch, "E1270", {"start": v(13.1, -51.49) * mm, "end": v(13.2, -51.32) * mm});
            skLineSegment(sketch, "E1271", {"start": v(13.2, -51.32) * mm, "end": v(13.3, -51.13) * mm});
            skLineSegment(sketch, "E1272", {"start": v(13.3, -51.13) * mm, "end": v(13.38, -50.95) * mm});
            skLineSegment(sketch, "E1273", {"start": v(13.38, -50.95) * mm, "end": v(13.39, -50.95) * mm});
            skLineSegment(sketch, "E1274", {"start": v(13.39, -50.95) * mm, "end": v(13.4, -50.94) * mm});
            skLineSegment(sketch, "E1275", {"start": v(13.4, -50.94) * mm, "end": v(13.41, -50.93) * mm});
            skLineSegment(sketch, "E1276", {"start": v(13.41, -50.93) * mm, "end": v(13.43, -50.93) * mm});
            skLineSegment(sketch, "E1277", {"start": v(13.43, -50.93) * mm, "end": v(13.45, -50.93) * mm});
            skLineSegment(sketch, "E1278", {"start": v(13.45, -50.93) * mm, "end": v(13.47, -50.93) * mm});
            skLineSegment(sketch, "E1279", {"start": v(13.47, -50.93) * mm, "end": v(13.5, -50.93) * mm});
            skLineSegment(sketch, "E1280", {"start": v(13.5, -50.93) * mm, "end": v(13.53, -50.94) * mm});
            skLineSegment(sketch, "E1281", {"start": v(13.53, -50.94) * mm, "end": v(13.56, -50.95) * mm});
            skLineSegment(sketch, "E1282", {"start": v(13.56, -50.95) * mm, "end": v(13.58, -50.95) * mm});
            skLineSegment(sketch, "E1283", {"start": v(13.58, -50.95) * mm, "end": v(13.62, -50.96) * mm});
            skLineSegment(sketch, "E1284", {"start": v(13.62, -50.96) * mm, "end": v(13.66, -50.97) * mm});
            skLineSegment(sketch, "E1285", {"start": v(13.66, -50.97) * mm, "end": v(13.7, -50.98) * mm});
            skLineSegment(sketch, "E1286", {"start": v(13.7, -50.98) * mm, "end": v(13.75, -51) * mm});
            skLineSegment(sketch, "E1287", {"start": v(13.75, -51) * mm, "end": v(13.8, -51) * mm});
            skLineSegment(sketch, "E1288", {"start": v(13.8, -51) * mm, "end": v(13.86, -51.01) * mm});
            skLineSegment(sketch, "E1289", {"start": v(13.86, -51.01) * mm, "end": v(13.92, -51.02) * mm});
            skLineSegment(sketch, "E1290", {"start": v(13.92, -51.02) * mm, "end": v(13.98, -51.03) * mm});
            skLineSegment(sketch, "E1291", {"start": v(13.98, -51.03) * mm, "end": v(14.05, -51.04) * mm});
            skLineSegment(sketch, "E1292", {"start": v(14.05, -51.04) * mm, "end": v(14.12, -51.05) * mm});
            skLineSegment(sketch, "E1293", {"start": v(14.12, -51.05) * mm, "end": v(14.19, -51.05) * mm});
            skLineSegment(sketch, "E1294", {"start": v(14.19, -51.05) * mm, "end": v(14.26, -51.06) * mm});
            skLineSegment(sketch, "E1295", {"start": v(14.26, -51.06) * mm, "end": v(14.34, -51.06) * mm});
            skLineSegment(sketch, "E1296", {"start": v(14.34, -51.06) * mm, "end": v(14.43, -51.07) * mm});
            skLineSegment(sketch, "E1297", {"start": v(14.43, -51.07) * mm, "end": v(14.51, -51.07) * mm});
            skLineSegment(sketch, "E1298", {"start": v(14.51, -51.07) * mm, "end": v(14.6, -51.07) * mm});
            skLineSegment(sketch, "E1299", {"start": v(14.6, -51.07) * mm, "end": v(14.7, -51.07) * mm});
            skLineSegment(sketch, "E1300", {"start": v(14.7, -51.07) * mm, "end": v(14.79, -51.07) * mm});
            skLineSegment(sketch, "E1301", {"start": v(14.79, -51.07) * mm, "end": v(14.85, -51.07) * mm});
            skLineSegment(sketch, "E1302", {"start": v(14.85, -51.07) * mm, "end": v(14.98, -50.82) * mm});
            skLineSegment(sketch, "E1303", {"start": v(14.98, -50.82) * mm, "end": v(15.07, -50.54) * mm});
            skLineSegment(sketch, "E1304", {"start": v(15.07, -50.54) * mm, "end": v(15.02, -50.5) * mm});
            skLineSegment(sketch, "E1305", {"start": v(15.02, -50.5) * mm, "end": v(14.96, -50.43) * mm});
            skLineSegment(sketch, "E1306", {"start": v(14.96, -50.43) * mm, "end": v(14.9, -50.36) * mm});
            skLineSegment(sketch, "E1307", {"start": v(14.9, -50.36) * mm, "end": v(14.83, -50.3) * mm});
            skLineSegment(sketch, "E1308", {"start": v(14.83, -50.3) * mm, "end": v(14.77, -50.24) * mm});
            skLineSegment(sketch, "E1309", {"start": v(14.77, -50.24) * mm, "end": v(14.7, -50.19) * mm});
            skLineSegment(sketch, "E1310", {"start": v(14.7, -50.19) * mm, "end": v(14.65, -50.14) * mm});
            skLineSegment(sketch, "E1311", {"start": v(14.65, -50.14) * mm, "end": v(14.59, -50.09) * mm});
            skLineSegment(sketch, "E1312", {"start": v(14.59, -50.09) * mm, "end": v(14.53, -50.04) * mm});
            skLineSegment(sketch, "E1313", {"start": v(14.53, -50.04) * mm, "end": v(14.48, -50) * mm});
            skLineSegment(sketch, "E1314", {"start": v(14.48, -50) * mm, "end": v(14.43, -49.96) * mm});
            skLineSegment(sketch, "E1315", {"start": v(14.43, -49.96) * mm, "end": v(14.38, -49.92) * mm});
            skLineSegment(sketch, "E1316", {"start": v(14.38, -49.92) * mm, "end": v(14.33, -49.88) * mm});
            skLineSegment(sketch, "E1317", {"start": v(14.33, -49.88) * mm, "end": v(14.28, -49.85) * mm});
            skLineSegment(sketch, "E1318", {"start": v(14.28, -49.85) * mm, "end": v(14.24, -49.82) * mm});
            skLineSegment(sketch, "E1319", {"start": v(14.24, -49.82) * mm, "end": v(14.2, -49.8) * mm});
            skLineSegment(sketch, "E1320", {"start": v(14.2, -49.8) * mm, "end": v(14.16, -49.77) * mm});
            skLineSegment(sketch, "E1321", {"start": v(14.16, -49.77) * mm, "end": v(14.12, -49.75) * mm});
            skLineSegment(sketch, "E1322", {"start": v(14.12, -49.75) * mm, "end": v(14.09, -49.73) * mm});
            skLineSegment(sketch, "E1323", {"start": v(14.09, -49.73) * mm, "end": v(14.07, -49.72) * mm});
            skLineSegment(sketch, "E1324", {"start": v(14.07, -49.72) * mm, "end": v(14.04, -49.7) * mm});
            skLineSegment(sketch, "E1325", {"start": v(14.04, -49.7) * mm, "end": v(14.02, -49.68) * mm});
            skLineSegment(sketch, "E1326", {"start": v(14.02, -49.68) * mm, "end": v(14, -49.67) * mm});
            skLineSegment(sketch, "E1327", {"start": v(14, -49.67) * mm, "end": v(13.98, -49.65) * mm});
            skLineSegment(sketch, "E1328", {"start": v(13.98, -49.65) * mm, "end": v(13.97, -49.64) * mm});
            skLineSegment(sketch, "E1329", {"start": v(13.97, -49.64) * mm, "end": v(13.96, -49.62) * mm});
            skLineSegment(sketch, "E1330", {"start": v(13.96, -49.62) * mm, "end": v(13.95, -49.6) * mm});
            skLineSegment(sketch, "E1331", {"start": v(13.95, -49.6) * mm, "end": v(13.95, -49.6) * mm});
            skLineSegment(sketch, "E1332", {"start": v(13.95, -49.6) * mm, "end": v(13.95, -49.58) * mm});
            skLineSegment(sketch, "E1333", {"start": v(13.95, -49.58) * mm, "end": v(14, -49.4) * mm});
            skLineSegment(sketch, "E1334", {"start": v(14, -49.4) * mm, "end": v(14.07, -49.2) * mm});
            skLineSegment(sketch, "E1335", {"start": v(14.07, -49.2) * mm, "end": v(14.13, -49.01) * mm});
            skLineSegment(sketch, "E1336", {"start": v(14.13, -49.01) * mm, "end": v(14.14, -49) * mm});
            skLineSegment(sketch, "E1337", {"start": v(14.14, -49) * mm, "end": v(14.15, -49) * mm});
            skLineSegment(sketch, "E1338", {"start": v(14.15, -49) * mm, "end": v(14.16, -48.99) * mm});
            skLineSegment(sketch, "E1339", {"start": v(14.16, -48.99) * mm, "end": v(14.18, -48.98) * mm});
            skLineSegment(sketch, "E1340", {"start": v(14.18, -48.98) * mm, "end": v(14.2, -48.98) * mm});
            skLineSegment(sketch, "E1341", {"start": v(14.2, -48.98) * mm, "end": v(14.22, -48.98) * mm});
            skLineSegment(sketch, "E1342", {"start": v(14.22, -48.98) * mm, "end": v(14.25, -48.97) * mm});
            skLineSegment(sketch, "E1343", {"start": v(14.25, -48.97) * mm, "end": v(14.28, -48.98) * mm});
            skLineSegment(sketch, "E1344", {"start": v(14.28, -48.98) * mm, "end": v(14.3, -48.98) * mm});
            skLineSegment(sketch, "E1345", {"start": v(14.3, -48.98) * mm, "end": v(14.33, -48.98) * mm});
            skLineSegment(sketch, "E1346", {"start": v(14.33, -48.98) * mm, "end": v(14.37, -48.98) * mm});
            skLineSegment(sketch, "E1347", {"start": v(14.37, -48.98) * mm, "end": v(14.41, -48.99) * mm});
            skLineSegment(sketch, "E1348", {"start": v(14.41, -48.99) * mm, "end": v(14.46, -49) * mm});
            skLineSegment(sketch, "E1349", {"start": v(14.46, -49) * mm, "end": v(14.5, -49) * mm});
            skLineSegment(sketch, "E1350", {"start": v(14.5, -49) * mm, "end": v(14.56, -49) * mm});
            skLineSegment(sketch, "E1351", {"start": v(14.56, -49) * mm, "end": v(14.62, -49) * mm});
            skLineSegment(sketch, "E1352", {"start": v(14.62, -49) * mm, "end": v(14.68, -49) * mm});
            skLineSegment(sketch, "E1353", {"start": v(14.68, -49) * mm, "end": v(14.74, -49) * mm});
            skLineSegment(sketch, "E1354", {"start": v(14.74, -49) * mm, "end": v(14.8, -49) * mm});
            skLineSegment(sketch, "E1355", {"start": v(14.8, -49) * mm, "end": v(14.87, -48.99) * mm});
            skLineSegment(sketch, "E1356", {"start": v(14.87, -48.99) * mm, "end": v(14.95, -48.98) * mm});
            skLineSegment(sketch, "E1357", {"start": v(14.95, -48.98) * mm, "end": v(15.02, -48.98) * mm});
            skLineSegment(sketch, "E1358", {"start": v(15.02, -48.98) * mm, "end": v(15.1, -48.97) * mm});
            skLineSegment(sketch, "E1359", {"start": v(15.1, -48.97) * mm, "end": v(15.18, -48.96) * mm});
            skLineSegment(sketch, "E1360", {"start": v(15.18, -48.96) * mm, "end": v(15.27, -48.95) * mm});
            skLineSegment(sketch, "E1361", {"start": v(15.27, -48.95) * mm, "end": v(15.36, -48.94) * mm});
            skLineSegment(sketch, "E1362", {"start": v(15.36, -48.94) * mm, "end": v(15.45, -48.92) * mm});
            skLineSegment(sketch, "E1363", {"start": v(15.45, -48.92) * mm, "end": v(15.54, -48.9) * mm});
            skLineSegment(sketch, "E1364", {"start": v(15.54, -48.9) * mm, "end": v(15.6, -48.9) * mm});
            skLineSegment(sketch, "E1365", {"start": v(15.6, -48.9) * mm, "end": v(15.7, -48.63) * mm});
            skLineSegment(sketch, "E1366", {"start": v(15.7, -48.63) * mm, "end": v(15.74, -48.34) * mm});
            skLineSegment(sketch, "E1367", {"start": v(15.74, -48.34) * mm, "end": v(15.69, -48.3) * mm});
            skLineSegment(sketch, "E1368", {"start": v(15.69, -48.3) * mm, "end": v(15.6, -48.25) * mm});
            skLineSegment(sketch, "E1369", {"start": v(15.6, -48.25) * mm, "end": v(15.54, -48.2) * mm});
            skLineSegment(sketch, "E1370", {"start": v(15.54, -48.2) * mm, "end": v(15.46, -48.14) * mm});
            skLineSegment(sketch, "E1371", {"start": v(15.46, -48.14) * mm, "end": v(15.4, -48.1) * mm});
            skLineSegment(sketch, "E1372", {"start": v(15.4, -48.1) * mm, "end": v(15.32, -48.05) * mm});
            skLineSegment(sketch, "E1373", {"start": v(15.32, -48.05) * mm, "end": v(15.26, -48) * mm});
            skLineSegment(sketch, "E1374", {"start": v(15.26, -48) * mm, "end": v(15.2, -47.97) * mm});
            skLineSegment(sketch, "E1375", {"start": v(15.2, -47.97) * mm, "end": v(15.13, -47.93) * mm});
            skLineSegment(sketch, "E1376", {"start": v(15.13, -47.93) * mm, "end": v(15.07, -47.9) * mm});
            skLineSegment(sketch, "E1377", {"start": v(15.07, -47.9) * mm, "end": v(15.01, -47.86) * mm});
            skLineSegment(sketch, "E1378", {"start": v(15.01, -47.86) * mm, "end": v(14.95, -47.83) * mm});
            skLineSegment(sketch, "E1379", {"start": v(14.95, -47.83) * mm, "end": v(14.9, -47.8) * mm});
            skLineSegment(sketch, "E1380", {"start": v(14.9, -47.8) * mm, "end": v(14.85, -47.78) * mm});
            skLineSegment(sketch, "E1381", {"start": v(14.85, -47.78) * mm, "end": v(14.8, -47.76) * mm});
            skLineSegment(sketch, "E1382", {"start": v(14.8, -47.76) * mm, "end": v(14.76, -47.74) * mm});
            skLineSegment(sketch, "E1383", {"start": v(14.76, -47.74) * mm, "end": v(14.72, -47.72) * mm});
            skLineSegment(sketch, "E1384", {"start": v(14.72, -47.72) * mm, "end": v(14.68, -47.7) * mm});
            skLineSegment(sketch, "E1385", {"start": v(14.68, -47.7) * mm, "end": v(14.64, -47.7) * mm});
            skLineSegment(sketch, "E1386", {"start": v(14.64, -47.7) * mm, "end": v(14.62, -47.68) * mm});
            skLineSegment(sketch, "E1387", {"start": v(14.62, -47.68) * mm, "end": v(14.59, -47.67) * mm});
            skLineSegment(sketch, "E1388", {"start": v(14.59, -47.67) * mm, "end": v(14.56, -47.66) * mm});
            skLineSegment(sketch, "E1389", {"start": v(14.56, -47.66) * mm, "end": v(14.54, -47.65) * mm});
            skLineSegment(sketch, "E1390", {"start": v(14.54, -47.65) * mm, "end": v(14.52, -47.63) * mm});
            skLineSegment(sketch, "E1391", {"start": v(14.52, -47.63) * mm, "end": v(14.5, -47.62) * mm});
            skLineSegment(sketch, "E1392", {"start": v(14.5, -47.62) * mm, "end": v(14.5, -47.6) * mm});
            skLineSegment(sketch, "E1393", {"start": v(14.5, -47.6) * mm, "end": v(14.48, -47.6) * mm});
            skLineSegment(sketch, "E1394", {"start": v(14.48, -47.6) * mm, "end": v(14.48, -47.58) * mm});
            skLineSegment(sketch, "E1395", {"start": v(14.48, -47.58) * mm, "end": v(14.48, -47.57) * mm});
            skLineSegment(sketch, "E1396", {"start": v(14.48, -47.57) * mm, "end": v(14.51, -47.38) * mm});
            skLineSegment(sketch, "E1397", {"start": v(14.51, -47.38) * mm, "end": v(14.54, -47.17) * mm});
            skLineSegment(sketch, "E1398", {"start": v(14.54, -47.17) * mm, "end": v(14.57, -46.98) * mm});
            skLineSegment(sketch, "E1399", {"start": v(14.57, -46.98) * mm, "end": v(14.58, -46.97) * mm});
            skLineSegment(sketch, "E1400", {"start": v(14.58, -46.97) * mm, "end": v(14.59, -46.96) * mm});
            skLineSegment(sketch, "E1401", {"start": v(14.59, -46.96) * mm, "end": v(14.6, -46.95) * mm});
            skLineSegment(sketch, "E1402", {"start": v(14.6, -46.95) * mm, "end": v(14.61, -46.94) * mm});
            skLineSegment(sketch, "E1403", {"start": v(14.61, -46.94) * mm, "end": v(14.63, -46.93) * mm});
            skLineSegment(sketch, "E1404", {"start": v(14.63, -46.93) * mm, "end": v(14.65, -46.93) * mm});
            skLineSegment(sketch, "E1405", {"start": v(14.65, -46.93) * mm, "end": v(14.68, -46.92) * mm});
            skLineSegment(sketch, "E1406", {"start": v(14.68, -46.92) * mm, "end": v(14.7, -46.92) * mm});
            skLineSegment(sketch, "E1407", {"start": v(14.7, -46.92) * mm, "end": v(14.74, -46.92) * mm});
            skLineSegment(sketch, "E1408", {"start": v(14.74, -46.92) * mm, "end": v(14.76, -46.91) * mm});
            skLineSegment(sketch, "E1409", {"start": v(14.76, -46.91) * mm, "end": v(14.8, -46.91) * mm});
            skLineSegment(sketch, "E1410", {"start": v(14.8, -46.91) * mm, "end": v(14.84, -46.9) * mm});
            skLineSegment(sketch, "E1411", {"start": v(14.84, -46.9) * mm, "end": v(14.9, -46.9) * mm});
            skLineSegment(sketch, "E1412", {"start": v(14.9, -46.9) * mm, "end": v(14.94, -46.9) * mm});
            skLineSegment(sketch, "E1413", {"start": v(14.94, -46.9) * mm, "end": v(15, -46.9) * mm});
            skLineSegment(sketch, "E1414", {"start": v(15, -46.9) * mm, "end": v(15.05, -46.88) * mm});
            skLineSegment(sketch, "E1415", {"start": v(15.05, -46.88) * mm, "end": v(15.1, -46.88) * mm});
            skLineSegment(sketch, "E1416", {"start": v(15.1, -46.88) * mm, "end": v(15.17, -46.86) * mm});
            skLineSegment(sketch, "E1417", {"start": v(15.17, -46.86) * mm, "end": v(15.23, -46.85) * mm});
            skLineSegment(sketch, "E1418", {"start": v(15.23, -46.85) * mm, "end": v(15.3, -46.84) * mm});
            skLineSegment(sketch, "E1419", {"start": v(15.3, -46.84) * mm, "end": v(15.37, -46.82) * mm});
            skLineSegment(sketch, "E1420", {"start": v(15.37, -46.82) * mm, "end": v(15.45, -46.8) * mm});
            skLineSegment(sketch, "E1421", {"start": v(15.45, -46.8) * mm, "end": v(15.52, -46.79) * mm});
            skLineSegment(sketch, "E1422", {"start": v(15.52, -46.79) * mm, "end": v(15.6, -46.76) * mm});
            skLineSegment(sketch, "E1423", {"start": v(15.6, -46.76) * mm, "end": v(15.68, -46.74) * mm});
            skLineSegment(sketch, "E1424", {"start": v(15.68, -46.74) * mm, "end": v(15.77, -46.71) * mm});
            skLineSegment(sketch, "E1425", {"start": v(15.77, -46.71) * mm, "end": v(15.86, -46.68) * mm});
            skLineSegment(sketch, "E1426", {"start": v(15.86, -46.68) * mm, "end": v(15.95, -46.65) * mm});
            skLineSegment(sketch, "E1427", {"start": v(15.95, -46.65) * mm, "end": v(16, -46.63) * mm});
            skLineSegment(sketch, "E1428", {"start": v(16, -46.63) * mm, "end": v(16.05, -46.35) * mm});
            skLineSegment(sketch, "E1429", {"start": v(16.05, -46.35) * mm, "end": v(16.05, -46.07) * mm});
            skLineSegment(sketch, "E1430", {"start": v(16.05, -46.07) * mm, "end": v(16, -46.04) * mm});
            skLineSegment(sketch, "E1431", {"start": v(16, -46.04) * mm, "end": v(15.91, -46) * mm});
            skLineSegment(sketch, "E1432", {"start": v(15.91, -46) * mm, "end": v(15.83, -45.95) * mm});
            skLineSegment(sketch, "E1433", {"start": v(15.83, -45.95) * mm, "end": v(15.75, -45.91) * mm});
            skLineSegment(sketch, "E1434", {"start": v(15.75, -45.91) * mm, "end": v(15.67, -45.87) * mm});
            skLineSegment(sketch, "E1435", {"start": v(15.67, -45.87) * mm, "end": v(15.6, -45.84) * mm});
            skLineSegment(sketch, "E1436", {"start": v(15.6, -45.84) * mm, "end": v(15.52, -45.8) * mm});
            skLineSegment(sketch, "E1437", {"start": v(15.52, -45.8) * mm, "end": v(15.45, -45.78) * mm});
            skLineSegment(sketch, "E1438", {"start": v(15.45, -45.78) * mm, "end": v(15.39, -45.75) * mm});
            skLineSegment(sketch, "E1439", {"start": v(15.39, -45.75) * mm, "end": v(15.32, -45.73) * mm});
            skLineSegment(sketch, "E1440", {"start": v(15.32, -45.73) * mm, "end": v(15.26, -45.7) * mm});
            skLineSegment(sketch, "E1441", {"start": v(15.26, -45.7) * mm, "end": v(15.2, -45.69) * mm});
            skLineSegment(sketch, "E1442", {"start": v(15.2, -45.69) * mm, "end": v(15.14, -45.67) * mm});
            skLineSegment(sketch, "E1443", {"start": v(15.14, -45.67) * mm, "end": v(15.1, -45.65) * mm});
            skLineSegment(sketch, "E1444", {"start": v(15.1, -45.65) * mm, "end": v(15.04, -45.64) * mm});
            skLineSegment(sketch, "E1445", {"start": v(15.04, -45.64) * mm, "end": v(15, -45.62) * mm});
            skLineSegment(sketch, "E1446", {"start": v(15, -45.62) * mm, "end": v(14.95, -45.61) * mm});
            skLineSegment(sketch, "E1447", {"start": v(14.95, -45.61) * mm, "end": v(14.9, -45.6) * mm});
            skLineSegment(sketch, "E1448", {"start": v(14.9, -45.6) * mm, "end": v(14.87, -45.6) * mm});
            skLineSegment(sketch, "E1449", {"start": v(14.87, -45.6) * mm, "end": v(14.85, -45.59) * mm});
            skLineSegment(sketch, "E1450", {"start": v(14.85, -45.59) * mm, "end": v(14.81, -45.58) * mm});
            skLineSegment(sketch, "E1451", {"start": v(14.81, -45.58) * mm, "end": v(14.79, -45.57) * mm});
            skLineSegment(sketch, "E1452", {"start": v(14.79, -45.57) * mm, "end": v(14.76, -45.56) * mm});
            skLineSegment(sketch, "E1453", {"start": v(14.76, -45.56) * mm, "end": v(14.74, -45.55) * mm});
            skLineSegment(sketch, "E1454", {"start": v(14.74, -45.55) * mm, "end": v(14.72, -45.54) * mm});
            skLineSegment(sketch, "E1455", {"start": v(14.72, -45.54) * mm, "end": v(14.7, -45.53) * mm});
            skLineSegment(sketch, "E1456", {"start": v(14.7, -45.53) * mm, "end": v(14.7, -45.52) * mm});
            skLineSegment(sketch, "E1457", {"start": v(14.7, -45.52) * mm, "end": v(14.7, -45.51) * mm});
            skLineSegment(sketch, "E1458", {"start": v(14.7, -45.51) * mm, "end": v(14.69, -45.5) * mm});
            skLineSegment(sketch, "E1459", {"start": v(14.69, -45.5) * mm, "end": v(14.7, -45.3) * mm});
            skLineSegment(sketch, "E1460", {"start": v(14.7, -45.3) * mm, "end": v(14.7, -45.1) * mm});
            skLineSegment(sketch, "E1461", {"start": v(14.7, -45.1) * mm, "end": v(14.69, -44.9) * mm});
            skLineSegment(sketch, "E1462", {"start": v(14.69, -44.9) * mm, "end": v(14.7, -44.89) * mm});
            skLineSegment(sketch, "E1463", {"start": v(14.7, -44.89) * mm, "end": v(14.7, -44.88) * mm});
            skLineSegment(sketch, "E1464", {"start": v(14.7, -44.88) * mm, "end": v(14.7, -44.87) * mm});
            skLineSegment(sketch, "E1465", {"start": v(14.7, -44.87) * mm, "end": v(14.72, -44.86) * mm});
            skLineSegment(sketch, "E1466", {"start": v(14.72, -44.86) * mm, "end": v(14.74, -44.85) * mm});
            skLineSegment(sketch, "E1467", {"start": v(14.74, -44.85) * mm, "end": v(14.76, -44.84) * mm});
            skLineSegment(sketch, "E1468", {"start": v(14.76, -44.84) * mm, "end": v(14.79, -44.83) * mm});
            skLineSegment(sketch, "E1469", {"start": v(14.79, -44.83) * mm, "end": v(14.81, -44.82) * mm});
            skLineSegment(sketch, "E1470", {"start": v(14.81, -44.82) * mm, "end": v(14.85, -44.81) * mm});
            skLineSegment(sketch, "E1471", {"start": v(14.85, -44.81) * mm, "end": v(14.87, -44.8) * mm});
            skLineSegment(sketch, "E1472", {"start": v(14.87, -44.8) * mm, "end": v(14.9, -44.8) * mm});
            skLineSegment(sketch, "E1473", {"start": v(14.9, -44.8) * mm, "end": v(14.95, -44.79) * mm});
            skLineSegment(sketch, "E1474", {"start": v(14.95, -44.79) * mm, "end": v(15, -44.78) * mm});
            skLineSegment(sketch, "E1475", {"start": v(15, -44.78) * mm, "end": v(15.04, -44.76) * mm});
            skLineSegment(sketch, "E1476", {"start": v(15.04, -44.76) * mm, "end": v(15.1, -44.75) * mm});
            skLineSegment(sketch, "E1477", {"start": v(15.1, -44.75) * mm, "end": v(15.14, -44.73) * mm});
            skLineSegment(sketch, "E1478", {"start": v(15.14, -44.73) * mm, "end": v(15.2, -44.71) * mm});
            skLineSegment(sketch, "E1479", {"start": v(15.2, -44.71) * mm, "end": v(15.26, -44.7) * mm});
            skLineSegment(sketch, "E1480", {"start": v(15.26, -44.7) * mm, "end": v(15.32, -44.67) * mm});
            skLineSegment(sketch, "E1481", {"start": v(15.32, -44.67) * mm, "end": v(15.39, -44.65) * mm});
            skLineSegment(sketch, "E1482", {"start": v(15.39, -44.65) * mm, "end": v(15.45, -44.62) * mm});
            skLineSegment(sketch, "E1483", {"start": v(15.45, -44.62) * mm, "end": v(15.52, -44.6) * mm});
            skLineSegment(sketch, "E1484", {"start": v(15.52, -44.6) * mm, "end": v(15.6, -44.56) * mm});
            skLineSegment(sketch, "E1485", {"start": v(15.6, -44.56) * mm, "end": v(15.67, -44.53) * mm});
            skLineSegment(sketch, "E1486", {"start": v(15.67, -44.53) * mm, "end": v(15.75, -44.49) * mm});
            skLineSegment(sketch, "E1487", {"start": v(15.75, -44.49) * mm, "end": v(15.83, -44.45) * mm});
            skLineSegment(sketch, "E1488", {"start": v(15.83, -44.45) * mm, "end": v(15.91, -44.4) * mm});
            skLineSegment(sketch, "E1489", {"start": v(15.91, -44.4) * mm, "end": v(16, -44.36) * mm});
            skLineSegment(sketch, "E1490", {"start": v(16, -44.36) * mm, "end": v(16.05, -44.33) * mm});
            skLineSegment(sketch, "E1491", {"start": v(16.05, -44.33) * mm, "end": v(16.05, -44.05) * mm});
            skLineSegment(sketch, "E1492", {"start": v(16.05, -44.05) * mm, "end": v(16, -43.77) * mm});
            skLineSegment(sketch, "E1493", {"start": v(16, -43.77) * mm, "end": v(15.95, -43.75) * mm});
            skLineSegment(sketch, "E1494", {"start": v(15.95, -43.75) * mm, "end": v(15.86, -43.72) * mm});
            skLineSegment(sketch, "E1495", {"start": v(15.86, -43.72) * mm, "end": v(15.77, -43.69) * mm});
            skLineSegment(sketch, "E1496", {"start": v(15.77, -43.69) * mm, "end": v(15.68, -43.66) * mm});
            skLineSegment(sketch, "E1497", {"start": v(15.68, -43.66) * mm, "end": v(15.6, -43.64) * mm});
            skLineSegment(sketch, "E1498", {"start": v(15.6, -43.64) * mm, "end": v(15.52, -43.62) * mm});
            skLineSegment(sketch, "E1499", {"start": v(15.52, -43.62) * mm, "end": v(15.45, -43.6) * mm});
            skLineSegment(sketch, "E1500", {"start": v(15.45, -43.6) * mm, "end": v(15.37, -43.58) * mm});
            skLineSegment(sketch, "E1501", {"start": v(15.37, -43.58) * mm, "end": v(15.3, -43.56) * mm});
            skLineSegment(sketch, "E1502", {"start": v(15.3, -43.56) * mm, "end": v(15.23, -43.55) * mm});
            skLineSegment(sketch, "E1503", {"start": v(15.23, -43.55) * mm, "end": v(15.17, -43.54) * mm});
            skLineSegment(sketch, "E1504", {"start": v(15.17, -43.54) * mm, "end": v(15.1, -43.52) * mm});
            skLineSegment(sketch, "E1505", {"start": v(15.1, -43.52) * mm, "end": v(15.05, -43.52) * mm});
            skLineSegment(sketch, "E1506", {"start": v(15.05, -43.52) * mm, "end": v(15, -43.5) * mm});
            skLineSegment(sketch, "E1507", {"start": v(15, -43.5) * mm, "end": v(14.94, -43.5) * mm});
            skLineSegment(sketch, "E1508", {"start": v(14.94, -43.5) * mm, "end": v(14.9, -43.5) * mm});
            skLineSegment(sketch, "E1509", {"start": v(14.9, -43.5) * mm, "end": v(14.84, -43.5) * mm});
            skLineSegment(sketch, "E1510", {"start": v(14.84, -43.5) * mm, "end": v(14.8, -43.49) * mm});
            skLineSegment(sketch, "E1511", {"start": v(14.8, -43.49) * mm, "end": v(14.76, -43.49) * mm});
            skLineSegment(sketch, "E1512", {"start": v(14.76, -43.49) * mm, "end": v(14.74, -43.48) * mm});
            skLineSegment(sketch, "E1513", {"start": v(14.74, -43.48) * mm, "end": v(14.7, -43.48) * mm});
            skLineSegment(sketch, "E1514", {"start": v(14.7, -43.48) * mm, "end": v(14.68, -43.48) * mm});
            skLineSegment(sketch, "E1515", {"start": v(14.68, -43.48) * mm, "end": v(14.65, -43.47) * mm});
            skLineSegment(sketch, "E1516", {"start": v(14.65, -43.47) * mm, "end": v(14.63, -43.47) * mm});
            skLineSegment(sketch, "E1517", {"start": v(14.63, -43.47) * mm, "end": v(14.61, -43.46) * mm});
            skLineSegment(sketch, "E1518", {"start": v(14.61, -43.46) * mm, "end": v(14.6, -43.45) * mm});
            skLineSegment(sketch, "E1519", {"start": v(14.6, -43.45) * mm, "end": v(14.59, -43.44) * mm});
            skLineSegment(sketch, "E1520", {"start": v(14.59, -43.44) * mm, "end": v(14.58, -43.43) * mm});
            skLineSegment(sketch, "E1521", {"start": v(14.58, -43.43) * mm, "end": v(14.57, -43.42) * mm});
            skLineSegment(sketch, "E1522", {"start": v(14.57, -43.42) * mm, "end": v(14.54, -43.23) * mm});
            skLineSegment(sketch, "E1523", {"start": v(14.54, -43.23) * mm, "end": v(14.51, -43.02) * mm});
            skLineSegment(sketch, "E1524", {"start": v(14.51, -43.02) * mm, "end": v(14.48, -42.83) * mm});
            skLineSegment(sketch, "E1525", {"start": v(14.48, -42.83) * mm, "end": v(14.48, -42.82) * mm});
            skLineSegment(sketch, "E1526", {"start": v(14.48, -42.82) * mm, "end": v(14.48, -42.8) * mm});
            skLineSegment(sketch, "E1527", {"start": v(14.48, -42.8) * mm, "end": v(14.5, -42.8) * mm});
            skLineSegment(sketch, "E1528", {"start": v(14.5, -42.8) * mm, "end": v(14.5, -42.78) * mm});
            skLineSegment(sketch, "E1529", {"start": v(14.5, -42.78) * mm, "end": v(14.52, -42.77) * mm});
            skLineSegment(sketch, "E1530", {"start": v(14.52, -42.77) * mm, "end": v(14.54, -42.75) * mm});
            skLineSegment(sketch, "E1531", {"start": v(14.54, -42.75) * mm, "end": v(14.56, -42.74) * mm});
            skLineSegment(sketch, "E1532", {"start": v(14.56, -42.74) * mm, "end": v(14.59, -42.73) * mm});
            skLineSegment(sketch, "E1533", {"start": v(14.59, -42.73) * mm, "end": v(14.62, -42.72) * mm});
            skLineSegment(sketch, "E1534", {"start": v(14.62, -42.72) * mm, "end": v(14.64, -42.7) * mm});
            skLineSegment(sketch, "E1535", {"start": v(14.64, -42.7) * mm, "end": v(14.68, -42.7) * mm});
            skLineSegment(sketch, "E1536", {"start": v(14.68, -42.7) * mm, "end": v(14.72, -42.68) * mm});
            skLineSegment(sketch, "E1537", {"start": v(14.72, -42.68) * mm, "end": v(14.76, -42.66) * mm});
            skLineSegment(sketch, "E1538", {"start": v(14.76, -42.66) * mm, "end": v(14.8, -42.64) * mm});
            skLineSegment(sketch, "E1539", {"start": v(14.8, -42.64) * mm, "end": v(14.85, -42.62) * mm});
            skLineSegment(sketch, "E1540", {"start": v(14.85, -42.62) * mm, "end": v(14.9, -42.6) * mm});
            skLineSegment(sketch, "E1541", {"start": v(14.9, -42.6) * mm, "end": v(14.95, -42.57) * mm});
            skLineSegment(sketch, "E1542", {"start": v(14.95, -42.57) * mm, "end": v(15.01, -42.54) * mm});
            skLineSegment(sketch, "E1543", {"start": v(15.01, -42.54) * mm, "end": v(15.07, -42.5) * mm});
            skLineSegment(sketch, "E1544", {"start": v(15.07, -42.5) * mm, "end": v(15.13, -42.47) * mm});
            skLineSegment(sketch, "E1545", {"start": v(15.13, -42.47) * mm, "end": v(15.2, -42.43) * mm});
            skLineSegment(sketch, "E1546", {"start": v(15.2, -42.43) * mm, "end": v(15.26, -42.4) * mm});
            skLineSegment(sketch, "E1547", {"start": v(15.26, -42.4) * mm, "end": v(15.32, -42.35) * mm});
            skLineSegment(sketch, "E1548", {"start": v(15.32, -42.35) * mm, "end": v(15.4, -42.3) * mm});
            skLineSegment(sketch, "E1549", {"start": v(15.4, -42.3) * mm, "end": v(15.46, -42.26) * mm});
            skLineSegment(sketch, "E1550", {"start": v(15.46, -42.26) * mm, "end": v(15.54, -42.2) * mm});
            skLineSegment(sketch, "E1551", {"start": v(15.54, -42.2) * mm, "end": v(15.6, -42.15) * mm});
            skLineSegment(sketch, "E1552", {"start": v(15.6, -42.15) * mm, "end": v(15.69, -42.1) * mm});
            skLineSegment(sketch, "E1553", {"start": v(15.69, -42.1) * mm, "end": v(15.74, -42.06) * mm});
            skLineSegment(sketch, "E1554", {"start": v(15.74, -42.06) * mm, "end": v(15.7, -41.77) * mm});
            skLineSegment(sketch, "E1555", {"start": v(15.7, -41.77) * mm, "end": v(15.6, -41.5) * mm});
            skLineSegment(sketch, "E1556", {"start": v(15.6, -41.5) * mm, "end": v(15.54, -41.5) * mm});
            skLineSegment(sketch, "E1557", {"start": v(15.54, -41.5) * mm, "end": v(15.45, -41.48) * mm});
            skLineSegment(sketch, "E1558", {"start": v(15.45, -41.48) * mm, "end": v(15.36, -41.46) * mm});
            skLineSegment(sketch, "E1559", {"start": v(15.36, -41.46) * mm, "end": v(15.27, -41.45) * mm});
            skLineSegment(sketch, "E1560", {"start": v(15.27, -41.45) * mm, "end": v(15.18, -41.44) * mm});
            skLineSegment(sketch, "E1561", {"start": v(15.18, -41.44) * mm, "end": v(15.1, -41.43) * mm});
            skLineSegment(sketch, "E1562", {"start": v(15.1, -41.43) * mm, "end": v(15.02, -41.42) * mm});
            skLineSegment(sketch, "E1563", {"start": v(15.02, -41.42) * mm, "end": v(14.95, -41.42) * mm});
            skLineSegment(sketch, "E1564", {"start": v(14.95, -41.42) * mm, "end": v(14.87, -41.41) * mm});
            skLineSegment(sketch, "E1565", {"start": v(14.87, -41.41) * mm, "end": v(14.8, -41.4) * mm});
            skLineSegment(sketch, "E1566", {"start": v(14.8, -41.4) * mm, "end": v(14.74, -41.4) * mm});
            skLineSegment(sketch, "E1567", {"start": v(14.74, -41.4) * mm, "end": v(14.68, -41.4) * mm});
            skLineSegment(sketch, "E1568", {"start": v(14.68, -41.4) * mm, "end": v(14.62, -41.4) * mm});
            skLineSegment(sketch, "E1569", {"start": v(14.62, -41.4) * mm, "end": v(14.56, -41.4) * mm});
            skLineSegment(sketch, "E1570", {"start": v(14.56, -41.4) * mm, "end": v(14.5, -41.4) * mm});
            skLineSegment(sketch, "E1571", {"start": v(14.5, -41.4) * mm, "end": v(14.46, -41.4) * mm});
            skLineSegment(sketch, "E1572", {"start": v(14.46, -41.4) * mm, "end": v(14.41, -41.41) * mm});
            skLineSegment(sketch, "E1573", {"start": v(14.41, -41.41) * mm, "end": v(14.37, -41.42) * mm});
            skLineSegment(sketch, "E1574", {"start": v(14.37, -41.42) * mm, "end": v(14.33, -41.42) * mm});
            skLineSegment(sketch, "E1575", {"start": v(14.33, -41.42) * mm, "end": v(14.3, -41.42) * mm});
            skLineSegment(sketch, "E1576", {"start": v(14.3, -41.42) * mm, "end": v(14.28, -41.42) * mm});
            skLineSegment(sketch, "E1577", {"start": v(14.28, -41.42) * mm, "end": v(14.25, -41.43) * mm});
            skLineSegment(sketch, "E1578", {"start": v(14.25, -41.43) * mm, "end": v(14.22, -41.42) * mm});
            skLineSegment(sketch, "E1579", {"start": v(14.22, -41.42) * mm, "end": v(14.2, -41.42) * mm});
            skLineSegment(sketch, "E1580", {"start": v(14.2, -41.42) * mm, "end": v(14.18, -41.42) * mm});
            skLineSegment(sketch, "E1581", {"start": v(14.18, -41.42) * mm, "end": v(14.16, -41.41) * mm});
            skLineSegment(sketch, "E1582", {"start": v(14.16, -41.41) * mm, "end": v(14.15, -41.4) * mm});
            skLineSegment(sketch, "E1583", {"start": v(14.15, -41.4) * mm, "end": v(14.14, -41.4) * mm});
            skLineSegment(sketch, "E1584", {"start": v(14.14, -41.4) * mm, "end": v(14.13, -41.39) * mm});
            skLineSegment(sketch, "E1585", {"start": v(14.13, -41.39) * mm, "end": v(14.07, -41.2) * mm});
            skLineSegment(sketch, "E1586", {"start": v(14.07, -41.2) * mm, "end": v(14, -41) * mm});
            skLineSegment(sketch, "E1587", {"start": v(14, -41) * mm, "end": v(13.95, -40.82) * mm});
            skLineSegment(sketch, "E1588", {"start": v(13.95, -40.82) * mm, "end": v(13.95, -40.8) * mm});
            skLineSegment(sketch, "E1589", {"start": v(13.95, -40.8) * mm, "end": v(13.95, -40.8) * mm});
            skLineSegment(sketch, "E1590", {"start": v(13.95, -40.8) * mm, "end": v(13.96, -40.78) * mm});
            skLineSegment(sketch, "E1591", {"start": v(13.96, -40.78) * mm, "end": v(13.97, -40.76) * mm});
            skLineSegment(sketch, "E1592", {"start": v(13.97, -40.76) * mm, "end": v(13.98, -40.75) * mm});
            skLineSegment(sketch, "E1593", {"start": v(13.98, -40.75) * mm, "end": v(14, -40.73) * mm});
            skLineSegment(sketch, "E1594", {"start": v(14, -40.73) * mm, "end": v(14.02, -40.72) * mm});
            skLineSegment(sketch, "E1595", {"start": v(14.02, -40.72) * mm, "end": v(14.04, -40.7) * mm});
            skLineSegment(sketch, "E1596", {"start": v(14.04, -40.7) * mm, "end": v(14.07, -40.68) * mm});
            skLineSegment(sketch, "E1597", {"start": v(14.07, -40.68) * mm, "end": v(14.09, -40.67) * mm});
            skLineSegment(sketch, "E1598", {"start": v(14.09, -40.67) * mm, "end": v(14.12, -40.65) * mm});
            skLineSegment(sketch, "E1599", {"start": v(14.12, -40.65) * mm, "end": v(14.16, -40.63) * mm});
            skLineSegment(sketch, "E1600", {"start": v(14.16, -40.63) * mm, "end": v(14.2, -40.6) * mm});
            skLineSegment(sketch, "E1601", {"start": v(14.2, -40.6) * mm, "end": v(14.24, -40.58) * mm});
            skLineSegment(sketch, "E1602", {"start": v(14.24, -40.58) * mm, "end": v(14.28, -40.55) * mm});
            skLineSegment(sketch, "E1603", {"start": v(14.28, -40.55) * mm, "end": v(14.33, -40.52) * mm});
            skLineSegment(sketch, "E1604", {"start": v(14.33, -40.52) * mm, "end": v(14.38, -40.48) * mm});
            skLineSegment(sketch, "E1605", {"start": v(14.38, -40.48) * mm, "end": v(14.43, -40.44) * mm});
            skLineSegment(sketch, "E1606", {"start": v(14.43, -40.44) * mm, "end": v(14.48, -40.4) * mm});
            skLineSegment(sketch, "E1607", {"start": v(14.48, -40.4) * mm, "end": v(14.53, -40.36) * mm});
            skLineSegment(sketch, "E1608", {"start": v(14.53, -40.36) * mm, "end": v(14.59, -40.31) * mm});
            skLineSegment(sketch, "E1609", {"start": v(14.59, -40.31) * mm, "end": v(14.65, -40.26) * mm});
            skLineSegment(sketch, "E1610", {"start": v(14.65, -40.26) * mm, "end": v(14.7, -40.21) * mm});
            skLineSegment(sketch, "E1611", {"start": v(14.7, -40.21) * mm, "end": v(14.77, -40.16) * mm});
            skLineSegment(sketch, "E1612", {"start": v(14.77, -40.16) * mm, "end": v(14.83, -40.1) * mm});
            skLineSegment(sketch, "E1613", {"start": v(14.83, -40.1) * mm, "end": v(14.9, -40.04) * mm});
            skLineSegment(sketch, "E1614", {"start": v(14.9, -40.04) * mm, "end": v(14.96, -39.97) * mm});
            skLineSegment(sketch, "E1615", {"start": v(14.96, -39.97) * mm, "end": v(15.02, -39.9) * mm});
            skLineSegment(sketch, "E1616", {"start": v(15.02, -39.9) * mm, "end": v(15.07, -39.86) * mm});
            skLineSegment(sketch, "E1617", {"start": v(15.07, -39.86) * mm, "end": v(14.98, -39.58) * mm});
            skLineSegment(sketch, "E1618", {"start": v(14.98, -39.58) * mm, "end": v(14.85, -39.33) * mm});
            skLineSegment(sketch, "E1619", {"start": v(14.85, -39.33) * mm, "end": v(14.79, -39.33) * mm});
            skLineSegment(sketch, "E1620", {"start": v(14.79, -39.33) * mm, "end": v(14.7, -39.33) * mm});
            skLineSegment(sketch, "E1621", {"start": v(14.7, -39.33) * mm, "end": v(14.6, -39.33) * mm});
            skLineSegment(sketch, "E1622", {"start": v(14.6, -39.33) * mm, "end": v(14.51, -39.33) * mm});
            skLineSegment(sketch, "E1623", {"start": v(14.51, -39.33) * mm, "end": v(14.43, -39.33) * mm});
            skLineSegment(sketch, "E1624", {"start": v(14.43, -39.33) * mm, "end": v(14.34, -39.34) * mm});
            skLineSegment(sketch, "E1625", {"start": v(14.34, -39.34) * mm, "end": v(14.26, -39.34) * mm});
            skLineSegment(sketch, "E1626", {"start": v(14.26, -39.34) * mm, "end": v(14.19, -39.35) * mm});
            skLineSegment(sketch, "E1627", {"start": v(14.19, -39.35) * mm, "end": v(14.12, -39.35) * mm});
            skLineSegment(sketch, "E1628", {"start": v(14.12, -39.35) * mm, "end": v(14.05, -39.36) * mm});
            skLineSegment(sketch, "E1629", {"start": v(14.05, -39.36) * mm, "end": v(13.98, -39.37) * mm});
            skLineSegment(sketch, "E1630", {"start": v(13.98, -39.37) * mm, "end": v(13.92, -39.38) * mm});
            skLineSegment(sketch, "E1631", {"start": v(13.92, -39.38) * mm, "end": v(13.86, -39.39) * mm});
            skLineSegment(sketch, "E1632", {"start": v(13.86, -39.39) * mm, "end": v(13.8, -39.4) * mm});
            skLineSegment(sketch, "E1633", {"start": v(13.8, -39.4) * mm, "end": v(13.75, -39.4) * mm});
            skLineSegment(sketch, "E1634", {"start": v(13.75, -39.4) * mm, "end": v(13.7, -39.42) * mm});
            skLineSegment(sketch, "E1635", {"start": v(13.7, -39.42) * mm, "end": v(13.66, -39.43) * mm});
            skLineSegment(sketch, "E1636", {"start": v(13.66, -39.43) * mm, "end": v(13.62, -39.44) * mm});
            skLineSegment(sketch, "E1637", {"start": v(13.62, -39.44) * mm, "end": v(13.58, -39.45) * mm});
            skLineSegment(sketch, "E1638", {"start": v(13.58, -39.45) * mm, "end": v(13.56, -39.45) * mm});
            skLineSegment(sketch, "E1639", {"start": v(13.56, -39.45) * mm, "end": v(13.53, -39.46) * mm});
            skLineSegment(sketch, "E1640", {"start": v(13.53, -39.46) * mm, "end": v(13.5, -39.47) * mm});
            skLineSegment(sketch, "E1641", {"start": v(13.5, -39.47) * mm, "end": v(13.47, -39.47) * mm});
            skLineSegment(sketch, "E1642", {"start": v(13.47, -39.47) * mm, "end": v(13.45, -39.47) * mm});
            skLineSegment(sketch, "E1643", {"start": v(13.45, -39.47) * mm, "end": v(13.43, -39.47) * mm});
            skLineSegment(sketch, "E1644", {"start": v(13.43, -39.47) * mm, "end": v(13.41, -39.47) * mm});
            skLineSegment(sketch, "E1645", {"start": v(13.41, -39.47) * mm, "end": v(13.4, -39.46) * mm});
            skLineSegment(sketch, "E1646", {"start": v(13.4, -39.46) * mm, "end": v(13.39, -39.45) * mm});
            skLineSegment(sketch, "E1647", {"start": v(13.39, -39.45) * mm, "end": v(13.38, -39.45) * mm});
            skLineSegment(sketch, "E1648", {"start": v(13.38, -39.45) * mm, "end": v(13.3, -39.27) * mm});
            skLineSegment(sketch, "E1649", {"start": v(13.3, -39.27) * mm, "end": v(13.2, -39.08) * mm});
            skLineSegment(sketch, "E1650", {"start": v(13.2, -39.08) * mm, "end": v(13.1, -38.91) * mm});
            skLineSegment(sketch, "E1651", {"start": v(13.1, -38.91) * mm, "end": v(13.1, -38.9) * mm});
            skLineSegment(sketch, "E1652", {"start": v(13.1, -38.9) * mm, "end": v(13.1, -38.89) * mm});
            skLineSegment(sketch, "E1653", {"start": v(13.1, -38.89) * mm, "end": v(13.1, -38.87) * mm});
            skLineSegment(sketch, "E1654", {"start": v(13.1, -38.87) * mm, "end": v(13.12, -38.86) * mm});
            skLineSegment(sketch, "E1655", {"start": v(13.12, -38.86) * mm, "end": v(13.13, -38.84) * mm});
            skLineSegment(sketch, "E1656", {"start": v(13.13, -38.84) * mm, "end": v(13.14, -38.82) * mm});
            skLineSegment(sketch, "E1657", {"start": v(13.14, -38.82) * mm, "end": v(13.16, -38.8) * mm});
            skLineSegment(sketch, "E1658", {"start": v(13.16, -38.8) * mm, "end": v(13.18, -38.78) * mm});
            skLineSegment(sketch, "E1659", {"start": v(13.18, -38.78) * mm, "end": v(13.2, -38.76) * mm});
            skLineSegment(sketch, "E1660", {"start": v(13.2, -38.76) * mm, "end": v(13.22, -38.75) * mm});
            skLineSegment(sketch, "E1661", {"start": v(13.22, -38.75) * mm, "end": v(13.25, -38.72) * mm});
            skLineSegment(sketch, "E1662", {"start": v(13.25, -38.72) * mm, "end": v(13.29, -38.7) * mm});
            skLineSegment(sketch, "E1663", {"start": v(13.29, -38.7) * mm, "end": v(13.32, -38.66) * mm});
            skLineSegment(sketch, "E1664", {"start": v(13.32, -38.66) * mm, "end": v(13.36, -38.63) * mm});
            skLineSegment(sketch, "E1665", {"start": v(13.36, -38.63) * mm, "end": v(13.4, -38.6) * mm});
            skLineSegment(sketch, "E1666", {"start": v(13.4, -38.6) * mm, "end": v(13.44, -38.56) * mm});
            skLineSegment(sketch, "E1667", {"start": v(13.44, -38.56) * mm, "end": v(13.48, -38.51) * mm});
            skLineSegment(sketch, "E1668", {"start": v(13.48, -38.51) * mm, "end": v(13.52, -38.47) * mm});
            skLineSegment(sketch, "E1669", {"start": v(13.52, -38.47) * mm, "end": v(13.57, -38.42) * mm});
            skLineSegment(sketch, "E1670", {"start": v(13.57, -38.42) * mm, "end": v(13.61, -38.37) * mm});
            skLineSegment(sketch, "E1671", {"start": v(13.61, -38.37) * mm, "end": v(13.66, -38.31) * mm});
            skLineSegment(sketch, "E1672", {"start": v(13.66, -38.31) * mm, "end": v(13.71, -38.26) * mm});
            skLineSegment(sketch, "E1673", {"start": v(13.71, -38.26) * mm, "end": v(13.76, -38.2) * mm});
            skLineSegment(sketch, "E1674", {"start": v(13.76, -38.2) * mm, "end": v(13.81, -38.13) * mm});
            skLineSegment(sketch, "E1675", {"start": v(13.81, -38.13) * mm, "end": v(13.87, -38.06) * mm});
            skLineSegment(sketch, "E1676", {"start": v(13.87, -38.06) * mm, "end": v(13.92, -38) * mm});
            skLineSegment(sketch, "E1677", {"start": v(13.92, -38) * mm, "end": v(13.97, -37.92) * mm});
            skLineSegment(sketch, "E1678", {"start": v(13.97, -37.92) * mm, "end": v(14.03, -37.84) * mm});
            skLineSegment(sketch, "E1679", {"start": v(14.03, -37.84) * mm, "end": v(14.06, -37.79) * mm});
            skLineSegment(sketch, "E1680", {"start": v(14.06, -37.79) * mm, "end": v(13.94, -37.53) * mm});
            skLineSegment(sketch, "E1681", {"start": v(13.94, -37.53) * mm, "end": v(13.77, -37.3) * mm});
            skLineSegment(sketch, "E1682", {"start": v(13.77, -37.3) * mm, "end": v(13.7, -37.31) * mm});
            skLineSegment(sketch, "E1683", {"start": v(13.7, -37.31) * mm, "end": v(13.61, -37.32) * mm});
            skLineSegment(sketch, "E1684", {"start": v(13.61, -37.32) * mm, "end": v(13.52, -37.34) * mm});
            skLineSegment(sketch, "E1685", {"start": v(13.52, -37.34) * mm, "end": v(13.43, -37.35) * mm});
            skLineSegment(sketch, "E1686", {"start": v(13.43, -37.35) * mm, "end": v(13.35, -37.37) * mm});
            skLineSegment(sketch, "E1687", {"start": v(13.35, -37.37) * mm, "end": v(13.27, -37.39) * mm});
            skLineSegment(sketch, "E1688", {"start": v(13.27, -37.39) * mm, "end": v(13.19, -37.4) * mm});
            skLineSegment(sketch, "E1689", {"start": v(13.19, -37.4) * mm, "end": v(13.12, -37.42) * mm});
            skLineSegment(sketch, "E1690", {"start": v(13.12, -37.42) * mm, "end": v(13.05, -37.44) * mm});
            skLineSegment(sketch, "E1691", {"start": v(13.05, -37.44) * mm, "end": v(12.98, -37.46) * mm});
            skLineSegment(sketch, "E1692", {"start": v(12.98, -37.46) * mm, "end": v(12.92, -37.48) * mm});
            skLineSegment(sketch, "E1693", {"start": v(12.92, -37.48) * mm, "end": v(12.86, -37.5) * mm});
            skLineSegment(sketch, "E1694", {"start": v(12.86, -37.5) * mm, "end": v(12.8, -37.51) * mm});
            skLineSegment(sketch, "E1695", {"start": v(12.8, -37.51) * mm, "end": v(12.75, -37.53) * mm});
            skLineSegment(sketch, "E1696", {"start": v(12.75, -37.53) * mm, "end": v(12.7, -37.55) * mm});
            skLineSegment(sketch, "E1697", {"start": v(12.7, -37.55) * mm, "end": v(12.65, -37.57) * mm});
            skLineSegment(sketch, "E1698", {"start": v(12.65, -37.57) * mm, "end": v(12.6, -37.59) * mm});
            skLineSegment(sketch, "E1699", {"start": v(12.6, -37.59) * mm, "end": v(12.57, -37.6) * mm});
            skLineSegment(sketch, "E1700", {"start": v(12.57, -37.6) * mm, "end": v(12.53, -37.62) * mm});
            skLineSegment(sketch, "E1701", {"start": v(12.53, -37.62) * mm, "end": v(12.51, -37.63) * mm});
            skLineSegment(sketch, "E1702", {"start": v(12.51, -37.63) * mm, "end": v(12.48, -37.64) * mm});
            skLineSegment(sketch, "E1703", {"start": v(12.48, -37.64) * mm, "end": v(12.45, -37.65) * mm});
            skLineSegment(sketch, "E1704", {"start": v(12.45, -37.65) * mm, "end": v(12.43, -37.66) * mm});
            skLineSegment(sketch, "E1705", {"start": v(12.43, -37.66) * mm, "end": v(12.4, -37.66) * mm});
            skLineSegment(sketch, "E1706", {"start": v(12.4, -37.66) * mm, "end": v(12.38, -37.66) * mm});
            skLineSegment(sketch, "E1707", {"start": v(12.38, -37.66) * mm, "end": v(12.37, -37.66) * mm});
            skLineSegment(sketch, "E1708", {"start": v(12.37, -37.66) * mm, "end": v(12.35, -37.66) * mm});
            skLineSegment(sketch, "E1709", {"start": v(12.35, -37.66) * mm, "end": v(12.34, -37.65) * mm});
            skLineSegment(sketch, "E1710", {"start": v(12.34, -37.65) * mm, "end": v(12.33, -37.65) * mm});
            skLineSegment(sketch, "E1711", {"start": v(12.33, -37.65) * mm, "end": v(12.22, -37.49) * mm});
            skLineSegment(sketch, "E1712", {"start": v(12.22, -37.49) * mm, "end": v(12.1, -37.32) * mm});
            skLineSegment(sketch, "E1713", {"start": v(12.1, -37.32) * mm, "end": v(11.98, -37.16) * mm});
            skLineSegment(sketch, "E1714", {"start": v(11.98, -37.16) * mm, "end": v(11.97, -37.15) * mm});
            skLineSegment(sketch, "E1715", {"start": v(11.97, -37.15) * mm, "end": v(11.97, -37.14) * mm});
            skLineSegment(sketch, "E1716", {"start": v(11.97, -37.14) * mm, "end": v(11.98, -37.12) * mm});
            skLineSegment(sketch, "E1717", {"start": v(11.98, -37.12) * mm, "end": v(11.98, -37.1) * mm});
            skLineSegment(sketch, "E1718", {"start": v(11.98, -37.1) * mm, "end": v(11.99, -37.09) * mm});
            skLineSegment(sketch, "E1719", {"start": v(11.99, -37.09) * mm, "end": v(12, -37.07) * mm});
            skLineSegment(sketch, "E1720", {"start": v(12, -37.07) * mm, "end": v(12.01, -37.04) * mm});
            skLineSegment(sketch, "E1721", {"start": v(12.01, -37.04) * mm, "end": v(12.03, -37.02) * mm});
            skLineSegment(sketch, "E1722", {"start": v(12.03, -37.02) * mm, "end": v(12.05, -37) * mm});
            skLineSegment(sketch, "E1723", {"start": v(12.05, -37) * mm, "end": v(12.07, -36.98) * mm});
            skLineSegment(sketch, "E1724", {"start": v(12.07, -36.98) * mm, "end": v(12.1, -36.95) * mm});
            skLineSegment(sketch, "E1725", {"start": v(12.1, -36.95) * mm, "end": v(12.12, -36.92) * mm});
            skLineSegment(sketch, "E1726", {"start": v(12.12, -36.92) * mm, "end": v(12.15, -36.88) * mm});
            skLineSegment(sketch, "E1727", {"start": v(12.15, -36.88) * mm, "end": v(12.18, -36.84) * mm});
            skLineSegment(sketch, "E1728", {"start": v(12.18, -36.84) * mm, "end": v(12.22, -36.8) * mm});
            skLineSegment(sketch, "E1729", {"start": v(12.22, -36.8) * mm, "end": v(12.25, -36.76) * mm});
            skLineSegment(sketch, "E1730", {"start": v(12.25, -36.76) * mm, "end": v(12.28, -36.7) * mm});
            skLineSegment(sketch, "E1731", {"start": v(12.28, -36.7) * mm, "end": v(12.32, -36.66) * mm});
            skLineSegment(sketch, "E1732", {"start": v(12.32, -36.66) * mm, "end": v(12.36, -36.6) * mm});
            skLineSegment(sketch, "E1733", {"start": v(12.36, -36.6) * mm, "end": v(12.4, -36.55) * mm});
            skLineSegment(sketch, "E1734", {"start": v(12.4, -36.55) * mm, "end": v(12.43, -36.48) * mm});
            skLineSegment(sketch, "E1735", {"start": v(12.43, -36.48) * mm, "end": v(12.47, -36.42) * mm});
            skLineSegment(sketch, "E1736", {"start": v(12.47, -36.42) * mm, "end": v(12.51, -36.35) * mm});
            skLineSegment(sketch, "E1737", {"start": v(12.51, -36.35) * mm, "end": v(12.56, -36.28) * mm});
            skLineSegment(sketch, "E1738", {"start": v(12.56, -36.28) * mm, "end": v(12.6, -36.2) * mm});
            skLineSegment(sketch, "E1739", {"start": v(12.6, -36.2) * mm, "end": v(12.64, -36.13) * mm});
            skLineSegment(sketch, "E1740", {"start": v(12.64, -36.13) * mm, "end": v(12.68, -36.04) * mm});
            skLineSegment(sketch, "E1741", {"start": v(12.68, -36.04) * mm, "end": v(12.72, -35.96) * mm});
            skLineSegment(sketch, "E1742", {"start": v(12.72, -35.96) * mm, "end": v(12.75, -35.9) * mm});
            skLineSegment(sketch, "E1743", {"start": v(12.75, -35.9) * mm, "end": v(12.58, -35.67) * mm});
            skLineSegment(sketch, "E1744", {"start": v(12.58, -35.67) * mm, "end": v(12.38, -35.47) * mm});
            skLineSegment(sketch, "E1745", {"start": v(12.38, -35.47) * mm, "end": v(12.32, -35.49) * mm});
            skLineSegment(sketch, "E1746", {"start": v(12.32, -35.49) * mm, "end": v(12.23, -35.52) * mm});
            skLineSegment(sketch, "E1747", {"start": v(12.23, -35.52) * mm, "end": v(12.14, -35.54) * mm});
            skLineSegment(sketch, "E1748", {"start": v(12.14, -35.54) * mm, "end": v(12.06, -35.57) * mm});
            skLineSegment(sketch, "E1749", {"start": v(12.06, -35.57) * mm, "end": v(11.98, -35.6) * mm});
            skLineSegment(sketch, "E1750", {"start": v(11.98, -35.6) * mm, "end": v(11.9, -35.63) * mm});
            skLineSegment(sketch, "E1751", {"start": v(11.9, -35.63) * mm, "end": v(11.83, -35.66) * mm});
            skLineSegment(sketch, "E1752", {"start": v(11.83, -35.66) * mm, "end": v(11.76, -35.69) * mm});
            skLineSegment(sketch, "E1753", {"start": v(11.76, -35.69) * mm, "end": v(11.69, -35.72) * mm});
            skLineSegment(sketch, "E1754", {"start": v(11.69, -35.72) * mm, "end": v(11.63, -35.75) * mm});
            skLineSegment(sketch, "E1755", {"start": v(11.63, -35.75) * mm, "end": v(11.57, -35.77) * mm});
            skLineSegment(sketch, "E1756", {"start": v(11.57, -35.77) * mm, "end": v(11.5, -35.8) * mm});
            skLineSegment(sketch, "E1757", {"start": v(11.5, -35.8) * mm, "end": v(11.46, -35.83) * mm});
            skLineSegment(sketch, "E1758", {"start": v(11.46, -35.83) * mm, "end": v(11.4, -35.86) * mm});
            skLineSegment(sketch, "E1759", {"start": v(11.4, -35.86) * mm, "end": v(11.36, -35.88) * mm});
            skLineSegment(sketch, "E1760", {"start": v(11.36, -35.88) * mm, "end": v(11.32, -35.9) * mm});
            skLineSegment(sketch, "E1761", {"start": v(11.32, -35.9) * mm, "end": v(11.28, -35.93) * mm});
            skLineSegment(sketch, "E1762", {"start": v(11.28, -35.93) * mm, "end": v(11.24, -35.95) * mm});
            skLineSegment(sketch, "E1763", {"start": v(11.24, -35.95) * mm, "end": v(11.2, -35.97) * mm});
            skLineSegment(sketch, "E1764", {"start": v(11.2, -35.97) * mm, "end": v(11.19, -35.98) * mm});
            skLineSegment(sketch, "E1765", {"start": v(11.19, -35.98) * mm, "end": v(11.16, -36) * mm});
            skLineSegment(sketch, "E1766", {"start": v(11.16, -36) * mm, "end": v(11.14, -36.02) * mm});
            skLineSegment(sketch, "E1767", {"start": v(11.14, -36.02) * mm, "end": v(11.11, -36.03) * mm});
            skLineSegment(sketch, "E1768", {"start": v(11.11, -36.03) * mm, "end": v(11.1, -36.04) * mm});
            skLineSegment(sketch, "E1769", {"start": v(11.1, -36.04) * mm, "end": v(11.07, -36.04) * mm});
            skLineSegment(sketch, "E1770", {"start": v(11.07, -36.04) * mm, "end": v(11.05, -36.04) * mm});
            skLineSegment(sketch, "E1771", {"start": v(11.05, -36.04) * mm, "end": v(11.04, -36.04) * mm});
            skLineSegment(sketch, "E1772", {"start": v(11.04, -36.04) * mm, "end": v(11.03, -36.04) * mm});
            skLineSegment(sketch, "E1773", {"start": v(11.03, -36.04) * mm, "end": v(11.02, -36.03) * mm});
            skLineSegment(sketch, "E1774", {"start": v(11.02, -36.03) * mm, "end": v(10.88, -35.9) * mm});
            skLineSegment(sketch, "E1775", {"start": v(10.88, -35.9) * mm, "end": v(10.73, -35.75) * mm});
            skLineSegment(sketch, "E1776", {"start": v(10.73, -35.75) * mm, "end": v(10.6, -35.6) * mm});
            skLineSegment(sketch, "E1777", {"start": v(10.6, -35.6) * mm, "end": v(10.59, -35.6) * mm});
            skLineSegment(sketch, "E1778", {"start": v(10.59, -35.6) * mm, "end": v(10.58, -35.59) * mm});
            skLineSegment(sketch, "E1779", {"start": v(10.58, -35.59) * mm, "end": v(10.58, -35.57) * mm});
            skLineSegment(sketch, "E1780", {"start": v(10.58, -35.57) * mm, "end": v(10.58, -35.55) * mm});
            skLineSegment(sketch, "E1781", {"start": v(10.58, -35.55) * mm, "end": v(10.59, -35.53) * mm});
            skLineSegment(sketch, "E1782", {"start": v(10.59, -35.53) * mm, "end": v(10.6, -35.51) * mm});
            skLineSegment(sketch, "E1783", {"start": v(10.6, -35.51) * mm, "end": v(10.6, -35.49) * mm});
            skLineSegment(sketch, "E1784", {"start": v(10.6, -35.49) * mm, "end": v(10.62, -35.46) * mm});
            skLineSegment(sketch, "E1785", {"start": v(10.62, -35.46) * mm, "end": v(10.64, -35.44) * mm});
            skLineSegment(sketch, "E1786", {"start": v(10.64, -35.44) * mm, "end": v(10.65, -35.42) * mm});
            skLineSegment(sketch, "E1787", {"start": v(10.65, -35.42) * mm, "end": v(10.67, -35.38) * mm});
            skLineSegment(sketch, "E1788", {"start": v(10.67, -35.38) * mm, "end": v(10.7, -35.35) * mm});
            skLineSegment(sketch, "E1789", {"start": v(10.7, -35.35) * mm, "end": v(10.72, -35.3) * mm});
            skLineSegment(sketch, "E1790", {"start": v(10.72, -35.3) * mm, "end": v(10.74, -35.26) * mm});
            skLineSegment(sketch, "E1791", {"start": v(10.74, -35.26) * mm, "end": v(10.77, -35.22) * mm});
            skLineSegment(sketch, "E1792", {"start": v(10.77, -35.22) * mm, "end": v(10.8, -35.17) * mm});
            skLineSegment(sketch, "E1793", {"start": v(10.8, -35.17) * mm, "end": v(10.82, -35.12) * mm});
            skLineSegment(sketch, "E1794", {"start": v(10.82, -35.12) * mm, "end": v(10.85, -35.06) * mm});
            skLineSegment(sketch, "E1795", {"start": v(10.85, -35.06) * mm, "end": v(10.88, -35) * mm});
            skLineSegment(sketch, "E1796", {"start": v(10.88, -35) * mm, "end": v(10.9, -34.94) * mm});
            skLineSegment(sketch, "E1797", {"start": v(10.9, -34.94) * mm, "end": v(10.94, -34.87) * mm});
            skLineSegment(sketch, "E1798", {"start": v(10.94, -34.87) * mm, "end": v(10.96, -34.8) * mm});
            skLineSegment(sketch, "E1799", {"start": v(10.96, -34.8) * mm, "end": v(11, -34.73) * mm});
            skLineSegment(sketch, "E1800", {"start": v(11, -34.73) * mm, "end": v(11.02, -34.65) * mm});
            skLineSegment(sketch, "E1801", {"start": v(11.02, -34.65) * mm, "end": v(11.05, -34.57) * mm});
            skLineSegment(sketch, "E1802", {"start": v(11.05, -34.57) * mm, "end": v(11.08, -34.48) * mm});
            skLineSegment(sketch, "E1803", {"start": v(11.08, -34.48) * mm, "end": v(11.1, -34.4) * mm});
            skLineSegment(sketch, "E1804", {"start": v(11.1, -34.4) * mm, "end": v(11.14, -34.3) * mm});
            skLineSegment(sketch, "E1805", {"start": v(11.14, -34.3) * mm, "end": v(11.16, -34.24) * mm});
            skLineSegment(sketch, "E1806", {"start": v(11.16, -34.24) * mm, "end": v(10.95, -34.04) * mm});
            skLineSegment(sketch, "E1807", {"start": v(10.95, -34.04) * mm, "end": v(10.72, -33.88) * mm});
            skLineSegment(sketch, "E1808", {"start": v(10.72, -33.88) * mm, "end": v(10.67, -33.9) * mm});
            skLineSegment(sketch, "E1809", {"start": v(10.67, -33.9) * mm, "end": v(10.58, -33.94) * mm});
            skLineSegment(sketch, "E1810", {"start": v(10.58, -33.94) * mm, "end": v(10.5, -33.99) * mm});
            skLineSegment(sketch, "E1811", {"start": v(10.5, -33.99) * mm, "end": v(10.42, -34.03) * mm});
            skLineSegment(sketch, "E1812", {"start": v(10.42, -34.03) * mm, "end": v(10.34, -34.07) * mm});
            skLineSegment(sketch, "E1813", {"start": v(10.34, -34.07) * mm, "end": v(10.27, -34.11) * mm});
            skLineSegment(sketch, "E1814", {"start": v(10.27, -34.11) * mm, "end": v(10.2, -34.15) * mm});
            skLineSegment(sketch, "E1815", {"start": v(10.2, -34.15) * mm, "end": v(10.14, -34.2) * mm});
            skLineSegment(sketch, "E1816", {"start": v(10.14, -34.2) * mm, "end": v(10.08, -34.23) * mm});
            skLineSegment(sketch, "E1817", {"start": v(10.08, -34.23) * mm, "end": v(10.02, -34.27) * mm});
            skLineSegment(sketch, "E1818", {"start": v(10.02, -34.27) * mm, "end": v(9.97, -34.3) * mm});
            skLineSegment(sketch, "E1819", {"start": v(9.97, -34.3) * mm, "end": v(9.91, -34.34) * mm});
            skLineSegment(sketch, "E1820", {"start": v(9.91, -34.34) * mm, "end": v(9.87, -34.38) * mm});
            skLineSegment(sketch, "E1821", {"start": v(9.87, -34.38) * mm, "end": v(9.82, -34.4) * mm});
            skLineSegment(sketch, "E1822", {"start": v(9.82, -34.4) * mm, "end": v(9.78, -34.44) * mm});
            skLineSegment(sketch, "E1823", {"start": v(9.78, -34.44) * mm, "end": v(9.74, -34.47) * mm});
            skLineSegment(sketch, "E1824", {"start": v(9.74, -34.47) * mm, "end": v(9.7, -34.5) * mm});
            skLineSegment(sketch, "E1825", {"start": v(9.7, -34.5) * mm, "end": v(9.67, -34.53) * mm});
            skLineSegment(sketch, "E1826", {"start": v(9.67, -34.53) * mm, "end": v(9.64, -34.56) * mm});
            skLineSegment(sketch, "E1827", {"start": v(9.64, -34.56) * mm, "end": v(9.63, -34.57) * mm});
            skLineSegment(sketch, "E1828", {"start": v(9.63, -34.57) * mm, "end": v(9.6, -34.6) * mm});
            skLineSegment(sketch, "E1829", {"start": v(9.6, -34.6) * mm, "end": v(9.58, -34.6) * mm});
            skLineSegment(sketch, "E1830", {"start": v(9.58, -34.6) * mm, "end": v(9.56, -34.62) * mm});
            skLineSegment(sketch, "E1831", {"start": v(9.56, -34.62) * mm, "end": v(9.54, -34.64) * mm});
            skLineSegment(sketch, "E1832", {"start": v(9.54, -34.64) * mm, "end": v(9.52, -34.64) * mm});
            skLineSegment(sketch, "E1833", {"start": v(9.52, -34.64) * mm, "end": v(9.5, -34.65) * mm});
            skLineSegment(sketch, "E1834", {"start": v(9.5, -34.65) * mm, "end": v(9.49, -34.65) * mm});
            skLineSegment(sketch, "E1835", {"start": v(9.49, -34.65) * mm, "end": v(9.47, -34.65) * mm});
            skLineSegment(sketch, "E1836", {"start": v(9.47, -34.65) * mm, "end": v(9.46, -34.65) * mm});
            skLineSegment(sketch, "E1837", {"start": v(9.46, -34.65) * mm, "end": v(9.3, -34.53) * mm});
            skLineSegment(sketch, "E1838", {"start": v(9.3, -34.53) * mm, "end": v(9.14, -34.4) * mm});
            skLineSegment(sketch, "E1839", {"start": v(9.14, -34.4) * mm, "end": v(8.98, -34.3) * mm});
            skLineSegment(sketch, "E1840", {"start": v(8.98, -34.3) * mm, "end": v(8.97, -34.28) * mm});
            skLineSegment(sketch, "E1841", {"start": v(8.97, -34.28) * mm, "end": v(8.97, -34.27) * mm});
            skLineSegment(sketch, "E1842", {"start": v(8.97, -34.27) * mm, "end": v(8.96, -34.26) * mm});
            skLineSegment(sketch, "E1843", {"start": v(8.96, -34.26) * mm, "end": v(8.96, -34.24) * mm});
            skLineSegment(sketch, "E1844", {"start": v(8.96, -34.24) * mm, "end": v(8.96, -34.22) * mm});
            skLineSegment(sketch, "E1845", {"start": v(8.96, -34.22) * mm, "end": v(8.97, -34.2) * mm});
            skLineSegment(sketch, "E1846", {"start": v(8.97, -34.2) * mm, "end": v(8.98, -34.17) * mm});
            skLineSegment(sketch, "E1847", {"start": v(8.98, -34.17) * mm, "end": v(8.99, -34.14) * mm});
            skLineSegment(sketch, "E1848", {"start": v(8.99, -34.14) * mm, "end": v(9, -34.11) * mm});
            skLineSegment(sketch, "E1849", {"start": v(9, -34.11) * mm, "end": v(9, -34.1) * mm});
            skLineSegment(sketch, "E1850", {"start": v(9, -34.1) * mm, "end": v(9.02, -34.06) * mm});
            skLineSegment(sketch, "E1851", {"start": v(9.02, -34.06) * mm, "end": v(9.04, -34.02) * mm});
            skLineSegment(sketch, "E1852", {"start": v(9.04, -34.02) * mm, "end": v(9.06, -33.98) * mm});
            skLineSegment(sketch, "E1853", {"start": v(9.06, -33.98) * mm, "end": v(9.07, -33.93) * mm});
            skLineSegment(sketch, "E1854", {"start": v(9.07, -33.93) * mm, "end": v(9.1, -33.88) * mm});
            skLineSegment(sketch, "E1855", {"start": v(9.1, -33.88) * mm, "end": v(9.11, -33.83) * mm});
            skLineSegment(sketch, "E1856", {"start": v(9.11, -33.83) * mm, "end": v(9.13, -33.77) * mm});
            skLineSegment(sketch, "E1857", {"start": v(9.13, -33.77) * mm, "end": v(9.15, -33.7) * mm});
            skLineSegment(sketch, "E1858", {"start": v(9.15, -33.7) * mm, "end": v(9.17, -33.65) * mm});
            skLineSegment(sketch, "E1859", {"start": v(9.17, -33.65) * mm, "end": v(9.18, -33.58) * mm});
            skLineSegment(sketch, "E1860", {"start": v(9.18, -33.58) * mm, "end": v(9.2, -33.5) * mm});
            skLineSegment(sketch, "E1861", {"start": v(9.2, -33.5) * mm, "end": v(9.22, -33.44) * mm});
            skLineSegment(sketch, "E1862", {"start": v(9.22, -33.44) * mm, "end": v(9.24, -33.36) * mm});
            skLineSegment(sketch, "E1863", {"start": v(9.24, -33.36) * mm, "end": v(9.25, -33.28) * mm});
            skLineSegment(sketch, "E1864", {"start": v(9.25, -33.28) * mm, "end": v(9.27, -33.2) * mm});
            skLineSegment(sketch, "E1865", {"start": v(9.27, -33.2) * mm, "end": v(9.29, -33.1) * mm});
            skLineSegment(sketch, "E1866", {"start": v(9.29, -33.1) * mm, "end": v(9.3, -33.01) * mm});
            skLineSegment(sketch, "E1867", {"start": v(9.3, -33.01) * mm, "end": v(9.31, -32.92) * mm});
            skLineSegment(sketch, "E1868", {"start": v(9.31, -32.92) * mm, "end": v(9.32, -32.86) * mm});
            skLineSegment(sketch, "E1869", {"start": v(9.32, -32.86) * mm, "end": v(9.1, -32.69) * mm});
            skLineSegment(sketch, "E1870", {"start": v(9.1, -32.69) * mm, "end": v(8.84, -32.56) * mm});
            skLineSegment(sketch, "E1871", {"start": v(8.84, -32.56) * mm, "end": v(8.78, -32.6) * mm});
            skLineSegment(sketch, "E1872", {"start": v(8.78, -32.6) * mm, "end": v(8.7, -32.65) * mm});
            skLineSegment(sketch, "E1873", {"start": v(8.7, -32.65) * mm, "end": v(8.63, -32.7) * mm});
            skLineSegment(sketch, "E1874", {"start": v(8.63, -32.7) * mm, "end": v(8.56, -32.76) * mm});
            skLineSegment(sketch, "E1875", {"start": v(8.56, -32.76) * mm, "end": v(8.5, -32.81) * mm});
            skLineSegment(sketch, "E1876", {"start": v(8.5, -32.81) * mm, "end": v(8.43, -32.86) * mm});
            skLineSegment(sketch, "E1877", {"start": v(8.43, -32.86) * mm, "end": v(8.37, -32.91) * mm});
            skLineSegment(sketch, "E1878", {"start": v(8.37, -32.91) * mm, "end": v(8.31, -32.96) * mm});
            skLineSegment(sketch, "E1879", {"start": v(8.31, -32.96) * mm, "end": v(8.26, -33.01) * mm});
            skLineSegment(sketch, "E1880", {"start": v(8.26, -33.01) * mm, "end": v(8.2, -33.06) * mm});
            skLineSegment(sketch, "E1881", {"start": v(8.2, -33.06) * mm, "end": v(8.16, -33.1) * mm});
            skLineSegment(sketch, "E1882", {"start": v(8.16, -33.1) * mm, "end": v(8.11, -33.15) * mm});
            skLineSegment(sketch, "E1883", {"start": v(8.11, -33.15) * mm, "end": v(8.07, -33.19) * mm});
            skLineSegment(sketch, "E1884", {"start": v(8.07, -33.19) * mm, "end": v(8.03, -33.23) * mm});
            skLineSegment(sketch, "E1885", {"start": v(8.03, -33.23) * mm, "end": v(8, -33.27) * mm});
            skLineSegment(sketch, "E1886", {"start": v(8, -33.27) * mm, "end": v(7.96, -33.3) * mm});
            skLineSegment(sketch, "E1887", {"start": v(7.96, -33.3) * mm, "end": v(7.93, -33.34) * mm});
            skLineSegment(sketch, "E1888", {"start": v(7.93, -33.34) * mm, "end": v(7.9, -33.37) * mm});
            skLineSegment(sketch, "E1889", {"start": v(7.9, -33.37) * mm, "end": v(7.88, -33.4) * mm});
            skLineSegment(sketch, "E1890", {"start": v(7.88, -33.4) * mm, "end": v(7.86, -33.42) * mm});
            skLineSegment(sketch, "E1891", {"start": v(7.86, -33.42) * mm, "end": v(7.84, -33.44) * mm});
            skLineSegment(sketch, "E1892", {"start": v(7.84, -33.44) * mm, "end": v(7.82, -33.46) * mm});
            skLineSegment(sketch, "E1893", {"start": v(7.82, -33.46) * mm, "end": v(7.8, -33.48) * mm});
            skLineSegment(sketch, "E1894", {"start": v(7.8, -33.48) * mm, "end": v(7.79, -33.5) * mm});
            skLineSegment(sketch, "E1895", {"start": v(7.79, -33.5) * mm, "end": v(7.77, -33.5) * mm});
            skLineSegment(sketch, "E1896", {"start": v(7.77, -33.5) * mm, "end": v(7.75, -33.52) * mm});
            skLineSegment(sketch, "E1897", {"start": v(7.75, -33.52) * mm, "end": v(7.74, -33.52) * mm});
            skLineSegment(sketch, "E1898", {"start": v(7.74, -33.52) * mm, "end": v(7.73, -33.52) * mm});
            skLineSegment(sketch, "E1899", {"start": v(7.73, -33.52) * mm, "end": v(7.71, -33.52) * mm});
            skLineSegment(sketch, "E1900", {"start": v(7.71, -33.52) * mm, "end": v(7.54, -33.43) * mm});
            skLineSegment(sketch, "E1901", {"start": v(7.54, -33.43) * mm, "end": v(7.35, -33.33) * mm});
            skLineSegment(sketch, "E1902", {"start": v(7.35, -33.33) * mm, "end": v(7.18, -33.25) * mm});
            skLineSegment(sketch, "E1903", {"start": v(7.18, -33.25) * mm, "end": v(7.17, -33.24) * mm});
            skLineSegment(sketch, "E1904", {"start": v(7.17, -33.24) * mm, "end": v(7.16, -33.23) * mm});
            skLineSegment(sketch, "E1905", {"start": v(7.16, -33.23) * mm, "end": v(7.16, -33.21) * mm});
            skLineSegment(sketch, "E1906", {"start": v(7.16, -33.21) * mm, "end": v(7.16, -33.2) * mm});
            skLineSegment(sketch, "E1907", {"start": v(7.16, -33.2) * mm, "end": v(7.15, -33.18) * mm});
            skLineSegment(sketch, "E1908", {"start": v(7.15, -33.18) * mm, "end": v(7.16, -33.15) * mm});
            skLineSegment(sketch, "E1909", {"start": v(7.16, -33.15) * mm, "end": v(7.16, -33.13) * mm});
            skLineSegment(sketch, "E1910", {"start": v(7.16, -33.13) * mm, "end": v(7.16, -33.1) * mm});
            skLineSegment(sketch, "E1911", {"start": v(7.16, -33.1) * mm, "end": v(7.17, -33.07) * mm});
            skLineSegment(sketch, "E1912", {"start": v(7.17, -33.07) * mm, "end": v(7.18, -33.05) * mm});
            skLineSegment(sketch, "E1913", {"start": v(7.18, -33.05) * mm, "end": v(7.19, -33) * mm});
            skLineSegment(sketch, "E1914", {"start": v(7.19, -33) * mm, "end": v(7.2, -32.97) * mm});
            skLineSegment(sketch, "E1915", {"start": v(7.2, -32.97) * mm, "end": v(7.2, -32.92) * mm});
            skLineSegment(sketch, "E1916", {"start": v(7.2, -32.92) * mm, "end": v(7.22, -32.87) * mm});
            skLineSegment(sketch, "E1917", {"start": v(7.22, -32.87) * mm, "end": v(7.23, -32.82) * mm});
            skLineSegment(sketch, "E1918", {"start": v(7.23, -32.82) * mm, "end": v(7.24, -32.76) * mm});
            skLineSegment(sketch, "E1919", {"start": v(7.24, -32.76) * mm, "end": v(7.25, -32.7) * mm});
            skLineSegment(sketch, "E1920", {"start": v(7.25, -32.7) * mm, "end": v(7.25, -32.64) * mm});
            skLineSegment(sketch, "E1921", {"start": v(7.25, -32.64) * mm, "end": v(7.26, -32.58) * mm});
            skLineSegment(sketch, "E1922", {"start": v(7.26, -32.58) * mm, "end": v(7.27, -32.5) * mm});
            skLineSegment(sketch, "E1923", {"start": v(7.27, -32.5) * mm, "end": v(7.28, -32.44) * mm});
            skLineSegment(sketch, "E1924", {"start": v(7.28, -32.44) * mm, "end": v(7.28, -32.36) * mm});
            skLineSegment(sketch, "E1925", {"start": v(7.28, -32.36) * mm, "end": v(7.29, -32.28) * mm});
            skLineSegment(sketch, "E1926", {"start": v(7.29, -32.28) * mm, "end": v(7.3, -32.2) * mm});
            skLineSegment(sketch, "E1927", {"start": v(7.3, -32.2) * mm, "end": v(7.3, -32.11) * mm});
            skLineSegment(sketch, "E1928", {"start": v(7.3, -32.11) * mm, "end": v(7.3, -32.02) * mm});
            skLineSegment(sketch, "E1929", {"start": v(7.3, -32.02) * mm, "end": v(7.3, -31.93) * mm});
            skLineSegment(sketch, "E1930", {"start": v(7.3, -31.93) * mm, "end": v(7.3, -31.84) * mm});
            skLineSegment(sketch, "E1931", {"start": v(7.3, -31.84) * mm, "end": v(7.3, -31.77) * mm});
            skLineSegment(sketch, "E1932", {"start": v(7.3, -31.77) * mm, "end": v(7.04, -31.64) * mm});
            skLineSegment(sketch, "E1933", {"start": v(7.04, -31.64) * mm, "end": v(6.77, -31.56) * mm});
            skLineSegment(sketch, "E1934", {"start": v(6.77, -31.56) * mm, "end": v(6.72, -31.6) * mm});
            skLineSegment(sketch, "E1935", {"start": v(6.72, -31.6) * mm, "end": v(6.65, -31.67) * mm});
            skLineSegment(sketch, "E1936", {"start": v(6.65, -31.67) * mm, "end": v(6.59, -31.73) * mm});
            skLineSegment(sketch, "E1937", {"start": v(6.59, -31.73) * mm, "end": v(6.53, -31.8) * mm});
            skLineSegment(sketch, "E1938", {"start": v(6.53, -31.8) * mm, "end": v(6.47, -31.86) * mm});
            skLineSegment(sketch, "E1939", {"start": v(6.47, -31.86) * mm, "end": v(6.41, -31.92) * mm});
            skLineSegment(sketch, "E1940", {"start": v(6.41, -31.92) * mm, "end": v(6.36, -31.98) * mm});
            skLineSegment(sketch, "E1941", {"start": v(6.36, -31.98) * mm, "end": v(6.31, -32.04) * mm});
            skLineSegment(sketch, "E1942", {"start": v(6.31, -32.04) * mm, "end": v(6.27, -32.1) * mm});
            skLineSegment(sketch, "E1943", {"start": v(6.27, -32.1) * mm, "end": v(6.22, -32.15) * mm});
            skLineSegment(sketch, "E1944", {"start": v(6.22, -32.15) * mm, "end": v(6.18, -32.2) * mm});
            skLineSegment(sketch, "E1945", {"start": v(6.18, -32.2) * mm, "end": v(6.14, -32.25) * mm});
            skLineSegment(sketch, "E1946", {"start": v(6.14, -32.25) * mm, "end": v(6.1, -32.3) * mm});
            skLineSegment(sketch, "E1947", {"start": v(6.1, -32.3) * mm, "end": v(6.08, -32.34) * mm});
            skLineSegment(sketch, "E1948", {"start": v(6.08, -32.34) * mm, "end": v(6.05, -32.39) * mm});
            skLineSegment(sketch, "E1949", {"start": v(6.05, -32.39) * mm, "end": v(6.02, -32.43) * mm});
            skLineSegment(sketch, "E1950", {"start": v(6.02, -32.43) * mm, "end": v(6, -32.47) * mm});
            skLineSegment(sketch, "E1951", {"start": v(6, -32.47) * mm, "end": v(5.97, -32.5) * mm});
            skLineSegment(sketch, "E1952", {"start": v(5.97, -32.5) * mm, "end": v(5.95, -32.54) * mm});
            skLineSegment(sketch, "E1953", {"start": v(5.95, -32.54) * mm, "end": v(5.94, -32.56) * mm});
            skLineSegment(sketch, "E1954", {"start": v(5.94, -32.56) * mm, "end": v(5.92, -32.58) * mm});
            skLineSegment(sketch, "E1955", {"start": v(5.92, -32.58) * mm, "end": v(5.9, -32.6) * mm});
            skLineSegment(sketch, "E1956", {"start": v(5.9, -32.6) * mm, "end": v(5.9, -32.63) * mm});
            skLineSegment(sketch, "E1957", {"start": v(5.9, -32.63) * mm, "end": v(5.88, -32.65) * mm});
            skLineSegment(sketch, "E1958", {"start": v(5.88, -32.65) * mm, "end": v(5.86, -32.66) * mm});
            skLineSegment(sketch, "E1959", {"start": v(5.86, -32.66) * mm, "end": v(5.85, -32.67) * mm});
            skLineSegment(sketch, "E1960", {"start": v(5.85, -32.67) * mm, "end": v(5.83, -32.68) * mm});
            skLineSegment(sketch, "E1961", {"start": v(5.83, -32.68) * mm, "end": v(5.82, -32.68) * mm});
            skLineSegment(sketch, "E1962", {"start": v(5.82, -32.68) * mm, "end": v(5.8, -32.68) * mm});
            skLineSegment(sketch, "E1963", {"start": v(5.8, -32.68) * mm, "end": v(5.62, -32.61) * mm});
            skLineSegment(sketch, "E1964", {"start": v(5.62, -32.61) * mm, "end": v(5.43, -32.55) * mm});
            skLineSegment(sketch, "E1965", {"start": v(5.43, -32.55) * mm, "end": v(5.24, -32.5) * mm});
            skLineSegment(sketch, "E1966", {"start": v(5.24, -32.5) * mm, "end": v(5.23, -32.49) * mm});
            skLineSegment(sketch, "E1967", {"start": v(5.23, -32.49) * mm, "end": v(5.22, -32.48) * mm});
            skLineSegment(sketch, "E1968", {"start": v(5.22, -32.48) * mm, "end": v(5.21, -32.46) * mm});
            skLineSegment(sketch, "E1969", {"start": v(5.21, -32.46) * mm, "end": v(5.2, -32.45) * mm});
            skLineSegment(sketch, "E1970", {"start": v(5.2, -32.45) * mm, "end": v(5.2, -32.43) * mm});
            skLineSegment(sketch, "E1971", {"start": v(5.2, -32.43) * mm, "end": v(5.2, -32.4) * mm});
            skLineSegment(sketch, "E1972", {"start": v(5.2, -32.4) * mm, "end": v(5.2, -32.38) * mm});
            skLineSegment(sketch, "E1973", {"start": v(5.2, -32.38) * mm, "end": v(5.2, -32.35) * mm});
            skLineSegment(sketch, "E1974", {"start": v(5.2, -32.35) * mm, "end": v(5.2, -32.32) * mm});
            skLineSegment(sketch, "E1975", {"start": v(5.2, -32.32) * mm, "end": v(5.2, -32.3) * mm});
            skLineSegment(sketch, "E1976", {"start": v(5.2, -32.3) * mm, "end": v(5.2, -32.26) * mm});
            skLineSegment(sketch, "E1977", {"start": v(5.2, -32.26) * mm, "end": v(5.21, -32.21) * mm});
            skLineSegment(sketch, "E1978", {"start": v(5.21, -32.21) * mm, "end": v(5.21, -32.17) * mm});
            skLineSegment(sketch, "E1979", {"start": v(5.21, -32.17) * mm, "end": v(5.22, -32.12) * mm});
            skLineSegment(sketch, "E1980", {"start": v(5.22, -32.12) * mm, "end": v(5.22, -32.06) * mm});
            skLineSegment(sketch, "E1981", {"start": v(5.22, -32.06) * mm, "end": v(5.22, -32) * mm});
            skLineSegment(sketch, "E1982", {"start": v(5.22, -32) * mm, "end": v(5.22, -31.95) * mm});
            skLineSegment(sketch, "E1983", {"start": v(5.22, -31.95) * mm, "end": v(5.22, -31.89) * mm});
            skLineSegment(sketch, "E1984", {"start": v(5.22, -31.89) * mm, "end": v(5.22, -31.82) * mm});
            skLineSegment(sketch, "E1985", {"start": v(5.22, -31.82) * mm, "end": v(5.21, -31.75) * mm});
            skLineSegment(sketch, "E1986", {"start": v(5.21, -31.75) * mm, "end": v(5.2, -31.68) * mm});
            skLineSegment(sketch, "E1987", {"start": v(5.2, -31.68) * mm, "end": v(5.2, -31.6) * mm});
            skLineSegment(sketch, "E1988", {"start": v(5.2, -31.6) * mm, "end": v(5.2, -31.52) * mm});
            skLineSegment(sketch, "E1989", {"start": v(5.2, -31.52) * mm, "end": v(5.19, -31.44) * mm});
            skLineSegment(sketch, "E1990", {"start": v(5.19, -31.44) * mm, "end": v(5.18, -31.36) * mm});
            skLineSegment(sketch, "E1991", {"start": v(5.18, -31.36) * mm, "end": v(5.16, -31.27) * mm});
            skLineSegment(sketch, "E1992", {"start": v(5.16, -31.27) * mm, "end": v(5.15, -31.18) * mm});
            skLineSegment(sketch, "E1993", {"start": v(5.15, -31.18) * mm, "end": v(5.13, -31.08) * mm});
            skLineSegment(sketch, "E1994", {"start": v(5.13, -31.08) * mm, "end": v(5.12, -31.02) * mm});
            skLineSegment(sketch, "E1995", {"start": v(5.12, -31.02) * mm, "end": v(4.85, -30.93) * mm});
            skLineSegment(sketch, "E1996", {"start": v(4.85, -30.93) * mm, "end": v(4.57, -30.89) * mm});
            skLineSegment(sketch, "E1997", {"start": v(4.57, -30.89) * mm, "end": v(4.53, -30.94) * mm});
            skLineSegment(sketch, "E1998", {"start": v(4.53, -30.94) * mm, "end": v(4.47, -31.01) * mm});
            skLineSegment(sketch, "E1999", {"start": v(4.47, -31.01) * mm, "end": v(4.42, -31.09) * mm});
            skLineSegment(sketch, "E2000", {"start": v(4.42, -31.09) * mm, "end": v(4.37, -31.16) * mm});
            skLineSegment(sketch, "E2001", {"start": v(4.37, -31.16) * mm, "end": v(4.32, -31.23) * mm});
            skLineSegment(sketch, "E2002", {"start": v(4.32, -31.23) * mm, "end": v(4.27, -31.3) * mm});
            skLineSegment(sketch, "E2003", {"start": v(4.27, -31.3) * mm, "end": v(4.23, -31.37) * mm});
            skLineSegment(sketch, "E2004", {"start": v(4.23, -31.37) * mm, "end": v(4.2, -31.43) * mm});
            skLineSegment(sketch, "E2005", {"start": v(4.2, -31.43) * mm, "end": v(4.15, -31.5) * mm});
            skLineSegment(sketch, "E2006", {"start": v(4.15, -31.5) * mm, "end": v(4.12, -31.56) * mm});
            skLineSegment(sketch, "E2007", {"start": v(4.12, -31.56) * mm, "end": v(4.09, -31.61) * mm});
            skLineSegment(sketch, "E2008", {"start": v(4.09, -31.61) * mm, "end": v(4.06, -31.67) * mm});
            skLineSegment(sketch, "E2009", {"start": v(4.06, -31.67) * mm, "end": v(4.03, -31.72) * mm});
            skLineSegment(sketch, "E2010", {"start": v(4.03, -31.72) * mm, "end": v(4, -31.77) * mm});
            skLineSegment(sketch, "E2011", {"start": v(4, -31.77) * mm, "end": v(3.99, -31.82) * mm});
            skLineSegment(sketch, "E2012", {"start": v(3.99, -31.82) * mm, "end": v(3.96, -31.87) * mm});
            skLineSegment(sketch, "E2013", {"start": v(3.96, -31.87) * mm, "end": v(3.95, -31.9) * mm});
            skLineSegment(sketch, "E2014", {"start": v(3.95, -31.9) * mm, "end": v(3.93, -31.95) * mm});
            skLineSegment(sketch, "E2015", {"start": v(3.93, -31.95) * mm, "end": v(3.91, -31.99) * mm});
            skLineSegment(sketch, "E2016", {"start": v(3.91, -31.99) * mm, "end": v(3.9, -32) * mm});
            skLineSegment(sketch, "E2017", {"start": v(3.9, -32) * mm, "end": v(3.9, -32.04) * mm});
            skLineSegment(sketch, "E2018", {"start": v(3.9, -32.04) * mm, "end": v(3.88, -32.06) * mm});
            skLineSegment(sketch, "E2019", {"start": v(3.88, -32.06) * mm, "end": v(3.87, -32.08) * mm});
            skLineSegment(sketch, "E2020", {"start": v(3.87, -32.08) * mm, "end": v(3.86, -32.1) * mm});
            skLineSegment(sketch, "E2021", {"start": v(3.86, -32.1) * mm, "end": v(3.84, -32.12) * mm});
            skLineSegment(sketch, "E2022", {"start": v(3.84, -32.12) * mm, "end": v(3.83, -32.13) * mm});
            skLineSegment(sketch, "E2023", {"start": v(3.83, -32.13) * mm, "end": v(3.82, -32.14) * mm});
            skLineSegment(sketch, "E2024", {"start": v(3.82, -32.14) * mm, "end": v(3.8, -32.15) * mm});
            skLineSegment(sketch, "E2025", {"start": v(3.8, -32.15) * mm, "end": v(3.8, -32.15) * mm});
            skLineSegment(sketch, "E2026", {"start": v(3.8, -32.15) * mm, "end": v(3.6, -32.11) * mm});
            skLineSegment(sketch, "E2027", {"start": v(3.6, -32.11) * mm, "end": v(3.4, -32.08) * mm});
            skLineSegment(sketch, "E2028", {"start": v(3.4, -32.08) * mm, "end": v(3.2, -32.05) * mm});
            skLineSegment(sketch, "E2029", {"start": v(3.2, -32.05) * mm, "end": v(3.2, -32.05) * mm});
            skLineSegment(sketch, "E2030", {"start": v(3.2, -32.05) * mm, "end": v(3.18, -32.04) * mm});
            skLineSegment(sketch, "E2031", {"start": v(3.18, -32.04) * mm, "end": v(3.17, -32.03) * mm});
            skLineSegment(sketch, "E2032", {"start": v(3.17, -32.03) * mm, "end": v(3.17, -32.01) * mm});
            skLineSegment(sketch, "E2033", {"start": v(3.17, -32.01) * mm, "end": v(3.16, -32) * mm});
            skLineSegment(sketch, "E2034", {"start": v(3.16, -32) * mm, "end": v(3.15, -31.97) * mm});
            skLineSegment(sketch, "E2035", {"start": v(3.15, -31.97) * mm, "end": v(3.15, -31.95) * mm});
            skLineSegment(sketch, "E2036", {"start": v(3.15, -31.95) * mm, "end": v(3.14, -31.92) * mm});
            skLineSegment(sketch, "E2037", {"start": v(3.14, -31.92) * mm, "end": v(3.14, -31.88) * mm});
            skLineSegment(sketch, "E2038", {"start": v(3.14, -31.88) * mm, "end": v(3.14, -31.86) * mm});
            skLineSegment(sketch, "E2039", {"start": v(3.14, -31.86) * mm, "end": v(3.14, -31.82) * mm});
            skLineSegment(sketch, "E2040", {"start": v(3.14, -31.82) * mm, "end": v(3.13, -31.78) * mm});
            skLineSegment(sketch, "E2041", {"start": v(3.13, -31.78) * mm, "end": v(3.13, -31.73) * mm});
            skLineSegment(sketch, "E2042", {"start": v(3.13, -31.73) * mm, "end": v(3.12, -31.68) * mm});
            skLineSegment(sketch, "E2043", {"start": v(3.12, -31.68) * mm, "end": v(3.12, -31.63) * mm});
            skLineSegment(sketch, "E2044", {"start": v(3.12, -31.63) * mm, "end": v(3.1, -31.58) * mm});
            skLineSegment(sketch, "E2045", {"start": v(3.1, -31.58) * mm, "end": v(3.1, -31.52) * mm});
            skLineSegment(sketch, "E2046", {"start": v(3.1, -31.52) * mm, "end": v(3.09, -31.46) * mm});
            skLineSegment(sketch, "E2047", {"start": v(3.09, -31.46) * mm, "end": v(3.08, -31.4) * mm});
            skLineSegment(sketch, "E2048", {"start": v(3.08, -31.4) * mm, "end": v(3.06, -31.32) * mm});
            skLineSegment(sketch, "E2049", {"start": v(3.06, -31.32) * mm, "end": v(3.05, -31.25) * mm});
            skLineSegment(sketch, "E2050", {"start": v(3.05, -31.25) * mm, "end": v(3.03, -31.18) * mm});
            skLineSegment(sketch, "E2051", {"start": v(3.03, -31.18) * mm, "end": v(3, -31.1) * mm});
            skLineSegment(sketch, "E2052", {"start": v(3, -31.1) * mm, "end": v(2.99, -31.02) * mm});
            skLineSegment(sketch, "E2053", {"start": v(2.99, -31.02) * mm, "end": v(2.96, -30.94) * mm});
            skLineSegment(sketch, "E2054", {"start": v(2.96, -30.94) * mm, "end": v(2.94, -30.86) * mm});
            skLineSegment(sketch, "E2055", {"start": v(2.94, -30.86) * mm, "end": v(2.9, -30.77) * mm});
            skLineSegment(sketch, "E2056", {"start": v(2.9, -30.77) * mm, "end": v(2.88, -30.68) * mm});
            skLineSegment(sketch, "E2057", {"start": v(2.88, -30.68) * mm, "end": v(2.86, -30.62) * mm});
            skLineSegment(sketch, "E2058", {"start": v(2.86, -30.62) * mm, "end": v(2.58, -30.57) * mm});
            skLineSegment(sketch, "E2059", {"start": v(2.58, -30.57) * mm, "end": v(2.3, -30.57) * mm});
            skLineSegment(sketch, "E2060", {"start": v(2.3, -30.57) * mm, "end": v(2.26, -30.63) * mm});
            skLineSegment(sketch, "E2061", {"start": v(2.26, -30.63) * mm, "end": v(2.22, -30.71) * mm});
            skLineSegment(sketch, "E2062", {"start": v(2.22, -30.71) * mm, "end": v(2.17, -30.8) * mm});
            skLineSegment(sketch, "E2063", {"start": v(2.17, -30.8) * mm, "end": v(2.13, -30.87) * mm});
            skLineSegment(sketch, "E2064", {"start": v(2.13, -30.87) * mm, "end": v(2.1, -30.95) * mm});
            skLineSegment(sketch, "E2065", {"start": v(2.1, -30.95) * mm, "end": v(2.06, -31.03) * mm});
            skLineSegment(sketch, "E2066", {"start": v(2.06, -31.03) * mm, "end": v(2.03, -31.1) * mm});
            skLineSegment(sketch, "E2067", {"start": v(2.03, -31.1) * mm, "end": v(2, -31.17) * mm});
            skLineSegment(sketch, "E2068", {"start": v(2, -31.17) * mm, "end": v(1.98, -31.24) * mm});
            skLineSegment(sketch, "E2069", {"start": v(1.98, -31.24) * mm, "end": v(1.95, -31.3) * mm});
            skLineSegment(sketch, "E2070", {"start": v(1.95, -31.3) * mm, "end": v(1.93, -31.36) * mm});
            skLineSegment(sketch, "E2071", {"start": v(1.93, -31.36) * mm, "end": v(1.91, -31.42) * mm});
            skLineSegment(sketch, "E2072", {"start": v(1.91, -31.42) * mm, "end": v(1.9, -31.48) * mm});
            skLineSegment(sketch, "E2073", {"start": v(1.9, -31.48) * mm, "end": v(1.88, -31.53) * mm});
            skLineSegment(sketch, "E2074", {"start": v(1.88, -31.53) * mm, "end": v(1.86, -31.59) * mm});
            skLineSegment(sketch, "E2075", {"start": v(1.86, -31.59) * mm, "end": v(1.85, -31.63) * mm});
            skLineSegment(sketch, "E2076", {"start": v(1.85, -31.63) * mm, "end": v(1.84, -31.68) * mm});
            skLineSegment(sketch, "E2077", {"start": v(1.84, -31.68) * mm, "end": v(1.83, -31.72) * mm});
            skLineSegment(sketch, "E2078", {"start": v(1.83, -31.72) * mm, "end": v(1.82, -31.76) * mm});
            skLineSegment(sketch, "E2079", {"start": v(1.82, -31.76) * mm, "end": v(1.81, -31.78) * mm});
            skLineSegment(sketch, "E2080", {"start": v(1.81, -31.78) * mm, "end": v(1.8, -31.81) * mm});
            skLineSegment(sketch, "E2081", {"start": v(1.8, -31.81) * mm, "end": v(1.8, -31.84) * mm});
            skLineSegment(sketch, "E2082", {"start": v(1.8, -31.84) * mm, "end": v(1.79, -31.86) * mm});
            skLineSegment(sketch, "E2083", {"start": v(1.79, -31.86) * mm, "end": v(1.78, -31.88) * mm});
            skLineSegment(sketch, "E2084", {"start": v(1.78, -31.88) * mm, "end": v(1.77, -31.9) * mm});
            skLineSegment(sketch, "E2085", {"start": v(1.77, -31.9) * mm, "end": v(1.76, -31.92) * mm});
            skLineSegment(sketch, "E2086", {"start": v(1.76, -31.92) * mm, "end": v(1.75, -31.93) * mm});
            skLineSegment(sketch, "E2087", {"start": v(1.75, -31.93) * mm, "end": v(1.74, -31.93) * mm});
            skLineSegment(sketch, "E2088", {"start": v(1.74, -31.93) * mm, "end": v(1.73, -31.94) * mm});
            skLineSegment(sketch, "E2089", {"start": v(1.73, -31.94) * mm, "end": v(1.53, -31.93) * mm});
            skLineSegment(sketch, "E2090", {"start": v(1.53, -31.93) * mm, "end": v(1.32, -31.93) * mm});
            skLineSegment(sketch, "E2091", {"start": v(1.32, -31.93) * mm, "end": v(1.12, -31.94) * mm});
            skLineSegment(sketch, "E2092", {"start": v(1.12, -31.94) * mm, "end": v(1.11, -31.93) * mm});
            skLineSegment(sketch, "E2093", {"start": v(1.11, -31.93) * mm, "end": v(1.1, -31.93) * mm});
            skLineSegment(sketch, "E2094", {"start": v(1.1, -31.93) * mm, "end": v(1.1, -31.92) * mm});
            skLineSegment(sketch, "E2095", {"start": v(1.1, -31.92) * mm, "end": v(1.08, -31.9) * mm});
            skLineSegment(sketch, "E2096", {"start": v(1.08, -31.9) * mm, "end": v(1.07, -31.88) * mm});
            skLineSegment(sketch, "E2097", {"start": v(1.07, -31.88) * mm, "end": v(1.06, -31.86) * mm});
            skLineSegment(sketch, "E2098", {"start": v(1.06, -31.86) * mm, "end": v(1.05, -31.84) * mm});
            skLineSegment(sketch, "E2099", {"start": v(1.05, -31.84) * mm, "end": v(1.04, -31.81) * mm});
            skLineSegment(sketch, "E2100", {"start": v(1.04, -31.81) * mm, "end": v(1.04, -31.78) * mm});
            skLineSegment(sketch, "E2101", {"start": v(1.04, -31.78) * mm, "end": v(1.03, -31.76) * mm});
            skLineSegment(sketch, "E2102", {"start": v(1.03, -31.76) * mm, "end": v(1.02, -31.72) * mm});
            skLineSegment(sketch, "E2103", {"start": v(1.02, -31.72) * mm, "end": v(1.01, -31.68) * mm});
            skLineSegment(sketch, "E2104", {"start": v(1.01, -31.68) * mm, "end": v(1, -31.63) * mm});
            skLineSegment(sketch, "E2105", {"start": v(1, -31.63) * mm, "end": v(0.99, -31.59) * mm});
            skLineSegment(sketch, "E2106", {"start": v(0.99, -31.59) * mm, "end": v(0.97, -31.53) * mm});
            skLineSegment(sketch, "E2107", {"start": v(0.97, -31.53) * mm, "end": v(0.96, -31.48) * mm});
            skLineSegment(sketch, "E2108", {"start": v(0.96, -31.48) * mm, "end": v(0.94, -31.42) * mm});
            skLineSegment(sketch, "E2109", {"start": v(0.94, -31.42) * mm, "end": v(0.92, -31.36) * mm});
            skLineSegment(sketch, "E2110", {"start": v(0.92, -31.36) * mm, "end": v(0.9, -31.3) * mm});
            skLineSegment(sketch, "E2111", {"start": v(0.9, -31.3) * mm, "end": v(0.87, -31.24) * mm});
            skLineSegment(sketch, "E2112", {"start": v(0.87, -31.24) * mm, "end": v(0.85, -31.17) * mm});
            skLineSegment(sketch, "E2113", {"start": v(0.85, -31.17) * mm, "end": v(0.82, -31.1) * mm});
            skLineSegment(sketch, "E2114", {"start": v(0.82, -31.1) * mm, "end": v(0.78, -31.03) * mm});
            skLineSegment(sketch, "E2115", {"start": v(0.78, -31.03) * mm, "end": v(0.75, -30.95) * mm});
            skLineSegment(sketch, "E2116", {"start": v(0.75, -30.95) * mm, "end": v(0.71, -30.87) * mm});
            skLineSegment(sketch, "E2117", {"start": v(0.71, -30.87) * mm, "end": v(0.68, -30.8) * mm});
            skLineSegment(sketch, "E2118", {"start": v(0.68, -30.8) * mm, "end": v(0.63, -30.71) * mm});
            skLineSegment(sketch, "E2119", {"start": v(0.63, -30.71) * mm, "end": v(0.59, -30.63) * mm});
            skLineSegment(sketch, "E2120", {"start": v(0.59, -30.63) * mm, "end": v(0.56, -30.57) * mm});
            skLineSegment(sketch, "E2121", {"start": v(0.56, -30.57) * mm, "end": v(0.27, -30.57) * mm});
            skLineSegment(sketch, "E2122", {"start": v(0.27, -30.57) * mm, "end": v(0, -30.62) * mm});
            skLineSegment(sketch, "E2123", {"start": v(0, -30.62) * mm, "end": v(-0.03, -30.68) * mm});
            skLineSegment(sketch, "E2124", {"start": v(-0.03, -30.68) * mm, "end": v(-0.06, -30.77) * mm});
            skLineSegment(sketch, "E2125", {"start": v(-0.06, -30.77) * mm, "end": v(-0.09, -30.86) * mm});
            skLineSegment(sketch, "E2126", {"start": v(-0.09, -30.86) * mm, "end": v(-0.11, -30.94) * mm});
            skLineSegment(sketch, "E2127", {"start": v(-0.11, -30.94) * mm, "end": v(-0.14, -31.02) * mm});
            skLineSegment(sketch, "E2128", {"start": v(-0.14, -31.02) * mm, "end": v(-0.16, -31.1) * mm});
            skLineSegment(sketch, "E2129", {"start": v(-0.16, -31.1) * mm, "end": v(-0.18, -31.18) * mm});
            skLineSegment(sketch, "E2130", {"start": v(-0.18, -31.18) * mm, "end": v(-0.2, -31.25) * mm});
            skLineSegment(sketch, "E2131", {"start": v(-0.2, -31.25) * mm, "end": v(-0.21, -31.32) * mm});
            skLineSegment(sketch, "E2132", {"start": v(-0.21, -31.32) * mm, "end": v(-0.23, -31.4) * mm});
            skLineSegment(sketch, "E2133", {"start": v(-0.23, -31.4) * mm, "end": v(-0.24, -31.46) * mm});
            skLineSegment(sketch, "E2134", {"start": v(-0.24, -31.46) * mm, "end": v(-0.25, -31.52) * mm});
            skLineSegment(sketch, "E2135", {"start": v(-0.25, -31.52) * mm, "end": v(-0.26, -31.58) * mm});
            skLineSegment(sketch, "E2136", {"start": v(-0.26, -31.58) * mm, "end": v(-0.27, -31.63) * mm});
            skLineSegment(sketch, "E2137", {"start": v(-0.27, -31.63) * mm, "end": v(-0.27, -31.68) * mm});
            skLineSegment(sketch, "E2138", {"start": v(-0.27, -31.68) * mm, "end": v(-0.28, -31.73) * mm});
            skLineSegment(sketch, "E2139", {"start": v(-0.28, -31.73) * mm, "end": v(-0.28, -31.78) * mm});
            skLineSegment(sketch, "E2140", {"start": v(-0.28, -31.78) * mm, "end": v(-0.29, -31.82) * mm});
            skLineSegment(sketch, "E2141", {"start": v(-0.29, -31.82) * mm, "end": v(-0.3, -31.86) * mm});
            skLineSegment(sketch, "E2142", {"start": v(-0.3, -31.86) * mm, "end": v(-0.3, -31.88) * mm});
            skLineSegment(sketch, "E2143", {"start": v(-0.3, -31.88) * mm, "end": v(-0.3, -31.92) * mm});
            skLineSegment(sketch, "E2144", {"start": v(-0.3, -31.92) * mm, "end": v(-0.3, -31.95) * mm});
            skLineSegment(sketch, "E2145", {"start": v(-0.3, -31.95) * mm, "end": v(-0.3, -31.97) * mm});
            skLineSegment(sketch, "E2146", {"start": v(-0.3, -31.97) * mm, "end": v(-0.3, -32) * mm});
            skLineSegment(sketch, "E2147", {"start": v(-0.3, -32) * mm, "end": v(-0.32, -32.01) * mm});
            skLineSegment(sketch, "E2148", {"start": v(-0.32, -32.01) * mm, "end": v(-0.32, -32.03) * mm});
            skLineSegment(sketch, "E2149", {"start": v(-0.32, -32.03) * mm, "end": v(-0.33, -32.04) * mm});
            skLineSegment(sketch, "E2150", {"start": v(-0.33, -32.04) * mm, "end": v(-0.34, -32.05) * mm});
            skLineSegment(sketch, "E2151", {"start": v(-0.34, -32.05) * mm, "end": v(-0.35, -32.05) * mm});
            skLineSegment(sketch, "E2152", {"start": v(-0.35, -32.05) * mm, "end": v(-0.55, -32.08) * mm});
            skLineSegment(sketch, "E2153", {"start": v(-0.55, -32.08) * mm, "end": v(-0.75, -32.11) * mm});
            skLineSegment(sketch, "E2154", {"start": v(-0.75, -32.11) * mm, "end": v(-0.95, -32.15) * mm});
            skLineSegment(sketch, "E2155", {"start": v(-0.95, -32.15) * mm, "end": v(-0.96, -32.15) * mm});
            skLineSegment(sketch, "E2156", {"start": v(-0.96, -32.15) * mm, "end": v(-0.97, -32.14) * mm});
            skLineSegment(sketch, "E2157", {"start": v(-0.97, -32.14) * mm, "end": v(-0.98, -32.13) * mm});
            skLineSegment(sketch, "E2158", {"start": v(-0.98, -32.13) * mm, "end": v(-1, -32.12) * mm});
            skLineSegment(sketch, "E2159", {"start": v(-1, -32.12) * mm, "end": v(-1, -32.1) * mm});
            skLineSegment(sketch, "E2160", {"start": v(-1, -32.1) * mm, "end": v(-1.02, -32.08) * mm});
            skLineSegment(sketch, "E2161", {"start": v(-1.02, -32.08) * mm, "end": v(-1.03, -32.06) * mm});
            skLineSegment(sketch, "E2162", {"start": v(-1.03, -32.06) * mm, "end": v(-1.05, -32.04) * mm});
            skLineSegment(sketch, "E2163", {"start": v(-1.05, -32.04) * mm, "end": v(-1.06, -32) * mm});
            skLineSegment(sketch, "E2164", {"start": v(-1.06, -32) * mm, "end": v(-1.07, -31.99) * mm});
            skLineSegment(sketch, "E2165", {"start": v(-1.07, -31.99) * mm, "end": v(-1.08, -31.95) * mm});
            skLineSegment(sketch, "E2166", {"start": v(-1.08, -31.95) * mm, "end": v(-1.1, -31.9) * mm});
            skLineSegment(sketch, "E2167", {"start": v(-1.1, -31.9) * mm, "end": v(-1.12, -31.87) * mm});
            skLineSegment(sketch, "E2168", {"start": v(-1.12, -31.87) * mm, "end": v(-1.14, -31.82) * mm});
            skLineSegment(sketch, "E2169", {"start": v(-1.14, -31.82) * mm, "end": v(-1.16, -31.77) * mm});
            skLineSegment(sketch, "E2170", {"start": v(-1.16, -31.77) * mm, "end": v(-1.18, -31.72) * mm});
            skLineSegment(sketch, "E2171", {"start": v(-1.18, -31.72) * mm, "end": v(-1.21, -31.67) * mm});
            skLineSegment(sketch, "E2172", {"start": v(-1.21, -31.67) * mm, "end": v(-1.24, -31.61) * mm});
            skLineSegment(sketch, "E2173", {"start": v(-1.24, -31.61) * mm, "end": v(-1.27, -31.56) * mm});
            skLineSegment(sketch, "E2174", {"start": v(-1.27, -31.56) * mm, "end": v(-1.3, -31.5) * mm});
            skLineSegment(sketch, "E2175", {"start": v(-1.3, -31.5) * mm, "end": v(-1.34, -31.43) * mm});
            skLineSegment(sketch, "E2176", {"start": v(-1.34, -31.43) * mm, "end": v(-1.38, -31.37) * mm});
            skLineSegment(sketch, "E2177", {"start": v(-1.38, -31.37) * mm, "end": v(-1.42, -31.3) * mm});
            skLineSegment(sketch, "E2178", {"start": v(-1.42, -31.3) * mm, "end": v(-1.47, -31.23) * mm});
            skLineSegment(sketch, "E2179", {"start": v(-1.47, -31.23) * mm, "end": v(-1.52, -31.16) * mm});
            skLineSegment(sketch, "E2180", {"start": v(-1.52, -31.16) * mm, "end": v(-1.57, -31.09) * mm});
            skLineSegment(sketch, "E2181", {"start": v(-1.57, -31.09) * mm, "end": v(-1.62, -31.01) * mm});
            skLineSegment(sketch, "E2182", {"start": v(-1.62, -31.01) * mm, "end": v(-1.68, -30.94) * mm});
            skLineSegment(sketch, "E2183", {"start": v(-1.68, -30.94) * mm, "end": v(-1.72, -30.89) * mm});
            skLineSegment(sketch, "E2184", {"start": v(-1.72, -30.89) * mm, "end": v(-2, -30.93) * mm});
            skLineSegment(sketch, "E2185", {"start": v(-2, -30.93) * mm, "end": v(-2.27, -31.02) * mm});
            skLineSegment(sketch, "E2186", {"start": v(-2.27, -31.02) * mm, "end": v(-2.28, -31.08) * mm});
            skLineSegment(sketch, "E2187", {"start": v(-2.28, -31.08) * mm, "end": v(-2.3, -31.18) * mm});
            skLineSegment(sketch, "E2188", {"start": v(-2.3, -31.18) * mm, "end": v(-2.31, -31.27) * mm});
            skLineSegment(sketch, "E2189", {"start": v(-2.31, -31.27) * mm, "end": v(-2.33, -31.36) * mm});
            skLineSegment(sketch, "E2190", {"start": v(-2.33, -31.36) * mm, "end": v(-2.34, -31.44) * mm});
            skLineSegment(sketch, "E2191", {"start": v(-2.34, -31.44) * mm, "end": v(-2.35, -31.52) * mm});
            skLineSegment(sketch, "E2192", {"start": v(-2.35, -31.52) * mm, "end": v(-2.35, -31.6) * mm});
            skLineSegment(sketch, "E2193", {"start": v(-2.35, -31.6) * mm, "end": v(-2.36, -31.68) * mm});
            skLineSegment(sketch, "E2194", {"start": v(-2.36, -31.68) * mm, "end": v(-2.36, -31.75) * mm});
            skLineSegment(sketch, "E2195", {"start": v(-2.36, -31.75) * mm, "end": v(-2.37, -31.82) * mm});
            skLineSegment(sketch, "E2196", {"start": v(-2.37, -31.82) * mm, "end": v(-2.37, -31.89) * mm});
            skLineSegment(sketch, "E2197", {"start": v(-2.37, -31.89) * mm, "end": v(-2.37, -31.95) * mm});
            skLineSegment(sketch, "E2198", {"start": v(-2.37, -31.95) * mm, "end": v(-2.37, -32) * mm});
            skLineSegment(sketch, "E2199", {"start": v(-2.37, -32) * mm, "end": v(-2.37, -32.06) * mm});
            skLineSegment(sketch, "E2200", {"start": v(-2.37, -32.06) * mm, "end": v(-2.37, -32.12) * mm});
            skLineSegment(sketch, "E2201", {"start": v(-2.37, -32.12) * mm, "end": v(-2.37, -32.17) * mm});
            skLineSegment(sketch, "E2202", {"start": v(-2.37, -32.17) * mm, "end": v(-2.36, -32.21) * mm});
            skLineSegment(sketch, "E2203", {"start": v(-2.36, -32.21) * mm, "end": v(-2.36, -32.26) * mm});
            skLineSegment(sketch, "E2204", {"start": v(-2.36, -32.26) * mm, "end": v(-2.36, -32.3) * mm});
            skLineSegment(sketch, "E2205", {"start": v(-2.36, -32.3) * mm, "end": v(-2.35, -32.32) * mm});
            skLineSegment(sketch, "E2206", {"start": v(-2.35, -32.32) * mm, "end": v(-2.35, -32.35) * mm});
            skLineSegment(sketch, "E2207", {"start": v(-2.35, -32.35) * mm, "end": v(-2.35, -32.38) * mm});
            skLineSegment(sketch, "E2208", {"start": v(-2.35, -32.38) * mm, "end": v(-2.35, -32.4) * mm});
            skLineSegment(sketch, "E2209", {"start": v(-2.35, -32.4) * mm, "end": v(-2.35, -32.43) * mm});
            skLineSegment(sketch, "E2210", {"start": v(-2.35, -32.43) * mm, "end": v(-2.36, -32.45) * mm});
            skLineSegment(sketch, "E2211", {"start": v(-2.36, -32.45) * mm, "end": v(-2.36, -32.46) * mm});
            skLineSegment(sketch, "E2212", {"start": v(-2.36, -32.46) * mm, "end": v(-2.37, -32.48) * mm});
            skLineSegment(sketch, "E2213", {"start": v(-2.37, -32.48) * mm, "end": v(-2.38, -32.49) * mm});
            skLineSegment(sketch, "E2214", {"start": v(-2.38, -32.49) * mm, "end": v(-2.39, -32.5) * mm});
            skLineSegment(sketch, "E2215", {"start": v(-2.39, -32.5) * mm, "end": v(-2.58, -32.55) * mm});
            skLineSegment(sketch, "E2216", {"start": v(-2.58, -32.55) * mm, "end": v(-2.77, -32.61) * mm});
            skLineSegment(sketch, "E2217", {"start": v(-2.77, -32.61) * mm, "end": v(-2.96, -32.68) * mm});
            skLineSegment(sketch, "E2218", {"start": v(-2.96, -32.68) * mm, "end": v(-2.97, -32.68) * mm});
            skLineSegment(sketch, "E2219", {"start": v(-2.97, -32.68) * mm, "end": v(-2.98, -32.68) * mm});
            skLineSegment(sketch, "E2220", {"start": v(-2.98, -32.68) * mm, "end": v(-3, -32.67) * mm});
            skLineSegment(sketch, "E2221", {"start": v(-3, -32.67) * mm, "end": v(-3.01, -32.66) * mm});
            skLineSegment(sketch, "E2222", {"start": v(-3.01, -32.66) * mm, "end": v(-3.03, -32.65) * mm});
            skLineSegment(sketch, "E2223", {"start": v(-3.03, -32.65) * mm, "end": v(-3.04, -32.63) * mm});
            skLineSegment(sketch, "E2224", {"start": v(-3.04, -32.63) * mm, "end": v(-3.06, -32.6) * mm});
            skLineSegment(sketch, "E2225", {"start": v(-3.06, -32.6) * mm, "end": v(-3.08, -32.58) * mm});
            skLineSegment(sketch, "E2226", {"start": v(-3.08, -32.58) * mm, "end": v(-3.1, -32.56) * mm});
            skLineSegment(sketch, "E2227", {"start": v(-3.1, -32.56) * mm, "end": v(-3.1, -32.54) * mm});
            skLineSegment(sketch, "E2228", {"start": v(-3.1, -32.54) * mm, "end": v(-3.12, -32.5) * mm});
            skLineSegment(sketch, "E2229", {"start": v(-3.12, -32.5) * mm, "end": v(-3.14, -32.47) * mm});
            skLineSegment(sketch, "E2230", {"start": v(-3.14, -32.47) * mm, "end": v(-3.17, -32.43) * mm});
            skLineSegment(sketch, "E2231", {"start": v(-3.17, -32.43) * mm, "end": v(-3.2, -32.39) * mm});
            skLineSegment(sketch, "E2232", {"start": v(-3.2, -32.39) * mm, "end": v(-3.23, -32.34) * mm});
            skLineSegment(sketch, "E2233", {"start": v(-3.23, -32.34) * mm, "end": v(-3.26, -32.3) * mm});
            skLineSegment(sketch, "E2234", {"start": v(-3.26, -32.3) * mm, "end": v(-3.3, -32.25) * mm});
            skLineSegment(sketch, "E2235", {"start": v(-3.3, -32.25) * mm, "end": v(-3.33, -32.2) * mm});
            skLineSegment(sketch, "E2236", {"start": v(-3.33, -32.2) * mm, "end": v(-3.37, -32.15) * mm});
            skLineSegment(sketch, "E2237", {"start": v(-3.37, -32.15) * mm, "end": v(-3.42, -32.1) * mm});
            skLineSegment(sketch, "E2238", {"start": v(-3.42, -32.1) * mm, "end": v(-3.46, -32.04) * mm});
            skLineSegment(sketch, "E2239", {"start": v(-3.46, -32.04) * mm, "end": v(-3.51, -31.98) * mm});
            skLineSegment(sketch, "E2240", {"start": v(-3.51, -31.98) * mm, "end": v(-3.56, -31.92) * mm});
            skLineSegment(sketch, "E2241", {"start": v(-3.56, -31.92) * mm, "end": v(-3.62, -31.86) * mm});
            skLineSegment(sketch, "E2242", {"start": v(-3.62, -31.86) * mm, "end": v(-3.68, -31.8) * mm});
            skLineSegment(sketch, "E2243", {"start": v(-3.68, -31.8) * mm, "end": v(-3.74, -31.73) * mm});
            skLineSegment(sketch, "E2244", {"start": v(-3.74, -31.73) * mm, "end": v(-3.8, -31.67) * mm});
            skLineSegment(sketch, "E2245", {"start": v(-3.8, -31.67) * mm, "end": v(-3.87, -31.6) * mm});
            skLineSegment(sketch, "E2246", {"start": v(-3.87, -31.6) * mm, "end": v(-3.92, -31.56) * mm});
            skLineSegment(sketch, "E2247", {"start": v(-3.92, -31.56) * mm, "end": v(-4.2, -31.64) * mm});
            skLineSegment(sketch, "E2248", {"start": v(-4.2, -31.64) * mm, "end": v(-4.44, -31.77) * mm});
            skLineSegment(sketch, "E2249", {"start": v(-4.44, -31.77) * mm, "end": v(-4.45, -31.84) * mm});
            skLineSegment(sketch, "E2250", {"start": v(-4.45, -31.84) * mm, "end": v(-4.45, -31.93) * mm});
            skLineSegment(sketch, "E2251", {"start": v(-4.45, -31.93) * mm, "end": v(-4.45, -32.02) * mm});
            skLineSegment(sketch, "E2252", {"start": v(-4.45, -32.02) * mm, "end": v(-4.45, -32.11) * mm});
            skLineSegment(sketch, "E2253", {"start": v(-4.45, -32.11) * mm, "end": v(-4.44, -32.2) * mm});
            skLineSegment(sketch, "E2254", {"start": v(-4.44, -32.2) * mm, "end": v(-4.44, -32.28) * mm});
            skLineSegment(sketch, "E2255", {"start": v(-4.44, -32.28) * mm, "end": v(-4.43, -32.36) * mm});
            skLineSegment(sketch, "E2256", {"start": v(-4.43, -32.36) * mm, "end": v(-4.43, -32.44) * mm});
            skLineSegment(sketch, "E2257", {"start": v(-4.43, -32.44) * mm, "end": v(-4.42, -32.5) * mm});
            skLineSegment(sketch, "E2258", {"start": v(-4.42, -32.5) * mm, "end": v(-4.41, -32.58) * mm});
            skLineSegment(sketch, "E2259", {"start": v(-4.41, -32.58) * mm, "end": v(-4.4, -32.64) * mm});
            skLineSegment(sketch, "E2260", {"start": v(-4.4, -32.64) * mm, "end": v(-4.4, -32.7) * mm});
            skLineSegment(sketch, "E2261", {"start": v(-4.4, -32.7) * mm, "end": v(-4.39, -32.76) * mm});
            skLineSegment(sketch, "E2262", {"start": v(-4.39, -32.76) * mm, "end": v(-4.38, -32.82) * mm});
            skLineSegment(sketch, "E2263", {"start": v(-4.38, -32.82) * mm, "end": v(-4.37, -32.87) * mm});
            skLineSegment(sketch, "E2264", {"start": v(-4.37, -32.87) * mm, "end": v(-4.36, -32.92) * mm});
            skLineSegment(sketch, "E2265", {"start": v(-4.36, -32.92) * mm, "end": v(-4.35, -32.97) * mm});
            skLineSegment(sketch, "E2266", {"start": v(-4.35, -32.97) * mm, "end": v(-4.34, -33) * mm});
            skLineSegment(sketch, "E2267", {"start": v(-4.34, -33) * mm, "end": v(-4.33, -33.05) * mm});
            skLineSegment(sketch, "E2268", {"start": v(-4.33, -33.05) * mm, "end": v(-4.32, -33.07) * mm});
            skLineSegment(sketch, "E2269", {"start": v(-4.32, -33.07) * mm, "end": v(-4.31, -33.1) * mm});
            skLineSegment(sketch, "E2270", {"start": v(-4.31, -33.1) * mm, "end": v(-4.3, -33.13) * mm});
            skLineSegment(sketch, "E2271", {"start": v(-4.3, -33.13) * mm, "end": v(-4.3, -33.15) * mm});
            skLineSegment(sketch, "E2272", {"start": v(-4.3, -33.15) * mm, "end": v(-4.3, -33.18) * mm});
            skLineSegment(sketch, "E2273", {"start": v(-4.3, -33.18) * mm, "end": v(-4.3, -33.2) * mm});
            skLineSegment(sketch, "E2274", {"start": v(-4.3, -33.2) * mm, "end": v(-4.3, -33.21) * mm});
            skLineSegment(sketch, "E2275", {"start": v(-4.3, -33.21) * mm, "end": v(-4.31, -33.23) * mm});
            skLineSegment(sketch, "E2276", {"start": v(-4.31, -33.23) * mm, "end": v(-4.32, -33.24) * mm});
            skLineSegment(sketch, "E2277", {"start": v(-4.32, -33.24) * mm, "end": v(-4.33, -33.25) * mm});
            skLineSegment(sketch, "E2278", {"start": v(-4.33, -33.25) * mm, "end": v(-4.5, -33.33) * mm});
            skLineSegment(sketch, "E2279", {"start": v(-4.5, -33.33) * mm, "end": v(-4.7, -33.43) * mm});
            skLineSegment(sketch, "E2280", {"start": v(-4.7, -33.43) * mm, "end": v(-4.86, -33.52) * mm});
            skLineSegment(sketch, "E2281", {"start": v(-4.86, -33.52) * mm, "end": v(-4.88, -33.52) * mm});
            skLineSegment(sketch, "E2282", {"start": v(-4.88, -33.52) * mm, "end": v(-4.89, -33.52) * mm});
            skLineSegment(sketch, "E2283", {"start": v(-4.89, -33.52) * mm, "end": v(-4.9, -33.52) * mm});
            skLineSegment(sketch, "E2284", {"start": v(-4.9, -33.52) * mm, "end": v(-4.92, -33.5) * mm});
            skLineSegment(sketch, "E2285", {"start": v(-4.92, -33.5) * mm, "end": v(-4.94, -33.5) * mm});
            skLineSegment(sketch, "E2286", {"start": v(-4.94, -33.5) * mm, "end": v(-4.95, -33.48) * mm});
            skLineSegment(sketch, "E2287", {"start": v(-4.95, -33.48) * mm, "end": v(-4.97, -33.46) * mm});
            skLineSegment(sketch, "E2288", {"start": v(-4.97, -33.46) * mm, "end": v(-5, -33.44) * mm});
            skLineSegment(sketch, "E2289", {"start": v(-5, -33.44) * mm, "end": v(-5.01, -33.42) * mm});
            skLineSegment(sketch, "E2290", {"start": v(-5.01, -33.42) * mm, "end": v(-5.03, -33.4) * mm});
            skLineSegment(sketch, "E2291", {"start": v(-5.03, -33.4) * mm, "end": v(-5.05, -33.37) * mm});
            skLineSegment(sketch, "E2292", {"start": v(-5.05, -33.37) * mm, "end": v(-5.08, -33.34) * mm});
            skLineSegment(sketch, "E2293", {"start": v(-5.08, -33.34) * mm, "end": v(-5.11, -33.3) * mm});
            skLineSegment(sketch, "E2294", {"start": v(-5.11, -33.3) * mm, "end": v(-5.14, -33.27) * mm});
            skLineSegment(sketch, "E2295", {"start": v(-5.14, -33.27) * mm, "end": v(-5.18, -33.23) * mm});
            skLineSegment(sketch, "E2296", {"start": v(-5.18, -33.23) * mm, "end": v(-5.22, -33.19) * mm});
            skLineSegment(sketch, "E2297", {"start": v(-5.22, -33.19) * mm, "end": v(-5.26, -33.15) * mm});
            skLineSegment(sketch, "E2298", {"start": v(-5.26, -33.15) * mm, "end": v(-5.3, -33.1) * mm});
            skLineSegment(sketch, "E2299", {"start": v(-5.3, -33.1) * mm, "end": v(-5.36, -33.06) * mm});
            skLineSegment(sketch, "E2300", {"start": v(-5.36, -33.06) * mm, "end": v(-5.4, -33.01) * mm});
            skLineSegment(sketch, "E2301", {"start": v(-5.4, -33.01) * mm, "end": v(-5.46, -32.96) * mm});
            skLineSegment(sketch, "E2302", {"start": v(-5.46, -32.96) * mm, "end": v(-5.52, -32.91) * mm});
            skLineSegment(sketch, "E2303", {"start": v(-5.52, -32.91) * mm, "end": v(-5.58, -32.86) * mm});
            skLineSegment(sketch, "E2304", {"start": v(-5.58, -32.86) * mm, "end": v(-5.64, -32.81) * mm});
            skLineSegment(sketch, "E2305", {"start": v(-5.64, -32.81) * mm, "end": v(-5.71, -32.76) * mm});
            skLineSegment(sketch, "E2306", {"start": v(-5.71, -32.76) * mm, "end": v(-5.78, -32.7) * mm});
            skLineSegment(sketch, "E2307", {"start": v(-5.78, -32.7) * mm, "end": v(-5.86, -32.65) * mm});
            skLineSegment(sketch, "E2308", {"start": v(-5.86, -32.65) * mm, "end": v(-5.94, -32.6) * mm});
            skLineSegment(sketch, "E2309", {"start": v(-5.94, -32.6) * mm, "end": v(-5.99, -32.56) * mm});
            skLineSegment(sketch, "E2310", {"start": v(-5.99, -32.56) * mm, "end": v(-6.24, -32.69) * mm});
            skLineSegment(sketch, "E2311", {"start": v(-6.24, -32.69) * mm, "end": v(-6.47, -32.86) * mm});
            skLineSegment(sketch, "E2312", {"start": v(-6.47, -32.86) * mm, "end": v(-6.46, -32.92) * mm});
            skLineSegment(sketch, "E2313", {"start": v(-6.46, -32.92) * mm, "end": v(-6.45, -33.01) * mm});
            skLineSegment(sketch, "E2314", {"start": v(-6.45, -33.01) * mm, "end": v(-6.44, -33.1) * mm});
            skLineSegment(sketch, "E2315", {"start": v(-6.44, -33.1) * mm, "end": v(-6.42, -33.2) * mm});
            skLineSegment(sketch, "E2316", {"start": v(-6.42, -33.2) * mm, "end": v(-6.4, -33.28) * mm});
            skLineSegment(sketch, "E2317", {"start": v(-6.4, -33.28) * mm, "end": v(-6.39, -33.36) * mm});
            skLineSegment(sketch, "E2318", {"start": v(-6.39, -33.36) * mm, "end": v(-6.37, -33.44) * mm});
            skLineSegment(sketch, "E2319", {"start": v(-6.37, -33.44) * mm, "end": v(-6.35, -33.5) * mm});
            skLineSegment(sketch, "E2320", {"start": v(-6.35, -33.5) * mm, "end": v(-6.33, -33.58) * mm});
            skLineSegment(sketch, "E2321", {"start": v(-6.33, -33.58) * mm, "end": v(-6.32, -33.65) * mm});
            skLineSegment(sketch, "E2322", {"start": v(-6.32, -33.65) * mm, "end": v(-6.3, -33.7) * mm});
            skLineSegment(sketch, "E2323", {"start": v(-6.3, -33.7) * mm, "end": v(-6.28, -33.77) * mm});
            skLineSegment(sketch, "E2324", {"start": v(-6.28, -33.77) * mm, "end": v(-6.26, -33.83) * mm});
            skLineSegment(sketch, "E2325", {"start": v(-6.26, -33.83) * mm, "end": v(-6.24, -33.88) * mm});
            skLineSegment(sketch, "E2326", {"start": v(-6.24, -33.88) * mm, "end": v(-6.23, -33.93) * mm});
            skLineSegment(sketch, "E2327", {"start": v(-6.23, -33.93) * mm, "end": v(-6.2, -33.98) * mm});
            skLineSegment(sketch, "E2328", {"start": v(-6.2, -33.98) * mm, "end": v(-6.2, -34.02) * mm});
            skLineSegment(sketch, "E2329", {"start": v(-6.2, -34.02) * mm, "end": v(-6.17, -34.06) * mm});
            skLineSegment(sketch, "E2330", {"start": v(-6.17, -34.06) * mm, "end": v(-6.16, -34.1) * mm});
            skLineSegment(sketch, "E2331", {"start": v(-6.16, -34.1) * mm, "end": v(-6.15, -34.11) * mm});
            skLineSegment(sketch, "E2332", {"start": v(-6.15, -34.11) * mm, "end": v(-6.14, -34.14) * mm});
            skLineSegment(sketch, "E2333", {"start": v(-6.14, -34.14) * mm, "end": v(-6.13, -34.17) * mm});
            skLineSegment(sketch, "E2334", {"start": v(-6.13, -34.17) * mm, "end": v(-6.12, -34.2) * mm});
            skLineSegment(sketch, "E2335", {"start": v(-6.12, -34.2) * mm, "end": v(-6.12, -34.22) * mm});
            skLineSegment(sketch, "E2336", {"start": v(-6.12, -34.22) * mm, "end": v(-6.11, -34.24) * mm});
            skLineSegment(sketch, "E2337", {"start": v(-6.11, -34.24) * mm, "end": v(-6.11, -34.26) * mm});
            skLineSegment(sketch, "E2338", {"start": v(-6.11, -34.26) * mm, "end": v(-6.12, -34.27) * mm});
            skLineSegment(sketch, "E2339", {"start": v(-6.12, -34.27) * mm, "end": v(-6.12, -34.28) * mm});
            skLineSegment(sketch, "E2340", {"start": v(-6.12, -34.28) * mm, "end": v(-6.13, -34.3) * mm});
            skLineSegment(sketch, "E2341", {"start": v(-6.13, -34.3) * mm, "end": v(-6.29, -34.4) * mm});
            skLineSegment(sketch, "E2342", {"start": v(-6.29, -34.4) * mm, "end": v(-6.46, -34.53) * mm});
            skLineSegment(sketch, "E2343", {"start": v(-6.46, -34.53) * mm, "end": v(-6.61, -34.65) * mm});
            skLineSegment(sketch, "E2344", {"start": v(-6.61, -34.65) * mm, "end": v(-6.63, -34.65) * mm});
            skLineSegment(sketch, "E2345", {"start": v(-6.63, -34.65) * mm, "end": v(-6.64, -34.65) * mm});
            skLineSegment(sketch, "E2346", {"start": v(-6.64, -34.65) * mm, "end": v(-6.65, -34.65) * mm});
            skLineSegment(sketch, "E2347", {"start": v(-6.65, -34.65) * mm, "end": v(-6.67, -34.64) * mm});
            skLineSegment(sketch, "E2348", {"start": v(-6.67, -34.64) * mm, "end": v(-6.69, -34.64) * mm});
            skLineSegment(sketch, "E2349", {"start": v(-6.69, -34.64) * mm, "end": v(-6.7, -34.62) * mm});
            skLineSegment(sketch, "E2350", {"start": v(-6.7, -34.62) * mm, "end": v(-6.73, -34.6) * mm});
            skLineSegment(sketch, "E2351", {"start": v(-6.73, -34.6) * mm, "end": v(-6.75, -34.6) * mm});
            skLineSegment(sketch, "E2352", {"start": v(-6.75, -34.6) * mm, "end": v(-6.78, -34.57) * mm});
            skLineSegment(sketch, "E2353", {"start": v(-6.78, -34.57) * mm, "end": v(-6.8, -34.56) * mm});
            skLineSegment(sketch, "E2354", {"start": v(-6.8, -34.56) * mm, "end": v(-6.82, -34.53) * mm});
            skLineSegment(sketch, "E2355", {"start": v(-6.82, -34.53) * mm, "end": v(-6.86, -34.5) * mm});
            skLineSegment(sketch, "E2356", {"start": v(-6.86, -34.5) * mm, "end": v(-6.9, -34.47) * mm});
            skLineSegment(sketch, "E2357", {"start": v(-6.9, -34.47) * mm, "end": v(-6.93, -34.44) * mm});
            skLineSegment(sketch, "E2358", {"start": v(-6.93, -34.44) * mm, "end": v(-6.97, -34.4) * mm});
            skLineSegment(sketch, "E2359", {"start": v(-6.97, -34.4) * mm, "end": v(-7.02, -34.38) * mm});
            skLineSegment(sketch, "E2360", {"start": v(-7.02, -34.38) * mm, "end": v(-7.07, -34.34) * mm});
            skLineSegment(sketch, "E2361", {"start": v(-7.07, -34.34) * mm, "end": v(-7.12, -34.3) * mm});
            skLineSegment(sketch, "E2362", {"start": v(-7.12, -34.3) * mm, "end": v(-7.17, -34.27) * mm});
            skLineSegment(sketch, "E2363", {"start": v(-7.17, -34.27) * mm, "end": v(-7.23, -34.23) * mm});
            skLineSegment(sketch, "E2364", {"start": v(-7.23, -34.23) * mm, "end": v(-7.3, -34.2) * mm});
            skLineSegment(sketch, "E2365", {"start": v(-7.3, -34.2) * mm, "end": v(-7.36, -34.15) * mm});
            skLineSegment(sketch, "E2366", {"start": v(-7.36, -34.15) * mm, "end": v(-7.42, -34.11) * mm});
            skLineSegment(sketch, "E2367", {"start": v(-7.42, -34.11) * mm, "end": v(-7.5, -34.07) * mm});
            skLineSegment(sketch, "E2368", {"start": v(-7.5, -34.07) * mm, "end": v(-7.57, -34.03) * mm});
            skLineSegment(sketch, "E2369", {"start": v(-7.57, -34.03) * mm, "end": v(-7.65, -33.99) * mm});
            skLineSegment(sketch, "E2370", {"start": v(-7.65, -33.99) * mm, "end": v(-7.73, -33.94) * mm});
            skLineSegment(sketch, "E2371", {"start": v(-7.73, -33.94) * mm, "end": v(-7.82, -33.9) * mm});
            skLineSegment(sketch, "E2372", {"start": v(-7.82, -33.9) * mm, "end": v(-7.87, -33.88) * mm});
            skLineSegment(sketch, "E2373", {"start": v(-7.87, -33.88) * mm, "end": v(-8.1, -34.04) * mm});
            skLineSegment(sketch, "E2374", {"start": v(-8.1, -34.04) * mm, "end": v(-8.3, -34.24) * mm});
            skLineSegment(sketch, "E2375", {"start": v(-8.3, -34.24) * mm, "end": v(-8.29, -34.3) * mm});
            skLineSegment(sketch, "E2376", {"start": v(-8.29, -34.3) * mm, "end": v(-8.26, -34.4) * mm});
            skLineSegment(sketch, "E2377", {"start": v(-8.26, -34.4) * mm, "end": v(-8.23, -34.48) * mm});
            skLineSegment(sketch, "E2378", {"start": v(-8.23, -34.48) * mm, "end": v(-8.2, -34.57) * mm});
            skLineSegment(sketch, "E2379", {"start": v(-8.2, -34.57) * mm, "end": v(-8.17, -34.65) * mm});
            skLineSegment(sketch, "E2380", {"start": v(-8.17, -34.65) * mm, "end": v(-8.14, -34.73) * mm});
            skLineSegment(sketch, "E2381", {"start": v(-8.14, -34.73) * mm, "end": v(-8.12, -34.8) * mm});
            skLineSegment(sketch, "E2382", {"start": v(-8.12, -34.8) * mm, "end": v(-8.09, -34.87) * mm});
            skLineSegment(sketch, "E2383", {"start": v(-8.09, -34.87) * mm, "end": v(-8.06, -34.94) * mm});
            skLineSegment(sketch, "E2384", {"start": v(-8.06, -34.94) * mm, "end": v(-8.03, -35) * mm});
            skLineSegment(sketch, "E2385", {"start": v(-8.03, -35) * mm, "end": v(-8, -35.06) * mm});
            skLineSegment(sketch, "E2386", {"start": v(-8, -35.06) * mm, "end": v(-7.97, -35.12) * mm});
            skLineSegment(sketch, "E2387", {"start": v(-7.97, -35.12) * mm, "end": v(-7.95, -35.17) * mm});
            skLineSegment(sketch, "E2388", {"start": v(-7.95, -35.17) * mm, "end": v(-7.92, -35.22) * mm});
            skLineSegment(sketch, "E2389", {"start": v(-7.92, -35.22) * mm, "end": v(-7.9, -35.26) * mm});
            skLineSegment(sketch, "E2390", {"start": v(-7.9, -35.26) * mm, "end": v(-7.87, -35.3) * mm});
            skLineSegment(sketch, "E2391", {"start": v(-7.87, -35.3) * mm, "end": v(-7.85, -35.35) * mm});
            skLineSegment(sketch, "E2392", {"start": v(-7.85, -35.35) * mm, "end": v(-7.82, -35.38) * mm});
            skLineSegment(sketch, "E2393", {"start": v(-7.82, -35.38) * mm, "end": v(-7.8, -35.42) * mm});
            skLineSegment(sketch, "E2394", {"start": v(-7.8, -35.42) * mm, "end": v(-7.8, -35.44) * mm});
            skLineSegment(sketch, "E2395", {"start": v(-7.8, -35.44) * mm, "end": v(-7.77, -35.46) * mm});
            skLineSegment(sketch, "E2396", {"start": v(-7.77, -35.46) * mm, "end": v(-7.76, -35.49) * mm});
            skLineSegment(sketch, "E2397", {"start": v(-7.76, -35.49) * mm, "end": v(-7.75, -35.51) * mm});
            skLineSegment(sketch, "E2398", {"start": v(-7.75, -35.51) * mm, "end": v(-7.74, -35.53) * mm});
            skLineSegment(sketch, "E2399", {"start": v(-7.74, -35.53) * mm, "end": v(-7.73, -35.55) * mm});
            skLineSegment(sketch, "E2400", {"start": v(-7.73, -35.55) * mm, "end": v(-7.73, -35.57) * mm});
            skLineSegment(sketch, "E2401", {"start": v(-7.73, -35.57) * mm, "end": v(-7.73, -35.59) * mm});
            skLineSegment(sketch, "E2402", {"start": v(-7.73, -35.59) * mm, "end": v(-7.74, -35.6) * mm});
            skLineSegment(sketch, "E2403", {"start": v(-7.74, -35.6) * mm, "end": v(-7.74, -35.6) * mm});
            skLineSegment(sketch, "E2404", {"start": v(-7.74, -35.6) * mm, "end": v(-7.88, -35.75) * mm});
            skLineSegment(sketch, "E2405", {"start": v(-7.88, -35.75) * mm, "end": v(-8.03, -35.9) * mm});
            skLineSegment(sketch, "E2406", {"start": v(-8.03, -35.9) * mm, "end": v(-8.17, -36.03) * mm});
            skLineSegment(sketch, "E2407", {"start": v(-8.17, -36.03) * mm, "end": v(-8.18, -36.04) * mm});
            skLineSegment(sketch, "E2408", {"start": v(-8.18, -36.04) * mm, "end": v(-8.19, -36.04) * mm});
            skLineSegment(sketch, "E2409", {"start": v(-8.19, -36.04) * mm, "end": v(-8.2, -36.04) * mm});
            skLineSegment(sketch, "E2410", {"start": v(-8.2, -36.04) * mm, "end": v(-8.22, -36.04) * mm});
            skLineSegment(sketch, "E2411", {"start": v(-8.22, -36.04) * mm, "end": v(-8.24, -36.04) * mm});
            skLineSegment(sketch, "E2412", {"start": v(-8.24, -36.04) * mm, "end": v(-8.26, -36.03) * mm});
            skLineSegment(sketch, "E2413", {"start": v(-8.26, -36.03) * mm, "end": v(-8.29, -36.02) * mm});
            skLineSegment(sketch, "E2414", {"start": v(-8.29, -36.02) * mm, "end": v(-8.31, -36) * mm});
            skLineSegment(sketch, "E2415", {"start": v(-8.31, -36) * mm, "end": v(-8.34, -35.98) * mm});
            skLineSegment(sketch, "E2416", {"start": v(-8.34, -35.98) * mm, "end": v(-8.36, -35.97) * mm});
            skLineSegment(sketch, "E2417", {"start": v(-8.36, -35.97) * mm, "end": v(-8.4, -35.95) * mm});
            skLineSegment(sketch, "E2418", {"start": v(-8.4, -35.95) * mm, "end": v(-8.43, -35.93) * mm});
            skLineSegment(sketch, "E2419", {"start": v(-8.43, -35.93) * mm, "end": v(-8.47, -35.9) * mm});
            skLineSegment(sketch, "E2420", {"start": v(-8.47, -35.9) * mm, "end": v(-8.51, -35.88) * mm});
            skLineSegment(sketch, "E2421", {"start": v(-8.51, -35.88) * mm, "end": v(-8.56, -35.86) * mm});
            skLineSegment(sketch, "E2422", {"start": v(-8.56, -35.86) * mm, "end": v(-8.6, -35.83) * mm});
            skLineSegment(sketch, "E2423", {"start": v(-8.6, -35.83) * mm, "end": v(-8.66, -35.8) * mm});
            skLineSegment(sketch, "E2424", {"start": v(-8.66, -35.8) * mm, "end": v(-8.72, -35.77) * mm});
            skLineSegment(sketch, "E2425", {"start": v(-8.72, -35.77) * mm, "end": v(-8.78, -35.75) * mm});
            skLineSegment(sketch, "E2426", {"start": v(-8.78, -35.75) * mm, "end": v(-8.84, -35.72) * mm});
            skLineSegment(sketch, "E2427", {"start": v(-8.84, -35.72) * mm, "end": v(-8.9, -35.69) * mm});
            skLineSegment(sketch, "E2428", {"start": v(-8.9, -35.69) * mm, "end": v(-8.98, -35.66) * mm});
            skLineSegment(sketch, "E2429", {"start": v(-8.98, -35.66) * mm, "end": v(-9.05, -35.63) * mm});
            skLineSegment(sketch, "E2430", {"start": v(-9.05, -35.63) * mm, "end": v(-9.13, -35.6) * mm});
            skLineSegment(sketch, "E2431", {"start": v(-9.13, -35.6) * mm, "end": v(-9.2, -35.57) * mm});
            skLineSegment(sketch, "E2432", {"start": v(-9.2, -35.57) * mm, "end": v(-9.3, -35.54) * mm});
            skLineSegment(sketch, "E2433", {"start": v(-9.3, -35.54) * mm, "end": v(-9.38, -35.52) * mm});
            skLineSegment(sketch, "E2434", {"start": v(-9.38, -35.52) * mm, "end": v(-9.47, -35.49) * mm});
            skLineSegment(sketch, "E2435", {"start": v(-9.47, -35.49) * mm, "end": v(-9.53, -35.47) * mm});
            skLineSegment(sketch, "E2436", {"start": v(-9.53, -35.47) * mm, "end": v(-9.73, -35.67) * mm});
            skLineSegment(sketch, "E2437", {"start": v(-9.73, -35.67) * mm, "end": v(-9.9, -35.9) * mm});
            skLineSegment(sketch, "E2438", {"start": v(-9.9, -35.9) * mm, "end": v(-9.87, -35.96) * mm});
            skLineSegment(sketch, "E2439", {"start": v(-9.87, -35.96) * mm, "end": v(-9.83, -36.04) * mm});
            skLineSegment(sketch, "E2440", {"start": v(-9.83, -36.04) * mm, "end": v(-9.79, -36.13) * mm});
            skLineSegment(sketch, "E2441", {"start": v(-9.79, -36.13) * mm, "end": v(-9.75, -36.2) * mm});
            skLineSegment(sketch, "E2442", {"start": v(-9.75, -36.2) * mm, "end": v(-9.7, -36.28) * mm});
            skLineSegment(sketch, "E2443", {"start": v(-9.7, -36.28) * mm, "end": v(-9.67, -36.35) * mm});
            skLineSegment(sketch, "E2444", {"start": v(-9.67, -36.35) * mm, "end": v(-9.62, -36.42) * mm});
            skLineSegment(sketch, "E2445", {"start": v(-9.62, -36.42) * mm, "end": v(-9.59, -36.48) * mm});
            skLineSegment(sketch, "E2446", {"start": v(-9.59, -36.48) * mm, "end": v(-9.55, -36.55) * mm});
            skLineSegment(sketch, "E2447", {"start": v(-9.55, -36.55) * mm, "end": v(-9.5, -36.6) * mm});
            skLineSegment(sketch, "E2448", {"start": v(-9.5, -36.6) * mm, "end": v(-9.47, -36.66) * mm});
            skLineSegment(sketch, "E2449", {"start": v(-9.47, -36.66) * mm, "end": v(-9.43, -36.7) * mm});
            skLineSegment(sketch, "E2450", {"start": v(-9.43, -36.7) * mm, "end": v(-9.4, -36.76) * mm});
            skLineSegment(sketch, "E2451", {"start": v(-9.4, -36.76) * mm, "end": v(-9.37, -36.8) * mm});
            skLineSegment(sketch, "E2452", {"start": v(-9.37, -36.8) * mm, "end": v(-9.33, -36.84) * mm});
            skLineSegment(sketch, "E2453", {"start": v(-9.33, -36.84) * mm, "end": v(-9.3, -36.88) * mm});
            skLineSegment(sketch, "E2454", {"start": v(-9.3, -36.88) * mm, "end": v(-9.27, -36.92) * mm});
            skLineSegment(sketch, "E2455", {"start": v(-9.27, -36.92) * mm, "end": v(-9.24, -36.95) * mm});
            skLineSegment(sketch, "E2456", {"start": v(-9.24, -36.95) * mm, "end": v(-9.22, -36.98) * mm});
            skLineSegment(sketch, "E2457", {"start": v(-9.22, -36.98) * mm, "end": v(-9.2, -37) * mm});
            skLineSegment(sketch, "E2458", {"start": v(-9.2, -37) * mm, "end": v(-9.18, -37.02) * mm});
            skLineSegment(sketch, "E2459", {"start": v(-9.18, -37.02) * mm, "end": v(-9.17, -37.04) * mm});
            skLineSegment(sketch, "E2460", {"start": v(-9.17, -37.04) * mm, "end": v(-9.15, -37.07) * mm});
            skLineSegment(sketch, "E2461", {"start": v(-9.15, -37.07) * mm, "end": v(-9.14, -37.09) * mm});
            skLineSegment(sketch, "E2462", {"start": v(-9.14, -37.09) * mm, "end": v(-9.13, -37.1) * mm});
            skLineSegment(sketch, "E2463", {"start": v(-9.13, -37.1) * mm, "end": v(-9.13, -37.12) * mm});
            skLineSegment(sketch, "E2464", {"start": v(-9.13, -37.12) * mm, "end": v(-9.12, -37.14) * mm});
            skLineSegment(sketch, "E2465", {"start": v(-9.12, -37.14) * mm, "end": v(-9.13, -37.15) * mm});
            skLineSegment(sketch, "E2466", {"start": v(-9.13, -37.15) * mm, "end": v(-9.13, -37.16) * mm});
            skLineSegment(sketch, "E2467", {"start": v(-9.13, -37.16) * mm, "end": v(-9.25, -37.32) * mm});
            skLineSegment(sketch, "E2468", {"start": v(-9.25, -37.32) * mm, "end": v(-9.37, -37.49) * mm});
            skLineSegment(sketch, "E2469", {"start": v(-9.37, -37.49) * mm, "end": v(-9.48, -37.65) * mm});
            skLineSegment(sketch, "E2470", {"start": v(-9.48, -37.65) * mm, "end": v(-9.5, -37.65) * mm});
            skLineSegment(sketch, "E2471", {"start": v(-9.5, -37.65) * mm, "end": v(-9.5, -37.66) * mm});
            skLineSegment(sketch, "E2472", {"start": v(-9.5, -37.66) * mm, "end": v(-9.52, -37.66) * mm});
            skLineSegment(sketch, "E2473", {"start": v(-9.52, -37.66) * mm, "end": v(-9.54, -37.66) * mm});
            skLineSegment(sketch, "E2474", {"start": v(-9.54, -37.66) * mm, "end": v(-9.56, -37.66) * mm});
            skLineSegment(sketch, "E2475", {"start": v(-9.56, -37.66) * mm, "end": v(-9.58, -37.66) * mm});
            skLineSegment(sketch, "E2476", {"start": v(-9.58, -37.66) * mm, "end": v(-9.6, -37.65) * mm});
            skLineSegment(sketch, "E2477", {"start": v(-9.6, -37.65) * mm, "end": v(-9.63, -37.64) * mm});
            skLineSegment(sketch, "E2478", {"start": v(-9.63, -37.64) * mm, "end": v(-9.66, -37.63) * mm});
            skLineSegment(sketch, "E2479", {"start": v(-9.66, -37.63) * mm, "end": v(-9.68, -37.62) * mm});
            skLineSegment(sketch, "E2480", {"start": v(-9.68, -37.62) * mm, "end": v(-9.72, -37.6) * mm});
            skLineSegment(sketch, "E2481", {"start": v(-9.72, -37.6) * mm, "end": v(-9.76, -37.59) * mm});
            skLineSegment(sketch, "E2482", {"start": v(-9.76, -37.59) * mm, "end": v(-9.8, -37.57) * mm});
            skLineSegment(sketch, "E2483", {"start": v(-9.8, -37.57) * mm, "end": v(-9.85, -37.55) * mm});
            skLineSegment(sketch, "E2484", {"start": v(-9.85, -37.55) * mm, "end": v(-9.9, -37.53) * mm});
            skLineSegment(sketch, "E2485", {"start": v(-9.9, -37.53) * mm, "end": v(-9.95, -37.51) * mm});
            skLineSegment(sketch, "E2486", {"start": v(-9.95, -37.51) * mm, "end": v(-10, -37.5) * mm});
            skLineSegment(sketch, "E2487", {"start": v(-10, -37.5) * mm, "end": v(-10.07, -37.48) * mm});
            skLineSegment(sketch, "E2488", {"start": v(-10.07, -37.48) * mm, "end": v(-10.13, -37.46) * mm});
            skLineSegment(sketch, "E2489", {"start": v(-10.13, -37.46) * mm, "end": v(-10.2, -37.44) * mm});
            skLineSegment(sketch, "E2490", {"start": v(-10.2, -37.44) * mm, "end": v(-10.27, -37.42) * mm});
            skLineSegment(sketch, "E2491", {"start": v(-10.27, -37.42) * mm, "end": v(-10.34, -37.4) * mm});
            skLineSegment(sketch, "E2492", {"start": v(-10.34, -37.4) * mm, "end": v(-10.42, -37.39) * mm});
            skLineSegment(sketch, "E2493", {"start": v(-10.42, -37.39) * mm, "end": v(-10.5, -37.37) * mm});
            skLineSegment(sketch, "E2494", {"start": v(-10.5, -37.37) * mm, "end": v(-10.58, -37.35) * mm});
            skLineSegment(sketch, "E2495", {"start": v(-10.58, -37.35) * mm, "end": v(-10.67, -37.34) * mm});
            skLineSegment(sketch, "E2496", {"start": v(-10.67, -37.34) * mm, "end": v(-10.76, -37.32) * mm});
            skLineSegment(sketch, "E2497", {"start": v(-10.76, -37.32) * mm, "end": v(-10.86, -37.31) * mm});
            skLineSegment(sketch, "E2498", {"start": v(-10.86, -37.31) * mm, "end": v(-10.92, -37.3) * mm});
            skLineSegment(sketch, "E2499", {"start": v(-10.92, -37.3) * mm, "end": v(-11.09, -37.53) * mm});
            skLineSegment(sketch, "E2500", {"start": v(-11.09, -37.53) * mm, "end": v(-11.22, -37.79) * mm});
            skLineSegment(sketch, "E2501", {"start": v(-11.22, -37.79) * mm, "end": v(-11.18, -37.84) * mm});
            skLineSegment(sketch, "E2502", {"start": v(-11.18, -37.84) * mm, "end": v(-11.12, -37.92) * mm});
            skLineSegment(sketch, "E2503", {"start": v(-11.12, -37.92) * mm, "end": v(-11.07, -38) * mm});
            skLineSegment(sketch, "E2504", {"start": v(-11.07, -38) * mm, "end": v(-11.02, -38.06) * mm});
            skLineSegment(sketch, "E2505", {"start": v(-11.02, -38.06) * mm, "end": v(-10.96, -38.13) * mm});
            skLineSegment(sketch, "E2506", {"start": v(-10.96, -38.13) * mm, "end": v(-10.91, -38.2) * mm});
            skLineSegment(sketch, "E2507", {"start": v(-10.91, -38.2) * mm, "end": v(-10.86, -38.26) * mm});
            skLineSegment(sketch, "E2508", {"start": v(-10.86, -38.26) * mm, "end": v(-10.81, -38.31) * mm});
            skLineSegment(sketch, "E2509", {"start": v(-10.81, -38.31) * mm, "end": v(-10.76, -38.37) * mm});
            skLineSegment(sketch, "E2510", {"start": v(-10.76, -38.37) * mm, "end": v(-10.72, -38.42) * mm});
            skLineSegment(sketch, "E2511", {"start": v(-10.72, -38.42) * mm, "end": v(-10.67, -38.47) * mm});
            skLineSegment(sketch, "E2512", {"start": v(-10.67, -38.47) * mm, "end": v(-10.63, -38.51) * mm});
            skLineSegment(sketch, "E2513", {"start": v(-10.63, -38.51) * mm, "end": v(-10.59, -38.56) * mm});
            skLineSegment(sketch, "E2514", {"start": v(-10.59, -38.56) * mm, "end": v(-10.55, -38.6) * mm});
            skLineSegment(sketch, "E2515", {"start": v(-10.55, -38.6) * mm, "end": v(-10.5, -38.63) * mm});
            skLineSegment(sketch, "E2516", {"start": v(-10.5, -38.63) * mm, "end": v(-10.47, -38.66) * mm});
            skLineSegment(sketch, "E2517", {"start": v(-10.47, -38.66) * mm, "end": v(-10.44, -38.7) * mm});
            skLineSegment(sketch, "E2518", {"start": v(-10.44, -38.7) * mm, "end": v(-10.4, -38.72) * mm});
            skLineSegment(sketch, "E2519", {"start": v(-10.4, -38.72) * mm, "end": v(-10.37, -38.75) * mm});
            skLineSegment(sketch, "E2520", {"start": v(-10.37, -38.75) * mm, "end": v(-10.36, -38.76) * mm});
            skLineSegment(sketch, "E2521", {"start": v(-10.36, -38.76) * mm, "end": v(-10.33, -38.78) * mm});
            skLineSegment(sketch, "E2522", {"start": v(-10.33, -38.78) * mm, "end": v(-10.31, -38.8) * mm});
            skLineSegment(sketch, "E2523", {"start": v(-10.31, -38.8) * mm, "end": v(-10.3, -38.82) * mm});
            skLineSegment(sketch, "E2524", {"start": v(-10.3, -38.82) * mm, "end": v(-10.28, -38.84) * mm});
            skLineSegment(sketch, "E2525", {"start": v(-10.28, -38.84) * mm, "end": v(-10.27, -38.86) * mm});
            skLineSegment(sketch, "E2526", {"start": v(-10.27, -38.86) * mm, "end": v(-10.26, -38.87) * mm});
            skLineSegment(sketch, "E2527", {"start": v(-10.26, -38.87) * mm, "end": v(-10.26, -38.89) * mm});
            skLineSegment(sketch, "E2528", {"start": v(-10.26, -38.89) * mm, "end": v(-10.25, -38.9) * mm});
            skLineSegment(sketch, "E2529", {"start": v(-10.25, -38.9) * mm, "end": v(-10.26, -38.91) * mm});
            skLineSegment(sketch, "E2530", {"start": v(-10.26, -38.91) * mm, "end": v(-10.35, -39.08) * mm});
            skLineSegment(sketch, "E2531", {"start": v(-10.35, -39.08) * mm, "end": v(-10.44, -39.27) * mm});
            skLineSegment(sketch, "E2532", {"start": v(-10.44, -39.27) * mm, "end": v(-10.53, -39.45) * mm});
            skLineSegment(sketch, "E2533", {"start": v(-10.53, -39.45) * mm, "end": v(-10.54, -39.45) * mm});
            skLineSegment(sketch, "E2534", {"start": v(-10.54, -39.45) * mm, "end": v(-10.55, -39.46) * mm});
            skLineSegment(sketch, "E2535", {"start": v(-10.55, -39.46) * mm, "end": v(-10.56, -39.47) * mm});
            skLineSegment(sketch, "E2536", {"start": v(-10.56, -39.47) * mm, "end": v(-10.58, -39.47) * mm});
            skLineSegment(sketch, "E2537", {"start": v(-10.58, -39.47) * mm, "end": v(-10.6, -39.47) * mm});
            skLineSegment(sketch, "E2538", {"start": v(-10.6, -39.47) * mm, "end": v(-10.62, -39.47) * mm});
            skLineSegment(sketch, "E2539", {"start": v(-10.62, -39.47) * mm, "end": v(-10.65, -39.47) * mm});
            skLineSegment(sketch, "E2540", {"start": v(-10.65, -39.47) * mm, "end": v(-10.68, -39.46) * mm});
            skLineSegment(sketch, "E2541", {"start": v(-10.68, -39.46) * mm, "end": v(-10.71, -39.45) * mm});
            skLineSegment(sketch, "E2542", {"start": v(-10.71, -39.45) * mm, "end": v(-10.73, -39.45) * mm});
            skLineSegment(sketch, "E2543", {"start": v(-10.73, -39.45) * mm, "end": v(-10.77, -39.44) * mm});
            skLineSegment(sketch, "E2544", {"start": v(-10.77, -39.44) * mm, "end": v(-10.8, -39.43) * mm});
            skLineSegment(sketch, "E2545", {"start": v(-10.8, -39.43) * mm, "end": v(-10.86, -39.42) * mm});
            skLineSegment(sketch, "E2546", {"start": v(-10.86, -39.42) * mm, "end": v(-10.9, -39.4) * mm});
            skLineSegment(sketch, "E2547", {"start": v(-10.9, -39.4) * mm, "end": v(-10.96, -39.4) * mm});
            skLineSegment(sketch, "E2548", {"start": v(-10.96, -39.4) * mm, "end": v(-11.01, -39.39) * mm});
            skLineSegment(sketch, "E2549", {"start": v(-11.01, -39.39) * mm, "end": v(-11.07, -39.38) * mm});
            skLineSegment(sketch, "E2550", {"start": v(-11.07, -39.38) * mm, "end": v(-11.13, -39.37) * mm});
            skLineSegment(sketch, "E2551", {"start": v(-11.13, -39.37) * mm, "end": v(-11.2, -39.36) * mm});
            skLineSegment(sketch, "E2552", {"start": v(-11.2, -39.36) * mm, "end": v(-11.27, -39.35) * mm});
            skLineSegment(sketch, "E2553", {"start": v(-11.27, -39.35) * mm, "end": v(-11.34, -39.35) * mm});
            skLineSegment(sketch, "E2554", {"start": v(-11.34, -39.35) * mm, "end": v(-11.41, -39.34) * mm});
            skLineSegment(sketch, "E2555", {"start": v(-11.41, -39.34) * mm, "end": v(-11.5, -39.34) * mm});
            skLineSegment(sketch, "E2556", {"start": v(-11.5, -39.34) * mm, "end": v(-11.58, -39.33) * mm});
            skLineSegment(sketch, "E2557", {"start": v(-11.58, -39.33) * mm, "end": v(-11.66, -39.33) * mm});
            skLineSegment(sketch, "E2558", {"start": v(-11.66, -39.33) * mm, "end": v(-11.75, -39.33) * mm});
            skLineSegment(sketch, "E2559", {"start": v(-11.75, -39.33) * mm, "end": v(-11.84, -39.33) * mm});
            skLineSegment(sketch, "E2560", {"start": v(-11.84, -39.33) * mm, "end": v(-11.94, -39.33) * mm});
            skLineSegment(sketch, "E2561", {"start": v(-11.94, -39.33) * mm, "end": v(-12, -39.33) * mm});
            skLineSegment(sketch, "E2562", {"start": v(-12, -39.33) * mm, "end": v(-12.13, -39.58) * mm});
            skLineSegment(sketch, "E2563", {"start": v(-12.13, -39.58) * mm, "end": v(-12.22, -39.86) * mm});
            skLineSegment(sketch, "E2564", {"start": v(-12.22, -39.86) * mm, "end": v(-12.18, -39.9) * mm});
            skLineSegment(sketch, "E2565", {"start": v(-12.18, -39.9) * mm, "end": v(-12.1, -39.97) * mm});
            skLineSegment(sketch, "E2566", {"start": v(-12.1, -39.97) * mm, "end": v(-12.04, -40.04) * mm});
            skLineSegment(sketch, "E2567", {"start": v(-12.04, -40.04) * mm, "end": v(-11.98, -40.1) * mm});
            skLineSegment(sketch, "E2568", {"start": v(-11.98, -40.1) * mm, "end": v(-11.92, -40.16) * mm});
            skLineSegment(sketch, "E2569", {"start": v(-11.92, -40.16) * mm, "end": v(-11.86, -40.21) * mm});
            skLineSegment(sketch, "E2570", {"start": v(-11.86, -40.21) * mm, "end": v(-11.8, -40.26) * mm});
            skLineSegment(sketch, "E2571", {"start": v(-11.8, -40.26) * mm, "end": v(-11.74, -40.31) * mm});
            skLineSegment(sketch, "E2572", {"start": v(-11.74, -40.31) * mm, "end": v(-11.68, -40.36) * mm});
            skLineSegment(sketch, "E2573", {"start": v(-11.68, -40.36) * mm, "end": v(-11.63, -40.4) * mm});
            skLineSegment(sketch, "E2574", {"start": v(-11.63, -40.4) * mm, "end": v(-11.58, -40.44) * mm});
            skLineSegment(sketch, "E2575", {"start": v(-11.58, -40.44) * mm, "end": v(-11.53, -40.48) * mm});
            skLineSegment(sketch, "E2576", {"start": v(-11.53, -40.48) * mm, "end": v(-11.48, -40.52) * mm});
            skLineSegment(sketch, "E2577", {"start": v(-11.48, -40.52) * mm, "end": v(-11.43, -40.55) * mm});
            skLineSegment(sketch, "E2578", {"start": v(-11.43, -40.55) * mm, "end": v(-11.39, -40.58) * mm});
            skLineSegment(sketch, "E2579", {"start": v(-11.39, -40.58) * mm, "end": v(-11.35, -40.6) * mm});
            skLineSegment(sketch, "E2580", {"start": v(-11.35, -40.6) * mm, "end": v(-11.3, -40.63) * mm});
            skLineSegment(sketch, "E2581", {"start": v(-11.3, -40.63) * mm, "end": v(-11.27, -40.65) * mm});
            skLineSegment(sketch, "E2582", {"start": v(-11.27, -40.65) * mm, "end": v(-11.24, -40.67) * mm});
            skLineSegment(sketch, "E2583", {"start": v(-11.24, -40.67) * mm, "end": v(-11.22, -40.68) * mm});
            skLineSegment(sketch, "E2584", {"start": v(-11.22, -40.68) * mm, "end": v(-11.2, -40.7) * mm});
            skLineSegment(sketch, "E2585", {"start": v(-11.2, -40.7) * mm, "end": v(-11.17, -40.72) * mm});
            skLineSegment(sketch, "E2586", {"start": v(-11.17, -40.72) * mm, "end": v(-11.15, -40.73) * mm});
            skLineSegment(sketch, "E2587", {"start": v(-11.15, -40.73) * mm, "end": v(-11.13, -40.75) * mm});
            skLineSegment(sketch, "E2588", {"start": v(-11.13, -40.75) * mm, "end": v(-11.12, -40.76) * mm});
            skLineSegment(sketch, "E2589", {"start": v(-11.12, -40.76) * mm, "end": v(-11.1, -40.78) * mm});
            skLineSegment(sketch, "E2590", {"start": v(-11.1, -40.78) * mm, "end": v(-11.1, -40.8) * mm});
            skLineSegment(sketch, "E2591", {"start": v(-11.1, -40.8) * mm, "end": v(-11.1, -40.8) * mm});
            skLineSegment(sketch, "E2592", {"start": v(-11.1, -40.8) * mm, "end": v(-11.1, -40.82) * mm});
            skLineSegment(sketch, "E2593", {"start": v(-11.1, -40.82) * mm, "end": v(-11.16, -41) * mm});
            skLineSegment(sketch, "E2594", {"start": v(-11.16, -41) * mm, "end": v(-11.22, -41.2) * mm});
            skLineSegment(sketch, "E2595", {"start": v(-11.22, -41.2) * mm, "end": v(-11.28, -41.39) * mm});
            skLineSegment(sketch, "E2596", {"start": v(-11.28, -41.39) * mm, "end": v(-11.29, -41.4) * mm});
            skLineSegment(sketch, "E2597", {"start": v(-11.29, -41.4) * mm, "end": v(-11.3, -41.4) * mm});
            skLineSegment(sketch, "E2598", {"start": v(-11.3, -41.4) * mm, "end": v(-11.31, -41.41) * mm});
            skLineSegment(sketch, "E2599", {"start": v(-11.31, -41.41) * mm, "end": v(-11.33, -41.42) * mm});
            skLineSegment(sketch, "E2600", {"start": v(-11.33, -41.42) * mm, "end": v(-11.35, -41.42) * mm});
            skLineSegment(sketch, "E2601", {"start": v(-11.35, -41.42) * mm, "end": v(-11.37, -41.42) * mm});
            skLineSegment(sketch, "E2602", {"start": v(-11.37, -41.42) * mm, "end": v(-11.4, -41.43) * mm});
            skLineSegment(sketch, "E2603", {"start": v(-11.4, -41.43) * mm, "end": v(-11.43, -41.42) * mm});
            skLineSegment(sketch, "E2604", {"start": v(-11.43, -41.42) * mm, "end": v(-11.46, -41.42) * mm});
            skLineSegment(sketch, "E2605", {"start": v(-11.46, -41.42) * mm, "end": v(-11.48, -41.42) * mm});
            skLineSegment(sketch, "E2606", {"start": v(-11.48, -41.42) * mm, "end": v(-11.52, -41.42) * mm});
            skLineSegment(sketch, "E2607", {"start": v(-11.52, -41.42) * mm, "end": v(-11.56, -41.41) * mm});
            skLineSegment(sketch, "E2608", {"start": v(-11.56, -41.41) * mm, "end": v(-11.6, -41.4) * mm});
            skLineSegment(sketch, "E2609", {"start": v(-11.6, -41.4) * mm, "end": v(-11.66, -41.4) * mm});
            skLineSegment(sketch, "E2610", {"start": v(-11.66, -41.4) * mm, "end": v(-11.71, -41.4) * mm});
            skLineSegment(sketch, "E2611", {"start": v(-11.71, -41.4) * mm, "end": v(-11.77, -41.4) * mm});
            skLineSegment(sketch, "E2612", {"start": v(-11.77, -41.4) * mm, "end": v(-11.83, -41.4) * mm});
            skLineSegment(sketch, "E2613", {"start": v(-11.83, -41.4) * mm, "end": v(-11.89, -41.4) * mm});
            skLineSegment(sketch, "E2614", {"start": v(-11.89, -41.4) * mm, "end": v(-11.96, -41.4) * mm});
            skLineSegment(sketch, "E2615", {"start": v(-11.96, -41.4) * mm, "end": v(-12.03, -41.41) * mm});
            skLineSegment(sketch, "E2616", {"start": v(-12.03, -41.41) * mm, "end": v(-12.1, -41.42) * mm});
            skLineSegment(sketch, "E2617", {"start": v(-12.1, -41.42) * mm, "end": v(-12.17, -41.42) * mm});
            skLineSegment(sketch, "E2618", {"start": v(-12.17, -41.42) * mm, "end": v(-12.25, -41.43) * mm});
            skLineSegment(sketch, "E2619", {"start": v(-12.25, -41.43) * mm, "end": v(-12.33, -41.44) * mm});
            skLineSegment(sketch, "E2620", {"start": v(-12.33, -41.44) * mm, "end": v(-12.42, -41.45) * mm});
            skLineSegment(sketch, "E2621", {"start": v(-12.42, -41.45) * mm, "end": v(-12.5, -41.46) * mm});
            skLineSegment(sketch, "E2622", {"start": v(-12.5, -41.46) * mm, "end": v(-12.6, -41.48) * mm});
            skLineSegment(sketch, "E2623", {"start": v(-12.6, -41.48) * mm, "end": v(-12.7, -41.5) * mm});
            skLineSegment(sketch, "E2624", {"start": v(-12.7, -41.5) * mm, "end": v(-12.76, -41.5) * mm});
            skLineSegment(sketch, "E2625", {"start": v(-12.76, -41.5) * mm, "end": v(-12.84, -41.77) * mm});
            skLineSegment(sketch, "E2626", {"start": v(-12.84, -41.77) * mm, "end": v(-12.89, -42.06) * mm});
            skLineSegment(sketch, "E2627", {"start": v(-12.89, -42.06) * mm, "end": v(-12.84, -42.1) * mm});
            skLineSegment(sketch, "E2628", {"start": v(-12.84, -42.1) * mm, "end": v(-12.76, -42.15) * mm});
            skLineSegment(sketch, "E2629", {"start": v(-12.76, -42.15) * mm, "end": v(-12.69, -42.2) * mm});
            skLineSegment(sketch, "E2630", {"start": v(-12.69, -42.2) * mm, "end": v(-12.61, -42.26) * mm});
            skLineSegment(sketch, "E2631", {"start": v(-12.61, -42.26) * mm, "end": v(-12.54, -42.3) * mm});
            skLineSegment(sketch, "E2632", {"start": v(-12.54, -42.3) * mm, "end": v(-12.47, -42.35) * mm});
            skLineSegment(sketch, "E2633", {"start": v(-12.47, -42.35) * mm, "end": v(-12.4, -42.4) * mm});
            skLineSegment(sketch, "E2634", {"start": v(-12.4, -42.4) * mm, "end": v(-12.34, -42.43) * mm});
            skLineSegment(sketch, "E2635", {"start": v(-12.34, -42.43) * mm, "end": v(-12.28, -42.47) * mm});
            skLineSegment(sketch, "E2636", {"start": v(-12.28, -42.47) * mm, "end": v(-12.22, -42.5) * mm});
            skLineSegment(sketch, "E2637", {"start": v(-12.22, -42.5) * mm, "end": v(-12.16, -42.54) * mm});
            skLineSegment(sketch, "E2638", {"start": v(-12.16, -42.54) * mm, "end": v(-12.1, -42.57) * mm});
            skLineSegment(sketch, "E2639", {"start": v(-12.1, -42.57) * mm, "end": v(-12.05, -42.6) * mm});
            skLineSegment(sketch, "E2640", {"start": v(-12.05, -42.6) * mm, "end": v(-12, -42.62) * mm});
            skLineSegment(sketch, "E2641", {"start": v(-12, -42.62) * mm, "end": v(-11.95, -42.64) * mm});
            skLineSegment(sketch, "E2642", {"start": v(-11.95, -42.64) * mm, "end": v(-11.9, -42.66) * mm});
            skLineSegment(sketch, "E2643", {"start": v(-11.9, -42.66) * mm, "end": v(-11.87, -42.68) * mm});
            skLineSegment(sketch, "E2644", {"start": v(-11.87, -42.68) * mm, "end": v(-11.83, -42.7) * mm});
            skLineSegment(sketch, "E2645", {"start": v(-11.83, -42.7) * mm, "end": v(-11.79, -42.7) * mm});
            skLineSegment(sketch, "E2646", {"start": v(-11.79, -42.7) * mm, "end": v(-11.77, -42.72) * mm});
            skLineSegment(sketch, "E2647", {"start": v(-11.77, -42.72) * mm, "end": v(-11.74, -42.73) * mm});
            skLineSegment(sketch, "E2648", {"start": v(-11.74, -42.73) * mm, "end": v(-11.71, -42.74) * mm});
            skLineSegment(sketch, "E2649", {"start": v(-11.71, -42.74) * mm, "end": v(-11.7, -42.75) * mm});
            skLineSegment(sketch, "E2650", {"start": v(-11.7, -42.75) * mm, "end": v(-11.67, -42.77) * mm});
            skLineSegment(sketch, "E2651", {"start": v(-11.67, -42.77) * mm, "end": v(-11.66, -42.78) * mm});
            skLineSegment(sketch, "E2652", {"start": v(-11.66, -42.78) * mm, "end": v(-11.64, -42.8) * mm});
            skLineSegment(sketch, "E2653", {"start": v(-11.64, -42.8) * mm, "end": v(-11.63, -42.8) * mm});
            skLineSegment(sketch, "E2654", {"start": v(-11.63, -42.8) * mm, "end": v(-11.63, -42.82) * mm});
            skLineSegment(sketch, "E2655", {"start": v(-11.63, -42.82) * mm, "end": v(-11.63, -42.83) * mm});
            skLineSegment(sketch, "E2656", {"start": v(-11.63, -42.83) * mm, "end": v(-11.66, -43.02) * mm});
            skLineSegment(sketch, "E2657", {"start": v(-11.66, -43.02) * mm, "end": v(-11.7, -43.23) * mm});
            skLineSegment(sketch, "E2658", {"start": v(-11.7, -43.23) * mm, "end": v(-11.72, -43.42) * mm});
            skLineSegment(sketch, "E2659", {"start": v(-11.72, -43.42) * mm, "end": v(-11.73, -43.43) * mm});
            skLineSegment(sketch, "E2660", {"start": v(-11.73, -43.43) * mm, "end": v(-11.74, -43.44) * mm});
            skLineSegment(sketch, "E2661", {"start": v(-11.74, -43.44) * mm, "end": v(-11.75, -43.45) * mm});
            skLineSegment(sketch, "E2662", {"start": v(-11.75, -43.45) * mm, "end": v(-11.76, -43.46) * mm});
            skLineSegment(sketch, "E2663", {"start": v(-11.76, -43.46) * mm, "end": v(-11.78, -43.47) * mm});
            skLineSegment(sketch, "E2664", {"start": v(-11.78, -43.47) * mm, "end": v(-11.8, -43.47) * mm});
            skLineSegment(sketch, "E2665", {"start": v(-11.8, -43.47) * mm, "end": v(-11.83, -43.48) * mm});
            skLineSegment(sketch, "E2666", {"start": v(-11.83, -43.48) * mm, "end": v(-11.86, -43.48) * mm});
            skLineSegment(sketch, "E2667", {"start": v(-11.86, -43.48) * mm, "end": v(-11.9, -43.48) * mm});
            skLineSegment(sketch, "E2668", {"start": v(-11.9, -43.48) * mm, "end": v(-11.91, -43.49) * mm});
            skLineSegment(sketch, "E2669", {"start": v(-11.91, -43.49) * mm, "end": v(-11.95, -43.49) * mm});
            skLineSegment(sketch, "E2670", {"start": v(-11.95, -43.49) * mm, "end": v(-12, -43.5) * mm});
            skLineSegment(sketch, "E2671", {"start": v(-12, -43.5) * mm, "end": v(-12.04, -43.5) * mm});
            skLineSegment(sketch, "E2672", {"start": v(-12.04, -43.5) * mm, "end": v(-12.1, -43.5) * mm});
            skLineSegment(sketch, "E2673", {"start": v(-12.1, -43.5) * mm, "end": v(-12.14, -43.5) * mm});
            skLineSegment(sketch, "E2674", {"start": v(-12.14, -43.5) * mm, "end": v(-12.2, -43.52) * mm});
            skLineSegment(sketch, "E2675", {"start": v(-12.2, -43.52) * mm, "end": v(-12.26, -43.52) * mm});
            skLineSegment(sketch, "E2676", {"start": v(-12.26, -43.52) * mm, "end": v(-12.32, -43.54) * mm});
            skLineSegment(sketch, "E2677", {"start": v(-12.32, -43.54) * mm, "end": v(-12.38, -43.55) * mm});
            skLineSegment(sketch, "E2678", {"start": v(-12.38, -43.55) * mm, "end": v(-12.45, -43.56) * mm});
            skLineSegment(sketch, "E2679", {"start": v(-12.45, -43.56) * mm, "end": v(-12.52, -43.58) * mm});
            skLineSegment(sketch, "E2680", {"start": v(-12.52, -43.58) * mm, "end": v(-12.6, -43.6) * mm});
            skLineSegment(sketch, "E2681", {"start": v(-12.6, -43.6) * mm, "end": v(-12.67, -43.62) * mm});
            skLineSegment(sketch, "E2682", {"start": v(-12.67, -43.62) * mm, "end": v(-12.75, -43.64) * mm});
            skLineSegment(sketch, "E2683", {"start": v(-12.75, -43.64) * mm, "end": v(-12.84, -43.66) * mm});
            skLineSegment(sketch, "E2684", {"start": v(-12.84, -43.66) * mm, "end": v(-12.92, -43.69) * mm});
            skLineSegment(sketch, "E2685", {"start": v(-12.92, -43.69) * mm, "end": v(-13, -43.72) * mm});
            skLineSegment(sketch, "E2686", {"start": v(-13, -43.72) * mm, "end": v(-13.1, -43.75) * mm});
            skLineSegment(sketch, "E2687", {"start": v(-13.1, -43.75) * mm, "end": v(-13.16, -43.77) * mm});
            skLineSegment(sketch, "E2688", {"start": v(1.32, -44.85) * mm, "end": v(1.4, -44.84) * mm});
            skLineSegment(sketch, "E2689", {"start": v(1.4, -44.84) * mm, "end": v(1.47, -44.84) * mm});
            skLineSegment(sketch, "E2690", {"start": v(1.47, -44.84) * mm, "end": v(1.55, -44.86) * mm});
            skLineSegment(sketch, "E2691", {"start": v(1.55, -44.86) * mm, "end": v(1.62, -44.89) * mm});
            skLineSegment(sketch, "E2692", {"start": v(1.62, -44.89) * mm, "end": v(1.68, -44.93) * mm});
            skLineSegment(sketch, "E2693", {"start": v(1.68, -44.93) * mm, "end": v(1.73, -45) * mm});
            skLineSegment(sketch, "E2694", {"start": v(1.73, -45) * mm, "end": v(1.76, -45.06) * mm});
            skLineSegment(sketch, "E2695", {"start": v(1.76, -45.06) * mm, "end": v(1.78, -45.13) * mm});
            skLineSegment(sketch, "E2696", {"start": v(1.78, -45.13) * mm, "end": v(1.8, -45.2) * mm});
            skLineSegment(sketch, "E2697", {"start": v(1.8, -45.2) * mm, "end": v(1.78, -45.29) * mm});
            skLineSegment(sketch, "E2698", {"start": v(1.78, -45.29) * mm, "end": v(1.75, -45.36) * mm});
            skLineSegment(sketch, "E2699", {"start": v(1.75, -45.36) * mm, "end": v(1.71, -45.42) * mm});
            skLineSegment(sketch, "E2700", {"start": v(1.71, -45.42) * mm, "end": v(1.66, -45.48) * mm});
            skLineSegment(sketch, "E2701", {"start": v(1.66, -45.48) * mm, "end": v(1.6, -45.52) * mm});
            skLineSegment(sketch, "E2702", {"start": v(1.6, -45.52) * mm, "end": v(1.53, -45.55) * mm});
            skLineSegment(sketch, "E2703", {"start": v(1.53, -45.55) * mm, "end": v(1.45, -45.56) * mm});
            skLineSegment(sketch, "E2704", {"start": v(1.45, -45.56) * mm, "end": v(1.38, -45.56) * mm});
            skLineSegment(sketch, "E2705", {"start": v(1.38, -45.56) * mm, "end": v(1.3, -45.54) * mm});
            skLineSegment(sketch, "E2706", {"start": v(1.3, -45.54) * mm, "end": v(1.23, -45.51) * mm});
            skLineSegment(sketch, "E2707", {"start": v(1.23, -45.51) * mm, "end": v(1.17, -45.47) * mm});
            skLineSegment(sketch, "E2708", {"start": v(1.17, -45.47) * mm, "end": v(1.12, -45.4) * mm});
            skLineSegment(sketch, "E2709", {"start": v(1.12, -45.4) * mm, "end": v(1.09, -45.34) * mm});
            skLineSegment(sketch, "E2710", {"start": v(1.09, -45.34) * mm, "end": v(1.06, -45.27) * mm});
            skLineSegment(sketch, "E2711", {"start": v(1.06, -45.27) * mm, "end": v(1.06, -45.2) * mm});
            skLineSegment(sketch, "E2712", {"start": v(1.06, -45.2) * mm, "end": v(1.07, -45.11) * mm});
            skLineSegment(sketch, "E2713", {"start": v(1.07, -45.11) * mm, "end": v(1.1, -45.04) * mm});
            skLineSegment(sketch, "E2714", {"start": v(1.1, -45.04) * mm, "end": v(1.13, -44.98) * mm});
            skLineSegment(sketch, "E2715", {"start": v(1.13, -44.98) * mm, "end": v(1.19, -44.92) * mm});
            skLineSegment(sketch, "E2716", {"start": v(1.19, -44.92) * mm, "end": v(1.25, -44.88) * mm});
            skLineSegment(sketch, "E2717", {"start": v(1.25, -44.88) * mm, "end": v(1.32, -44.85) * mm});
            skLineSegment(sketch, "E2718", {"start": v(-13.26, -52.57) * mm, "end": v(-16.05, -52.57) * mm});
            skLineSegment(sketch, "E2719", {"start": v(-16.05, -52.57) * mm, "end": v(-13.26, -52.57) * mm});
            skLineSegment(sketch, "E2720", {"start": v(-16.05, -24.04) * mm, "end": v(-16.05, -0.2) * mm});
            skLineSegment(sketch, "E2721", {"start": v(-16.05, -24.04) * mm, "end": v(-16.05, -52.57) * mm});
            skLineSegment(sketch, "E2722", {"start": v(-16.05, -17.45) * mm, "end": v(-16.05, -24.04) * mm});
            skLineSegment(sketch, "E2723", {"start": v(-16.05, -52.57) * mm, "end": v(-14.66, -52.57) * mm});
            skLineSegment(sketch, "E2724", {"start": v(-14.66, -52.57) * mm, "end": v(-15.35, -52.57) * mm});
            skLineSegment(sketch, "E2725", {"start": v(-15.35, -52.57) * mm, "end": v(-15.35, -0.2) * mm});
            skSolve(sketch);
        }
        {
            var Q0;
            Q0=qCreatedBy(makeId("Front.planeOp"),FACE);
            var sketch = newSketch(context, id + "F1", { "sketchPlane" : qUnion([Q0])});
            skLineSegment(sketch, "E2726", {"start": v(67.21, 97.26) * mm, "end": v(10.21, 97.26) * mm});
            skLineSegment(sketch, "E2727", {"start": v(10.21, 40.26) * mm, "end": v(67.21, 40.26) * mm});
            skLineSegment(sketch, "E2728", {"start": v(67.21, 97.26) * mm, "end": v(67.21, 79.26) * mm});
            skLineSegment(sketch, "E2729", {"start": v(67.21, 79.26) * mm, "end": v(67.21, 77.76) * mm, "construction": true});
            skLineSegment(sketch, "E2730", {"start": v(67.21, 77.76) * mm, "end": v(67.21, 59.76) * mm});
            skLineSegment(sketch, "E2731", {"start": v(67.21, 59.76) * mm, "end": v(67.21, 58.26) * mm, "construction": true});
            skLineSegment(sketch, "E2732", {"start": v(67.21, 58.26) * mm, "end": v(67.21, 40.26) * mm});
            skLineSegment(sketch, "E2733", {"start": v(67.21, 79.26) * mm, "end": v(10.21, 79.26) * mm});
            skPoint(sketch, "E2733.endSnap0", {"position": v(10.21, 68.76) * mm});
            skLineSegment(sketch, "E2734", {"start": v(67.21, 77.76) * mm, "end": v(10.21, 77.76) * mm});
            skLineSegment(sketch, "E2735", {"start": v(67.21, 59.76) * mm, "end": v(10.21, 59.76) * mm});
            skLineSegment(sketch, "E2736", {"start": v(67.21, 58.26) * mm, "end": v(10.21, 58.26) * mm});
            skLineSegment(sketch, "E2737", {"start": v(10.21, 79.26) * mm, "end": v(10.21, 77.76) * mm, "construction": true});
            skLineSegment(sketch, "E2738", {"start": v(10.21, 59.76) * mm, "end": v(10.21, 58.26) * mm, "construction": true});
            skLineSegment(sketch, "E2739", {"start": v(10.21, 97.26) * mm, "end": v(10.21, 79.26) * mm});
            skLineSegment(sketch, "E2740", {"start": v(10.21, 77.76) * mm, "end": v(10.21, 59.76) * mm});
            skLineSegment(sketch, "E2741", {"start": v(10.21, 58.26) * mm, "end": v(10.21, 40.26) * mm});
            skLineSegment(sketch, "E2742", {"start": v(67.21, 49.26) * mm, "end": v(67.21, 68.76) * mm, "construction": true});
            skLineSegment(sketch, "E2743", {"start": v(10.21, 49.26) * mm, "end": v(29.21, 49.26) * mm, "construction": true});
            skLineSegment(sketch, "E2744", {"start": v(29.21, 49.26) * mm, "end": v(48.21, 49.26) * mm, "construction": true});
            skLineSegment(sketch, "E2745", {"start": v(48.21, 49.26) * mm, "end": v(67.21, 49.26) * mm, "construction": true});
            skLineSegment(sketch, "E2746", {"start": v(10.21, 68.76) * mm, "end": v(29.21, 68.76) * mm, "construction": true});
            skLineSegment(sketch, "E2747", {"start": v(29.21, 68.76) * mm, "end": v(48.21, 68.76) * mm, "construction": true});
            skLineSegment(sketch, "E2748", {"start": v(48.21, 68.76) * mm, "end": v(67.21, 68.76) * mm, "construction": true});
            skLineSegment(sketch, "E2749", {"start": v(10.21, 88.26) * mm, "end": v(29.21, 88.26) * mm, "construction": true});
            skLineSegment(sketch, "E2750", {"start": v(29.21, 88.26) * mm, "end": v(48.21, 88.26) * mm, "construction": true});
            skLineSegment(sketch, "E2751", {"start": v(48.21, 88.26) * mm, "end": v(67.21, 88.26) * mm, "construction": true});
            skCircle(sketch, "E2752", {"center": v(29.21, 49.26) * mm, "radius": 1.5 * mm});
            skCircle(sketch, "E2753", {"center": v(48.21, 49.26) * mm, "radius": 1.5 * mm});
            skCircle(sketch, "E2754", {"center": v(29.21, 68.76) * mm, "radius": 1.5 * mm});
            skCircle(sketch, "E2755", {"center": v(48.21, 68.76) * mm, "radius": 1.5 * mm});
            skCircle(sketch, "E2756", {"center": v(29.21, 88.26) * mm, "radius": 1.5 * mm});
            skCircle(sketch, "E2757", {"center": v(48.21, 88.26) * mm, "radius": 1.5 * mm});
            skSolve(sketch);
        }
        {
            var Q0;
            Q0=makeQuery(id+"F1.imprint","IMPRINT",FACE,{"disambiguationData":[TD([[makeQuery(id+"F1.imprint","IMPRINT",EDGE,{"derivedFrom":sQuery(id+"F1.wireOp",EDGE,"E2726")}),1.0]])]});
            var Q1;
            Q1=makeQuery(id+"F1.imprint","IMPRINT",FACE,{"disambiguationData":[TD([[makeQuery(id+"F1.imprint","IMPRINT",EDGE,{"derivedFrom":sQuery(id+"F1.wireOp",EDGE,"E2730")}),-1.0]])]});
            var Q2;
            Q2=makeQuery(id+"F1.imprint","IMPRINT",FACE,{"disambiguationData":[TD([[makeQuery(id+"F1.imprint","IMPRINT",EDGE,{"derivedFrom":sQuery(id+"F1.wireOp",EDGE,"E2727")}),1.0]])]});
            extrude(context, id + "F2", {"entities" : qUnion([Q0, Q1, Q2]), "endBound" : BoundingType.SYMMETRIC, "depth" : 57 * mm, "offsetDistance" : 25 * mm});
        }
        {
            var Q0;
            Q0 = qSketchRegion(id + "F0", true);
            extrude(context, id + "F3", {"entities" : qUnion([Q0]), "endBound" : BoundingType.SYMMETRIC, "depth" : 5 * mm, "offsetDistance" : 25 * mm});
        }
        {
            var Q0;
            {var subQ0=sQuery(id+"F0.wireOp",EDGE,"E2720");Q0=makeQuery(id+"F0.imprint","IMPRINT",FACE,{"disambiguationData":[TD([[makeQuery(id+"F0.imprint","IMPRINT",EDGE,{"derivedFrom":subQ0}),-1.0]])]});}
            extrude(context, id + "F4", {"entities" : qUnion([Q0]), "operationType" : NewBodyOperationType.ADD, "endBound" : BoundingType.SYMMETRIC, "depth" : 7.5 * mm, "offsetDistance" : 25 * mm});
        }
        {
            var Q0;
            Q0=qCreatedBy(makeId("Front.planeOp"),FACE);
            var sketch = newSketch(context, id + "F5", { "sketchPlane" : qUnion([Q0])});
            skLineSegment(sketch, "E2758", {"start": v(-151.7, 32.57) * mm, "end": v(-149.2, 32.57) * mm});
            skLineSegment(sketch, "E2759", {"start": v(-149.2, 32.57) * mm, "end": v(-149.2, 17.57) * mm});
            skLineSegment(sketch, "E2760", {"start": v(-151.7, 14.57) * mm, "end": v(-151.7, 17.57) * mm});
            skLineSegment(sketch, "E2761", {"start": v(-151.7, 17.57) * mm, "end": v(-151.7, 32.57) * mm});
            skLineSegment(sketch, "E2762", {"start": v(-151.7, 14.57) * mm, "end": v(-149.2, 14.57) * mm});
            skLineSegment(sketch, "E2763", {"start": v(-149.2, 14.57) * mm, "end": v(-119.94, 14.57) * mm});
            skLineSegment(sketch, "E2764.MirrorCS", {"start": v(-90.7, 14.57) * mm, "end": v(-119.94, 14.57) * mm});
            skLineSegment(sketch, "E2765.MirrorCS", {"start": v(-89.7, 14.57) * mm, "end": v(-92.2, 14.57) * mm});
            skLineSegment(sketch, "E2766.MirrorCS", {"start": v(-89.7, 14.57) * mm, "end": v(-89.7, 17.57) * mm});
            skLineSegment(sketch, "E2767.MirrorCS", {"start": v(-89.7, 32.57) * mm, "end": v(-92.2, 32.57) * mm});
            skLineSegment(sketch, "E2768.MirrorCS", {"start": v(-92.2, 32.57) * mm, "end": v(-92.2, 17.57) * mm});
            skLineSegment(sketch, "E2769", {"start": v(-149.2, 17.57) * mm, "end": v(-92.2, 17.57) * mm});
            skLineSegment(sketch, "E2770", {"start": v(-149.2, 17.57) * mm, "end": v(-151.7, 17.57) * mm, "construction": true});
            skLineSegment(sketch, "E2771", {"start": v(-92.2, 17.57) * mm, "end": v(-89.7, 17.57) * mm, "construction": true});
            skLineSegment(sketch, "E2772", {"start": v(-151.7, 17.57) * mm, "end": v(-149.2, 17.57) * mm});
            skLineSegment(sketch, "E2773", {"start": v(-92.2, 17.57) * mm, "end": v(-89.7, 17.57) * mm});
            skLineSegment(sketch, "E2774", {"start": v(-119.94, 14.57) * mm, "end": v(-90.7, 14.57) * mm});
            skLineSegment(sketch, "E2775", {"start": v(-92.2, 14.57) * mm, "end": v(-92.2, 17.57) * mm});
            skLineSegment(sketch, "E2776", {"start": v(-149.2, 14.57) * mm, "end": v(-149.2, 17.57) * mm});
            skLineSegment(sketch, "E2777", {"start": v(-89.7, 17.57) * mm, "end": v(-89.7, 32.57) * mm});
            skSolve(sketch);
        }
        {
            var Q0;
            Q0=makeQuery(id+"F5.imprint","IMPRINT",FACE,{"disambiguationData":[TD([[makeQuery(id+"F5.imprint","IMPRINT",EDGE,{"derivedFrom":sQuery(id+"F5.wireOp",EDGE,"E2763")}),1.0]])]});
            var Q1;
            Q1=makeQuery(id+"F5.imprint","IMPRINT",FACE,{"disambiguationData":[TD([[makeQuery(id+"F5.imprint","IMPRINT",EDGE,{"derivedFrom":sQuery(id+"F5.wireOp",EDGE,"E2760")}),-1.0]])]});
            var Q2;
            Q2=makeQuery(id+"F5.imprint","IMPRINT",FACE,{"disambiguationData":[TD([[makeQuery(id+"F5.imprint","IMPRINT",EDGE,{"derivedFrom":sQuery(id+"F5.wireOp",EDGE,"E2765.MirrorCS")}),-1.0]])]});
            extrude(context, id + "F6", {"entities" : qUnion([Q0, Q1, Q2]), "endBound" : BoundingType.SYMMETRIC, "depth" : 15 * mm, "offsetDistance" : 25 * mm});
        }
        {
            var Q0;
            Q0=makeQuery(id+"F5.imprint","IMPRINT",FACE,{"disambiguationData":[TD([[makeQuery(id+"F5.imprint","IMPRINT",EDGE,{"derivedFrom":sQuery(id+"F5.wireOp",EDGE,"E2767.MirrorCS")}),1.0]])]});
            var Q1;
            Q1=makeQuery(id+"F5.imprint","IMPRINT",FACE,{"disambiguationData":[TD([[makeQuery(id+"F5.imprint","IMPRINT",EDGE,{"derivedFrom":sQuery(id+"F5.wireOp",EDGE,"E2758")}),-1.0]])]});
            extrude(context, id + "F7", {"entities" : qUnion([Q0, Q1]), "operationType" : NewBodyOperationType.ADD, "endBound" : BoundingType.SYMMETRIC, "depth" : 25 * mm, "offsetDistance" : 25 * mm});
        }
        {
            var Q0;
            Q0=qCreatedBy(makeId("Top.planeOp"),FACE);
            var sketch = newSketch(context, id + "F8", { "sketchPlane" : qUnion([Q0])});
            skLineSegment(sketch, "E2778", {"start": v(-89.7, -7.5) * mm, "end": v(-89.7, 7.5) * mm, "construction": true});
            skLineSegment(sketch, "E2779", {"start": v(-89.7, 0) * mm, "end": v(-151.7, 0) * mm, "construction": true});
            skLineSegment(sketch, "E2780", {"start": v(-151.7, 0) * mm, "end": v(-151.7, -2.5) * mm, "construction": true});
            skLineSegment(sketch, "E2781", {"start": v(-151.7, -2.5) * mm, "end": v(-151.7, -5) * mm, "construction": true});
            skLineSegment(sketch, "E2782", {"start": v(-151.7, -5) * mm, "end": v(-151.7, -7.5) * mm, "construction": true});
            skLineSegment(sketch, "E2783", {"start": v(-151.7, -2.5) * mm, "end": v(-89.7, -2.5) * mm, "construction": true});
            skLineSegment(sketch, "E2784", {"start": v(-89.7, -2.5) * mm, "end": v(-89.7, -5) * mm, "construction": true});
            skLineSegment(sketch, "E2785", {"start": v(-89.7, -5) * mm, "end": v(-89.7, -7.5) * mm, "construction": true});
            skLineSegment(sketch, "E2786", {"start": v(-89.7, -2.5) * mm, "end": v(-89.7, 0) * mm, "construction": true});
            skLineSegment(sketch, "E2787.MirrorCS", {"start": v(-151.7, 5) * mm, "end": v(-89.7, 5) * mm, "construction": true});
            skLineSegment(sketch, "E2788.MirrorCS", {"start": v(-151.7, 0) * mm, "end": v(-151.7, 2.5) * mm, "construction": true});
            skLineSegment(sketch, "E2789.MirrorCS", {"start": v(-151.7, 2.5) * mm, "end": v(-151.7, 5) * mm, "construction": true});
            skLineSegment(sketch, "E2790.MirrorCS", {"start": v(-151.7, 5) * mm, "end": v(-151.7, 7.5) * mm, "construction": true});
            skLineSegment(sketch, "E2791", {"start": v(-89.7, -7.5) * mm, "end": v(-120.7, -7.5) * mm, "construction": true});
            skLineSegment(sketch, "E2792", {"start": v(-120.7, -7.5) * mm, "end": v(-151.7, -7.5) * mm, "construction": true});
            skLineSegment(sketch, "E2793", {"start": v(-120.7, -7.5) * mm, "end": v(-120.7, 7.5) * mm, "construction": true});
            skLineSegment(sketch, "E2794", {"start": v(-89.7, 7.5) * mm, "end": v(-151.7, 7.5) * mm, "construction": true});
            skLineSegment(sketch, "E2795", {"start": v(-89.7, 7.5) * mm, "end": v(-120.7, 7.5) * mm, "construction": true});
            skLineSegment(sketch, "E2796", {"start": v(-105.2, 7.5) * mm, "end": v(-105.2, -7.5) * mm, "construction": true});
            skLineSegment(sketch, "E2797", {"start": v(-105.2, -7.5) * mm, "end": v(-136.2, -7.5) * mm, "construction": true});
            skLineSegment(sketch, "E2798", {"start": v(-136.2, -7.5) * mm, "end": v(-136.2, 7.5) * mm, "construction": true});
            skLineSegment(sketch, "E2799", {"start": v(-105.2, -2.5) * mm, "end": v(-120.7, -2.5) * mm, "construction": true});
            skLineSegment(sketch, "E2800", {"start": v(-105.2, 0) * mm, "end": v(-105.2, -2.5) * mm, "construction": true});
            skLineSegment(sketch, "E2801", {"start": v(-105.2, 0) * mm, "end": v(-120.7, 0) * mm, "construction": true});
            skLineSegment(sketch, "E2802", {"start": v(-120.7, 0) * mm, "end": v(-136.2, 0) * mm, "construction": true});
            skLineSegment(sketch, "E2803", {"start": v(-136.2, 0) * mm, "end": v(-136.2, -2.5) * mm, "construction": true});
            skLineSegment(sketch, "E2804", {"start": v(-105.2, -2.5) * mm, "end": v(-105.2, -5) * mm, "construction": true});
            skLineSegment(sketch, "E2805", {"start": v(-120.7, -5) * mm, "end": v(-136.2, -5) * mm, "construction": true});
            skLineSegment(sketch, "E2806", {"start": v(-136.2, -5) * mm, "end": v(-136.2, -2.5) * mm, "construction": true});
            skLineSegment(sketch, "E2807", {"start": v(-105.2, -2.5) * mm, "end": v(-136.2, -2.5) * mm, "construction": true});
            skLineSegment(sketch, "E2808", {"start": v(-136.2, 2.5) * mm, "end": v(-136.2, 5) * mm, "construction": true});
            skLineSegment(sketch, "E2809", {"start": v(-136.2, 5) * mm, "end": v(-105.2, 5) * mm, "construction": true});
            skLineSegment(sketch, "E2810", {"start": v(-105.2, -5) * mm, "end": v(-105.2, -2.5) * mm});
            skLineSegment(sketch, "E2811", {"start": v(-136.2, -2.5) * mm, "end": v(-105.2, -2.5) * mm});
            skLineSegment(sketch, "E2812", {"start": v(-136.2, -2.5) * mm, "end": v(-136.2, -5) * mm});
            skLineSegment(sketch, "E2813", {"start": v(-136.2, 5) * mm, "end": v(-136.2, 2.5) * mm});
            skLineSegment(sketch, "E2814", {"start": v(-105.2, 2.5) * mm, "end": v(-105.2, 5) * mm});
            skLineSegment(sketch, "E2815", {"start": v(-105.2, 5) * mm, "end": v(-136.2, 5) * mm});
            skLineSegment(sketch, "E2816", {"start": v(-105.2, -5) * mm, "end": v(-112.94, -5) * mm});
            skLineSegment(sketch, "E2817", {"start": v(-112.94, -5) * mm, "end": v(-112.94, -2.5) * mm});
            skLineSegment(sketch, "E2818", {"start": v(-112.94, -2.5) * mm, "end": v(-105.2, -2.5) * mm});
            skLineSegment(sketch, "E2819", {"start": v(-105.2, 2.5) * mm, "end": v(-112.94, 2.5) * mm});
            skLineSegment(sketch, "E2820", {"start": v(-112.94, 2.5) * mm, "end": v(-112.94, 5) * mm});
            skLineSegment(sketch, "E2821", {"start": v(-112.94, 5) * mm, "end": v(-105.2, 5) * mm});
            skLineSegment(sketch, "E2822", {"start": v(-136.2, -5) * mm, "end": v(-128.44, -5) * mm});
            skLineSegment(sketch, "E2823", {"start": v(-128.44, -5) * mm, "end": v(-128.44, -2.5) * mm});
            skLineSegment(sketch, "E2824", {"start": v(-128.44, -2.5) * mm, "end": v(-136.2, -2.5) * mm});
            skLineSegment(sketch, "E2825", {"start": v(-136.2, 2.5) * mm, "end": v(-128.44, 2.5) * mm});
            skLineSegment(sketch, "E2826", {"start": v(-128.44, 2.5) * mm, "end": v(-128.44, 5) * mm});
            skSolve(sketch);
        }
        {
            var Q0;
            Q0 = qSketchRegion(id + "F8", true);
            extrude(context, id + "F9", {"entities" : qUnion([Q0]), "operationType" : NewBodyOperationType.REMOVE, "depth" : 25 * mm, "offsetDistance" : 25 * mm});
        }
        {
            var Q0;
            Q0=qCreatedBy(makeId("Top.planeOp"),FACE);
            var sketch = newSketch(context, id + "F10", { "sketchPlane" : qUnion([Q0])});
            skLineSegment(sketch, "E2827.bottom", {"start": v(-134.24, -90.55) * mm, "end": v(-105.28, -90.55) * mm});
            skLineSegment(sketch, "E2827.top", {"start": v(-134.24, -97.89) * mm, "end": v(-105.28, -97.89) * mm});
            skArc(sketch, "E2828", {"start": v(-134.24, -90.55) * mm, "mid": v(-137.9, -94.22) * mm, "end": v(-134.24, -97.89) * mm});
            skArc(sketch, "E2829", {"start": v(-105.28, -97.89) * mm, "mid": v(-101.62, -94.22) * mm, "end": v(-105.28, -90.55) * mm});
            skCircle(sketch, "E2830", {"center": v(-119.76, -94.22) * mm, "radius": 2.5 * mm});
            skSolve(sketch);
        }
        {
            var Q0;
            Q0=makeQuery(id+"F10.imprint","IMPRINT",FACE,{"disambiguationData":[TD([[makeQuery(id+"F10.imprint","IMPRINT",EDGE,{"derivedFrom":sQuery(id+"F10.wireOp",EDGE,"E2827.bottom")}),-1.0]])]});
            extrude(context, id + "F11", {"entities" : qUnion([Q0]), "depth" : 5 * mm, "offsetDistance" : 25 * mm});
        }
        {
            var Q0;
            Q0=qCreatedBy(makeId("Top.planeOp"),FACE);
            var sketch = newSketch(context, id + "F12", { "sketchPlane" : qUnion([Q0])});
            skLineSegment(sketch, "E2831.bottom", {"start": v(-138, -158.34) * mm, "end": v(-83, -158.34) * mm});
            skLineSegment(sketch, "E2831.top", {"start": v(-138, -190.84) * mm, "end": v(-83, -190.84) * mm});
            skLineSegment(sketch, "E2831.left", {"start": v(-138, -158.34) * mm, "end": v(-138, -190.84) * mm});
            skLineSegment(sketch, "E2831.right", {"start": v(-83, -158.34) * mm, "end": v(-83, -190.84) * mm});
            skLineSegment(sketch, "E2832", {"start": v(-138, -174.6) * mm, "end": v(-123.03, -174.6) * mm, "construction": true});
            skCircle(sketch, "E2833", {"center": v(-123.03, -174.6) * mm, "radius": 2.5 * mm});
            skSolve(sketch);
        }
        {
            var Q0;
            Q0=makeQuery(id+"F12.imprint","IMPRINT",FACE,{"disambiguationData":[TD([[makeQuery(id+"F12.imprint","IMPRINT",EDGE,{"derivedFrom":sQuery(id+"F12.wireOp",EDGE,"E2831.bottom")}),-1.0]])]});
            extrude(context, id + "F13", {"entities" : qUnion([Q0]), "depth" : 40 * mm, "offsetDistance" : 25 * mm});
        }
        {
            var Q0;
            Q0=makeQuery(id+"F12.imprint","IMPRINT",FACE,{"disambiguationData":[TD([[makeQuery(id+"F12.imprint","IMPRINT",EDGE,{"derivedFrom":sQuery(id+"F12.wireOp",EDGE,"E2833")}),1.0]])]});
            extrude(context, id + "F14", {"entities" : qUnion([Q0]), "operationType" : NewBodyOperationType.ADD, "depth" : 45 * mm, "offsetDistance" : 25 * mm});
        }
        {
            var Q0;
            Q0=qCreatedBy(makeId("Front.planeOp"),FACE);
            var sketch = newSketch(context, id + "F15", { "sketchPlane" : qUnion([Q0])});
            skCircle(sketch, "E2834", {"center": v(34.27, 12.2) * mm, "radius": 1.5 * mm});
            skSolve(sketch);
        }
        {
            var Q0;
            Q0 = qSketchRegion(id + "F15", true);
            extrude(context, id + "F16", {"entities" : qUnion([Q0]), "depth" : 57 * mm, "offsetDistance" : 25 * mm});
        }
        {
            var Q0;
            Q0=makeQuery(id+"F2.opExtrude","SWEPT_FACE",FACE,{"disambiguationData":[OSD([sQuery(id+"F1.wireOp",EDGE,"E2726")])]});
            var sketch = newSketch(context, id + "F17", { "sketchPlane" : qUnion([Q0])});
            skLineSegment(sketch, "E2835", {"start": v(10.21, -28.5) * mm, "end": v(67.21, 28.5) * mm, "construction": true});
            skLineSegment(sketch, "E2836", {"start": v(67.21, 28.5) * mm, "end": v(10.21, 28.5) * mm, "construction": true});
            skLineSegment(sketch, "E2837", {"start": v(10.21, 28.5) * mm, "end": v(67.21, -28.5) * mm, "construction": true});
            skCircle(sketch, "E2838", {"center": v(38.71, 0) * mm, "radius": 1.5 * mm});
            skSolve(sketch);
        }
        {
            var Q0;
            Q0=makeQuery(id+"F17.imprint","IMPRINT",FACE,{"disambiguationData":[TD([[makeQuery(id+"F17.imprint","IMPRINT",EDGE,{"derivedFrom":sQuery(id+"F17.wireOp",EDGE,"E2838")}),1.0]])]});
            extrude(context, id + "F18", {"entities" : qUnion([Q0]), "operationType" : NewBodyOperationType.REMOVE, "oppositeDirection" : true, "depth" : 100 * mm, "offsetDistance" : 25 * mm});
        }
    });
